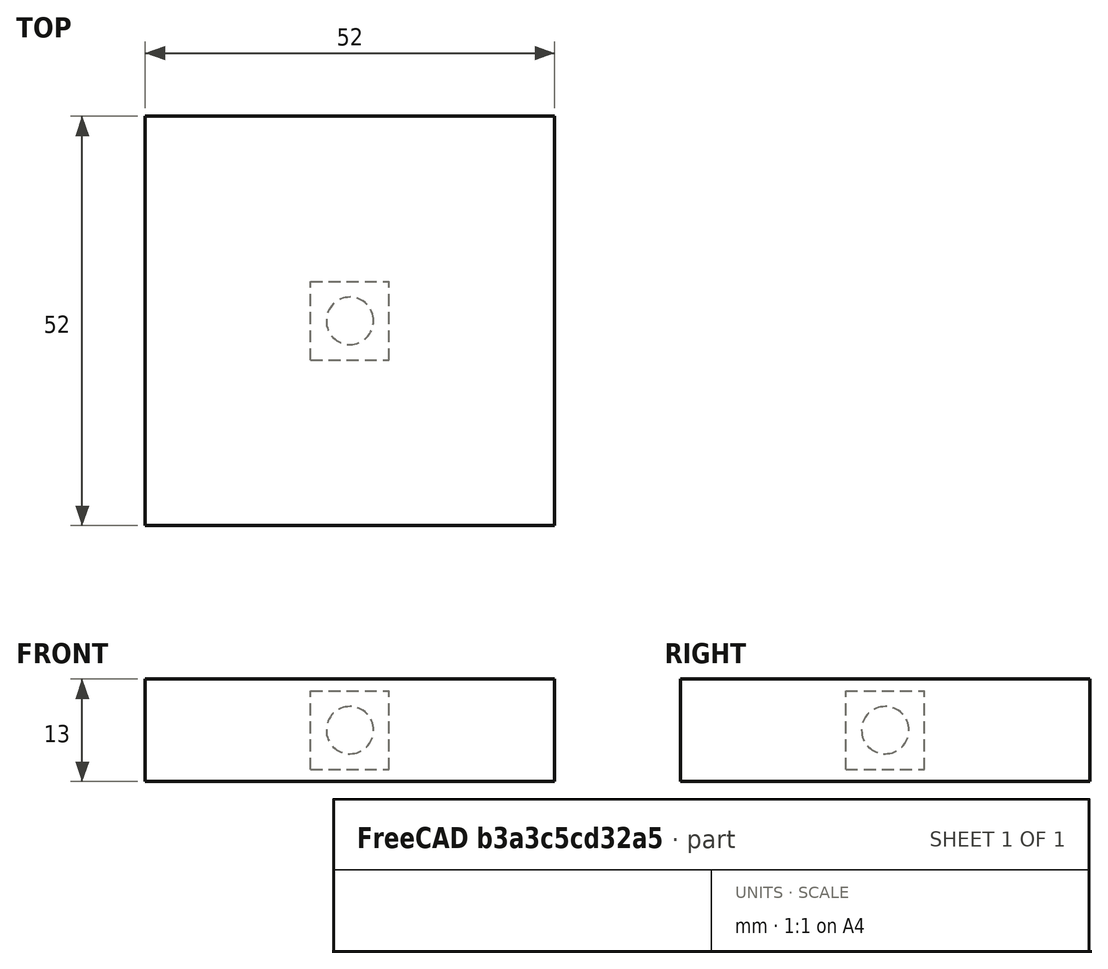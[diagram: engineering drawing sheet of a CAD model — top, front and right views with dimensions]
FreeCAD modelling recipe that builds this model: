
FCSTD DOCUMENT  (FreeCAD 0.21R33694 (Git))
Label: array-of-mother-daughter-vols-correct
License: All rights reserved
objects: App::DocumentObjectGroupPython×1251, Part::FeaturePython×5, App::Part×3
note: 3 computed .brp shape members not serialized (recipe doc carries the construction recipe); baked Part::Feature solids carry a one-line shape summary decoded from their .brp

FEATURE [App::DocumentObjectGroupPython] HALFPI  # scripted group (container) (typed FeaturePython)
  name = HALFPI
  value = pi/2.
FEATURE [App::DocumentObjectGroupPython] PI  # scripted group (container) (typed FeaturePython)
  name = PI
  value = 1.*pi
FEATURE [App::DocumentObjectGroupPython] TWOPI  # scripted group (container) (typed FeaturePython)
  name = TWOPI
  value = 2.*pi
FEATURE [App::DocumentObjectGroupPython] Constants  # scripted group (container) (typed FeaturePython)
  Group = -> [HALFPI,PI,TWOPI]
FEATURE [App::DocumentObjectGroupPython] Variables  # scripted group (container) (typed FeaturePython)
FEATURE [App::DocumentObjectGroupPython] Quantities  # scripted group (container) (typed FeaturePython)
FEATURE [App::DocumentObjectGroupPython] Isotopes  # scripted group (container) (typed FeaturePython)
FEATURE [App::DocumentObjectGroupPython] Elements  # scripted group (container) (typed FeaturePython)
FEATURE [App::DocumentObjectGroupPython] Matrix  # scripted group (container) (typed FeaturePython)
FEATURE [App::DocumentObjectGroupPython] Surfaces  # scripted group (container) (typed FeaturePython)
FEATURE [App::DocumentObjectGroupPython] Opticals  # scripted group (container) (typed FeaturePython)
  Group = -> [Matrix,Surfaces]
FEATURE [App::DocumentObjectGroupPython] G4Isotopes  # scripted group (container) (typed FeaturePython)
FEATURE [App::DocumentObjectGroupPython] H_element  # scripted group (container) (typed FeaturePython)
  Z = 1
  atom_value = 1.008
  formula = H
  name = H_element
FEATURE [App::DocumentObjectGroupPython] He_element  # scripted group (container) (typed FeaturePython)
  Z = 2
  atom_value = 4.0026
  formula = He
  name = He_element
FEATURE [App::DocumentObjectGroupPython] Li_element  # scripted group (container) (typed FeaturePython)
  Z = 3
  atom_value = 6.94
  formula = Li
  name = Li_element
FEATURE [App::DocumentObjectGroupPython] Be_element  # scripted group (container) (typed FeaturePython)
  Z = 4
  atom_value = 9.01218
  formula = Be
  name = Be_element
FEATURE [App::DocumentObjectGroupPython] B_element  # scripted group (container) (typed FeaturePython)
  Z = 5
  atom_value = 10.81
  formula = B
  name = B_element
FEATURE [App::DocumentObjectGroupPython] C_element  # scripted group (container) (typed FeaturePython)
  Z = 6
  atom_value = 12.011
  formula = C
  name = C_element
FEATURE [App::DocumentObjectGroupPython] N_element  # scripted group (container) (typed FeaturePython)
  Z = 7
  atom_value = 14.007
  formula = N
  name = N_element
FEATURE [App::DocumentObjectGroupPython] O_element  # scripted group (container) (typed FeaturePython)
  Z = 8
  atom_value = 15.999
  formula = O
  name = O_element
FEATURE [App::DocumentObjectGroupPython] F_element  # scripted group (container) (typed FeaturePython)
  Z = 9
  atom_value = 18.9984
  formula = F
  name = F_element
FEATURE [App::DocumentObjectGroupPython] Ne_element  # scripted group (container) (typed FeaturePython)
  Z = 10
  atom_value = 20.1797
  formula = Ne
  name = Ne_element
FEATURE [App::DocumentObjectGroupPython] Na_element  # scripted group (container) (typed FeaturePython)
  Z = 11
  atom_value = 22.9898
  formula = Na
  name = Na_element
FEATURE [App::DocumentObjectGroupPython] Mg_element  # scripted group (container) (typed FeaturePython)
  Z = 12
  atom_value = 24.305
  formula = Mg
  name = Mg_element
FEATURE [App::DocumentObjectGroupPython] Al_element  # scripted group (container) (typed FeaturePython)
  Z = 13
  atom_value = 26.9815
  formula = Al
  name = Al_element
FEATURE [App::DocumentObjectGroupPython] Si_element  # scripted group (container) (typed FeaturePython)
  Z = 14
  atom_value = 28.085
  formula = Si
  name = Si_element
FEATURE [App::DocumentObjectGroupPython] P_element  # scripted group (container) (typed FeaturePython)
  Z = 15
  atom_value = 30.9738
  formula = P
  name = P_element
FEATURE [App::DocumentObjectGroupPython] S_element  # scripted group (container) (typed FeaturePython)
  Z = 16
  atom_value = 32.06
  formula = S
  name = S_element
FEATURE [App::DocumentObjectGroupPython] Cl_element  # scripted group (container) (typed FeaturePython)
  Z = 17
  atom_value = 35.45
  formula = Cl
  name = Cl_element
FEATURE [App::DocumentObjectGroupPython] Ar_element  # scripted group (container) (typed FeaturePython)
  Z = 18
  atom_value = 39.95
  formula = Ar
  name = Ar_element
FEATURE [App::DocumentObjectGroupPython] K_element  # scripted group (container) (typed FeaturePython)
  Z = 19
  atom_value = 39.0983
  formula = K
  name = K_element
FEATURE [App::DocumentObjectGroupPython] Ca_element  # scripted group (container) (typed FeaturePython)
  Z = 20
  atom_value = 40.078
  formula = Ca
  name = Ca_element
FEATURE [App::DocumentObjectGroupPython] Sc_element  # scripted group (container) (typed FeaturePython)
  Z = 21
  atom_value = 44.9559
  formula = Sc
  name = Sc_element
FEATURE [App::DocumentObjectGroupPython] Ti_element  # scripted group (container) (typed FeaturePython)
  Z = 22
  atom_value = 47.867
  formula = Ti
  name = Ti_element
FEATURE [App::DocumentObjectGroupPython] V_element  # scripted group (container) (typed FeaturePython)
  Z = 23
  atom_value = 50.9415
  formula = V
  name = V_element
FEATURE [App::DocumentObjectGroupPython] Cr_element  # scripted group (container) (typed FeaturePython)
  Z = 24
  atom_value = 51.9961
  formula = Cr
  name = Cr_element
FEATURE [App::DocumentObjectGroupPython] Mn_element  # scripted group (container) (typed FeaturePython)
  Z = 25
  atom_value = 54.938
  formula = Mn
  name = Mn_element
FEATURE [App::DocumentObjectGroupPython] Fe_element  # scripted group (container) (typed FeaturePython)
  Z = 26
  atom_value = 55.845
  formula = Fe
  name = Fe_element
FEATURE [App::DocumentObjectGroupPython] Co_element  # scripted group (container) (typed FeaturePython)
  Z = 27
  atom_value = 58.9332
  formula = Co
  name = Co_element
FEATURE [App::DocumentObjectGroupPython] Ni_element  # scripted group (container) (typed FeaturePython)
  Z = 28
  atom_value = 58.6934
  formula = Ni
  name = Ni_element
FEATURE [App::DocumentObjectGroupPython] Cu_element  # scripted group (container) (typed FeaturePython)
  Z = 29
  atom_value = 63.546
  formula = Cu
  name = Cu_element
FEATURE [App::DocumentObjectGroupPython] Zn_element  # scripted group (container) (typed FeaturePython)
  Z = 30
  atom_value = 65.38
  formula = Zn
  name = Zn_element
FEATURE [App::DocumentObjectGroupPython] Ga_element  # scripted group (container) (typed FeaturePython)
  Z = 31
  atom_value = 69.723
  formula = Ga
  name = Ga_element
FEATURE [App::DocumentObjectGroupPython] Ge_element  # scripted group (container) (typed FeaturePython)
  Z = 32
  atom_value = 72.63
  formula = Ge
  name = Ge_element
FEATURE [App::DocumentObjectGroupPython] As_element  # scripted group (container) (typed FeaturePython)
  Z = 33
  atom_value = 74.9216
  formula = As
  name = As_element
FEATURE [App::DocumentObjectGroupPython] Se_element  # scripted group (container) (typed FeaturePython)
  Z = 34
  atom_value = 78.971
  formula = Se
  name = Se_element
FEATURE [App::DocumentObjectGroupPython] Br_element  # scripted group (container) (typed FeaturePython)
  Z = 35
  atom_value = 79.904
  formula = Br
  name = Br_element
FEATURE [App::DocumentObjectGroupPython] Kr_element  # scripted group (container) (typed FeaturePython)
  Z = 36
  atom_value = 83.798
  formula = Kr
  name = Kr_element
FEATURE [App::DocumentObjectGroupPython] Rb_element  # scripted group (container) (typed FeaturePython)
  Z = 37
  atom_value = 85.4678
  formula = Rb
  name = Rb_element
FEATURE [App::DocumentObjectGroupPython] Sr_element  # scripted group (container) (typed FeaturePython)
  Z = 38
  atom_value = 87.62
  formula = Sr
  name = Sr_element
FEATURE [App::DocumentObjectGroupPython] Y_element  # scripted group (container) (typed FeaturePython)
  Z = 39
  atom_value = 88.9058
  formula = Y
  name = Y_element
FEATURE [App::DocumentObjectGroupPython] Zr_element  # scripted group (container) (typed FeaturePython)
  Z = 40
  atom_value = 91.224
  formula = Zr
  name = Zr_element
FEATURE [App::DocumentObjectGroupPython] Nb_element  # scripted group (container) (typed FeaturePython)
  Z = 41
  atom_value = 92.9064
  formula = Nb
  name = Nb_element
FEATURE [App::DocumentObjectGroupPython] Mo_element  # scripted group (container) (typed FeaturePython)
  Z = 42
  atom_value = 95.95
  formula = Mo
  name = Mo_element
FEATURE [App::DocumentObjectGroupPython] Tc_element  # scripted group (container) (typed FeaturePython)
  Z = 43
  atom_value = 97
  formula = Tc
  name = Tc_element
FEATURE [App::DocumentObjectGroupPython] Ru_element  # scripted group (container) (typed FeaturePython)
  Z = 44
  atom_value = 101.07
  formula = Ru
  name = Ru_element
FEATURE [App::DocumentObjectGroupPython] Rh_element  # scripted group (container) (typed FeaturePython)
  Z = 45
  atom_value = 102.905
  formula = Rh
  name = Rh_element
FEATURE [App::DocumentObjectGroupPython] Pd_element  # scripted group (container) (typed FeaturePython)
  Z = 46
  atom_value = 106.42
  formula = Pd
  name = Pd_element
FEATURE [App::DocumentObjectGroupPython] Ag_element  # scripted group (container) (typed FeaturePython)
  Z = 47
  atom_value = 107.868
  formula = Ag
  name = Ag_element
FEATURE [App::DocumentObjectGroupPython] Cd_element  # scripted group (container) (typed FeaturePython)
  Z = 48
  atom_value = 112.414
  formula = Cd
  name = Cd_element
FEATURE [App::DocumentObjectGroupPython] In_element  # scripted group (container) (typed FeaturePython)
  Z = 49
  atom_value = 114.818
  formula = In
  name = In_element
FEATURE [App::DocumentObjectGroupPython] Sn_element  # scripted group (container) (typed FeaturePython)
  Z = 50
  atom_value = 118.71
  formula = Sn
  name = Sn_element
FEATURE [App::DocumentObjectGroupPython] Sb_element  # scripted group (container) (typed FeaturePython)
  Z = 51
  atom_value = 121.76
  formula = Sb
  name = Sb_element
FEATURE [App::DocumentObjectGroupPython] Te_element  # scripted group (container) (typed FeaturePython)
  Z = 52
  atom_value = 127.6
  formula = Te
  name = Te_element
FEATURE [App::DocumentObjectGroupPython] I_element  # scripted group (container) (typed FeaturePython)
  Z = 53
  atom_value = 126.904
  formula = I
  name = I_element
FEATURE [App::DocumentObjectGroupPython] Xe_element  # scripted group (container) (typed FeaturePython)
  Z = 54
  atom_value = 131.293
  formula = Xe
  name = Xe_element
FEATURE [App::DocumentObjectGroupPython] Cs_element  # scripted group (container) (typed FeaturePython)
  Z = 55
  atom_value = 132.905
  formula = Cs
  name = Cs_element
FEATURE [App::DocumentObjectGroupPython] Ba_element  # scripted group (container) (typed FeaturePython)
  Z = 56
  atom_value = 137.327
  formula = Ba
  name = Ba_element
FEATURE [App::DocumentObjectGroupPython] La_element  # scripted group (container) (typed FeaturePython)
  Z = 57
  atom_value = 138.905
  formula = La
  name = La_element
FEATURE [App::DocumentObjectGroupPython] Ce_element  # scripted group (container) (typed FeaturePython)
  Z = 58
  atom_value = 140.116
  formula = Ce
  name = Ce_element
FEATURE [App::DocumentObjectGroupPython] Pr_element  # scripted group (container) (typed FeaturePython)
  Z = 59
  atom_value = 140.908
  formula = Pr
  name = Pr_element
FEATURE [App::DocumentObjectGroupPython] Nd_element  # scripted group (container) (typed FeaturePython)
  Z = 60
  atom_value = 144.242
  formula = Nd
  name = Nd_element
FEATURE [App::DocumentObjectGroupPython] Pm_element  # scripted group (container) (typed FeaturePython)
  Z = 61
  atom_value = 145
  formula = Pm
  name = Pm_element
FEATURE [App::DocumentObjectGroupPython] Sm_element  # scripted group (container) (typed FeaturePython)
  Z = 62
  atom_value = 150.36
  formula = Sm
  name = Sm_element
FEATURE [App::DocumentObjectGroupPython] Eu_element  # scripted group (container) (typed FeaturePython)
  Z = 63
  atom_value = 151.964
  formula = Eu
  name = Eu_element
FEATURE [App::DocumentObjectGroupPython] Gd_element  # scripted group (container) (typed FeaturePython)
  Z = 64
  atom_value = 157.25
  formula = Gd
  name = Gd_element
FEATURE [App::DocumentObjectGroupPython] Tb_element  # scripted group (container) (typed FeaturePython)
  Z = 65
  atom_value = 158.925
  formula = Tb
  name = Tb_element
FEATURE [App::DocumentObjectGroupPython] Dy_element  # scripted group (container) (typed FeaturePython)
  Z = 66
  atom_value = 162.5
  formula = Dy
  name = Dy_element
FEATURE [App::DocumentObjectGroupPython] Ho_element  # scripted group (container) (typed FeaturePython)
  Z = 67
  atom_value = 164.93
  formula = Ho
  name = Ho_element
FEATURE [App::DocumentObjectGroupPython] Er_element  # scripted group (container) (typed FeaturePython)
  Z = 68
  atom_value = 167.259
  formula = Er
  name = Er_element
FEATURE [App::DocumentObjectGroupPython] Tm_element  # scripted group (container) (typed FeaturePython)
  Z = 69
  atom_value = 168.934
  formula = Tm
  name = Tm_element
FEATURE [App::DocumentObjectGroupPython] Yb_element  # scripted group (container) (typed FeaturePython)
  Z = 70
  atom_value = 173.045
  formula = Yb
  name = Yb_element
FEATURE [App::DocumentObjectGroupPython] Lu_element  # scripted group (container) (typed FeaturePython)
  Z = 71
  atom_value = 174.967
  formula = Lu
  name = Lu_element
FEATURE [App::DocumentObjectGroupPython] Hf_element  # scripted group (container) (typed FeaturePython)
  Z = 72
  atom_value = 178.49
  formula = Hf
  name = Hf_element
FEATURE [App::DocumentObjectGroupPython] Ta_element  # scripted group (container) (typed FeaturePython)
  Z = 73
  atom_value = 180.948
  formula = Ta
  name = Ta_element
FEATURE [App::DocumentObjectGroupPython] W_element  # scripted group (container) (typed FeaturePython)
  Z = 74
  atom_value = 183.84
  formula = W
  name = W_element
FEATURE [App::DocumentObjectGroupPython] Re_element  # scripted group (container) (typed FeaturePython)
  Z = 75
  atom_value = 186.207
  formula = Re
  name = Re_element
FEATURE [App::DocumentObjectGroupPython] Os_element  # scripted group (container) (typed FeaturePython)
  Z = 76
  atom_value = 190.23
  formula = Os
  name = Os_element
FEATURE [App::DocumentObjectGroupPython] Ir_element  # scripted group (container) (typed FeaturePython)
  Z = 77
  atom_value = 192.217
  formula = Ir
  name = Ir_element
FEATURE [App::DocumentObjectGroupPython] Pt_element  # scripted group (container) (typed FeaturePython)
  Z = 78
  atom_value = 195.084
  formula = Pt
  name = Pt_element
FEATURE [App::DocumentObjectGroupPython] Au_element  # scripted group (container) (typed FeaturePython)
  Z = 79
  atom_value = 196.967
  formula = Au
  name = Au_element
FEATURE [App::DocumentObjectGroupPython] Hg_element  # scripted group (container) (typed FeaturePython)
  Z = 80
  atom_value = 200.592
  formula = Hg
  name = Hg_element
FEATURE [App::DocumentObjectGroupPython] Tl_element  # scripted group (container) (typed FeaturePython)
  Z = 81
  atom_value = 204.38
  formula = Tl
  name = Tl_element
FEATURE [App::DocumentObjectGroupPython] Pb_element  # scripted group (container) (typed FeaturePython)
  Z = 82
  atom_value = 207.2
  formula = Pb
  name = Pb_element
FEATURE [App::DocumentObjectGroupPython] Bi_element  # scripted group (container) (typed FeaturePython)
  Z = 83
  atom_value = 208.98
  formula = Bi
  name = Bi_element
FEATURE [App::DocumentObjectGroupPython] Po_element  # scripted group (container) (typed FeaturePython)
  Z = 84
  atom_value = 209
  formula = Po
  name = Po_element
FEATURE [App::DocumentObjectGroupPython] At_element  # scripted group (container) (typed FeaturePython)
  Z = 85
  atom_value = 210
  formula = At
  name = At_element
FEATURE [App::DocumentObjectGroupPython] Rn_element  # scripted group (container) (typed FeaturePython)
  Z = 86
  atom_value = 222
  formula = Rn
  name = Rn_element
FEATURE [App::DocumentObjectGroupPython] Fr_element  # scripted group (container) (typed FeaturePython)
  Z = 87
  atom_value = 223
  formula = Fr
  name = Fr_element
FEATURE [App::DocumentObjectGroupPython] Ra_element  # scripted group (container) (typed FeaturePython)
  Z = 88
  atom_value = 226
  formula = Ra
  name = Ra_element
FEATURE [App::DocumentObjectGroupPython] Ac_element  # scripted group (container) (typed FeaturePython)
  Z = 89
  atom_value = 227
  formula = Ac
  name = Ac_element
FEATURE [App::DocumentObjectGroupPython] Th_element  # scripted group (container) (typed FeaturePython)
  Z = 90
  atom_value = 232.038
  formula = Th
  name = Th_element
FEATURE [App::DocumentObjectGroupPython] Pa_element  # scripted group (container) (typed FeaturePython)
  Z = 91
  atom_value = 231.036
  formula = Pa
  name = Pa_element
FEATURE [App::DocumentObjectGroupPython] U_element  # scripted group (container) (typed FeaturePython)
  Z = 92
  atom_value = 238.029
  formula = U
  name = U_element
FEATURE [App::DocumentObjectGroupPython] Np_element  # scripted group (container) (typed FeaturePython)
  Z = 93
  atom_value = 237
  formula = Np
  name = Np_element
FEATURE [App::DocumentObjectGroupPython] Pu_element  # scripted group (container) (typed FeaturePython)
  Z = 94
  atom_value = 244
  formula = Pu
  name = Pu_element
FEATURE [App::DocumentObjectGroupPython] Am_element  # scripted group (container) (typed FeaturePython)
  Z = 95
  atom_value = 243
  formula = Am
  name = Am_element
FEATURE [App::DocumentObjectGroupPython] Cm_element  # scripted group (container) (typed FeaturePython)
  Z = 96
  atom_value = 247
  formula = Cm
  name = Cm_element
FEATURE [App::DocumentObjectGroupPython] Bk_element  # scripted group (container) (typed FeaturePython)
  Z = 97
  atom_value = 247
  formula = Bk
  name = Bk_element
FEATURE [App::DocumentObjectGroupPython] Cf_element  # scripted group (container) (typed FeaturePython)
  Z = 98
  atom_value = 251
  formula = Cf
  name = Cf_element
FEATURE [App::DocumentObjectGroupPython] G4Elements  # scripted group (container) (typed FeaturePython)
  Group = -> [H_element,He_element,Li_element,Be_element,B_element,C_element,N_element,O_element,F_element,Ne_element,Na_element,Mg_element,Al_element,Si_element,P_element,S_element,Cl_element,Ar_element,K_element,Ca_element,Sc_element,Ti_element,V_element,Cr_element,Mn_element,Fe_element,Co_element,Ni_element,Cu_element,Zn_element,Ga_element,Ge_element,As_element,Se_element,Br_element,Kr_element,Rb_element,+61 more]
FEATURE [App::DocumentObjectGroupPython] H_element001  label="H_element : 0.101"  # scripted group (container) (typed FeaturePython)
  n = 0.101327
FEATURE [App::DocumentObjectGroupPython] C_element001  label="C_element : 0.775"  # scripted group (container) (typed FeaturePython)
  n = 0.7755
FEATURE [App::DocumentObjectGroupPython] N_element001  label="N_element : 0.035"  # scripted group (container) (typed FeaturePython)
  n = 0.035057
FEATURE [App::DocumentObjectGroupPython] O_element001  label="O_element : 0.052"  # scripted group (container) (typed FeaturePython)
  n = 0.0523159
FEATURE [App::DocumentObjectGroupPython] F_element001  label="F_element : 0.017"  # scripted group (container) (typed FeaturePython)
  n = 0.017422
FEATURE [App::DocumentObjectGroupPython] Ca_element001  label="Ca_element : 0.018"  # scripted group (container) (typed FeaturePython)
  n = 0.018378
FEATURE [App::DocumentObjectGroupPython] G4_A_150_TISSUE  label="G4_A-150_TISSUE"  # scripted group (container) (typed FeaturePython)
  Dunit = g/cm3
  Dvalue = 1.127
  Group = -> [H_element001,C_element001,N_element001,O_element001,F_element001,Ca_element001]
  conduct = 2
  density = 1
  expand = 3
  formula = G4_A-150_TISSUE
  name = G4_A-150_TISSUE
  specific = 4
FEATURE [App::DocumentObjectGroupPython] C_element002  label="C_element : 3"  # scripted group (container) (typed FeaturePython)
  n = 3
  ref = C_element
FEATURE [App::DocumentObjectGroupPython] H_element002  label="H_element : 6"  # scripted group (container) (typed FeaturePython)
  n = 6
  ref = H_element
FEATURE [App::DocumentObjectGroupPython] O_element002  label="O_element : 1"  # scripted group (container) (typed FeaturePython)
  n = 1
  ref = O_element
FEATURE [App::DocumentObjectGroupPython] G4_ACETONE  # scripted group (container) (typed FeaturePython)
  Dunit = g/cm3
  Dvalue = 0.7899
  Group = -> [C_element002,H_element002,O_element002]
  conduct = 2
  density = 1
  expand = 3
  formula = G4_ACETONE
  name = G4_ACETONE
  specific = 4
FEATURE [App::DocumentObjectGroupPython] C_element003  label="C_element : 2"  # scripted group (container) (typed FeaturePython)
  n = 2
  ref = C_element
FEATURE [App::DocumentObjectGroupPython] H_element003  label="H_element : 2"  # scripted group (container) (typed FeaturePython)
  n = 2
  ref = H_element
FEATURE [App::DocumentObjectGroupPython] G4_ACETYLENE  # scripted group (container) (typed FeaturePython)
  Dunit = g/cm3
  Dvalue = 0.0010967
  Group = -> [C_element003,H_element003]
  conduct = 2
  density = 1
  expand = 3
  formula = G4_ACETYLENE
  name = G4_ACETYLENE
  specific = 4
FEATURE [App::DocumentObjectGroupPython] C_element004  label="C_element : 5"  # scripted group (container) (typed FeaturePython)
  n = 5
  ref = C_element
FEATURE [App::DocumentObjectGroupPython] H_element004  label="H_element : 5"  # scripted group (container) (typed FeaturePython)
  n = 5
  ref = H_element
FEATURE [App::DocumentObjectGroupPython] N_element002  label="N_element : 5"  # scripted group (container) (typed FeaturePython)
  n = 5
  ref = N_element
FEATURE [App::DocumentObjectGroupPython] G4_ADENINE  # scripted group (container) (typed FeaturePython)
  Dunit = g/cm3
  Dvalue = 1.6
  Group = -> [C_element004,H_element004,N_element002]
  conduct = 2
  density = 1
  expand = 3
  formula = G4_ADENINE
  name = G4_ADENINE
  specific = 4
FEATURE [App::DocumentObjectGroupPython] H_element005  label="H_element : 0.114"  # scripted group (container) (typed FeaturePython)
  n = 0.114
FEATURE [App::DocumentObjectGroupPython] C_element005  label="C_element : 0.598"  # scripted group (container) (typed FeaturePython)
  n = 0.598
FEATURE [App::DocumentObjectGroupPython] N_element003  label="N_element : 0.007"  # scripted group (container) (typed FeaturePython)
  n = 0.007
FEATURE [App::DocumentObjectGroupPython] O_element003  label="O_element : 0.278"  # scripted group (container) (typed FeaturePython)
  n = 0.278
FEATURE [App::DocumentObjectGroupPython] Na_element001  label="Na_element : 0.001"  # scripted group (container) (typed FeaturePython)
  n = 0.001
FEATURE [App::DocumentObjectGroupPython] S_element001  label="S_element : 0.001"  # scripted group (container) (typed FeaturePython)
  n = 0.001
FEATURE [App::DocumentObjectGroupPython] Cl_element001  label="Cl_element : 0.001"  # scripted group (container) (typed FeaturePython)
  n = 0.001
FEATURE [App::DocumentObjectGroupPython] G4_ADIPOSE_TISSUE_ICRP  # scripted group (container) (typed FeaturePython)
  Dunit = g/cm3
  Dvalue = 0.95
  Group = -> [H_element005,C_element005,N_element003,O_element003,Na_element001,S_element001,Cl_element001]
  conduct = 2
  density = 1
  expand = 3
  formula = G4_ADIPOSE_TISSUE_ICRP
  name = G4_ADIPOSE_TISSUE_ICRP
  specific = 4
FEATURE [App::DocumentObjectGroupPython] C_element006  label="C_element : 0.000"  # scripted group (container) (typed FeaturePython)
  n = 0.000124
FEATURE [App::DocumentObjectGroupPython] N_element004  label="N_element : 0.755"  # scripted group (container) (typed FeaturePython)
  n = 0.755268
FEATURE [App::DocumentObjectGroupPython] O_element004  label="O_element : 0.232"  # scripted group (container) (typed FeaturePython)
  n = 0.231781
FEATURE [App::DocumentObjectGroupPython] Ar_element001  label="Ar_element : 0.013"  # scripted group (container) (typed FeaturePython)
  n = 0.012827
FEATURE [App::DocumentObjectGroupPython] G4_AIR  # scripted group (container) (typed FeaturePython)
  Dunit = g/cm3
  Dvalue = 0.00120479
  Group = -> [C_element006,N_element004,O_element004,Ar_element001]
  conduct = 2
  density = 1
  expand = 3
  formula = G4_AIR
  name = G4_AIR
  specific = 4
FEATURE [App::DocumentObjectGroupPython] C_element007  label="C_element : 006"  # scripted group (container) (typed FeaturePython)
  n = 3
  ref = C_element
FEATURE [App::DocumentObjectGroupPython] H_element006  label="H_element : 7"  # scripted group (container) (typed FeaturePython)
  n = 7
  ref = H_element
FEATURE [App::DocumentObjectGroupPython] N_element005  label="N_element : 1"  # scripted group (container) (typed FeaturePython)
  n = 1
  ref = N_element
FEATURE [App::DocumentObjectGroupPython] O_element005  label="O_element : 2"  # scripted group (container) (typed FeaturePython)
  n = 2
  ref = O_element
FEATURE [App::DocumentObjectGroupPython] G4_ALANINE  # scripted group (container) (typed FeaturePython)
  Dunit = g/cm3
  Dvalue = 1.42
  Group = -> [C_element007,H_element006,N_element005,O_element005]
  conduct = 2
  density = 1
  expand = 3
  formula = G4_ALANINE
  name = G4_ALANINE
  specific = 4
FEATURE [App::DocumentObjectGroupPython] Al_element001  label="Al_element : 2"  # scripted group (container) (typed FeaturePython)
  n = 2
  ref = Al_element
FEATURE [App::DocumentObjectGroupPython] O_element006  label="O_element : 3"  # scripted group (container) (typed FeaturePython)
  n = 3
  ref = O_element
FEATURE [App::DocumentObjectGroupPython] G4_ALUMINUM_OXIDE  # scripted group (container) (typed FeaturePython)
  Dunit = g/cm3
  Dvalue = 3.97
  Group = -> [Al_element001,O_element006]
  conduct = 2
  density = 1
  expand = 3
  formula = G4_ALUMINUM_OXIDE
  name = G4_ALUMINUM_OXIDE
  specific = 4
FEATURE [App::DocumentObjectGroupPython] H_element007  label="H_element : 0.106"  # scripted group (container) (typed FeaturePython)
  n = 0.10593
FEATURE [App::DocumentObjectGroupPython] C_element008  label="C_element : 0.789"  # scripted group (container) (typed FeaturePython)
  n = 0.788974
FEATURE [App::DocumentObjectGroupPython] O_element007  label="O_element : 0.105"  # scripted group (container) (typed FeaturePython)
  n = 0.105096
FEATURE [App::DocumentObjectGroupPython] G4_AMBER  # scripted group (container) (typed FeaturePython)
  Dunit = g/cm3
  Dvalue = 1.1
  Group = -> [H_element007,C_element008,O_element007]
  conduct = 2
  density = 1
  expand = 3
  formula = G4_AMBER
  name = G4_AMBER
  specific = 4
FEATURE [App::DocumentObjectGroupPython] N_element006  label="N_element : 006"  # scripted group (container) (typed FeaturePython)
  n = 1
  ref = N_element
FEATURE [App::DocumentObjectGroupPython] H_element008  label="H_element : 3"  # scripted group (container) (typed FeaturePython)
  n = 3
  ref = H_element
FEATURE [App::DocumentObjectGroupPython] G4_AMMONIA  # scripted group (container) (typed FeaturePython)
  Dunit = g/cm3
  Dvalue = 0.000826019
  Group = -> [N_element006,H_element008]
  conduct = 2
  density = 1
  expand = 3
  formula = G4_AMMONIA
  name = G4_AMMONIA
  specific = 4
FEATURE [App::DocumentObjectGroupPython] C_element009  label="C_element : 6"  # scripted group (container) (typed FeaturePython)
  n = 6
  ref = C_element
FEATURE [App::DocumentObjectGroupPython] H_element009  label="H_element : 008"  # scripted group (container) (typed FeaturePython)
  n = 7
  ref = H_element
FEATURE [App::DocumentObjectGroupPython] N_element007  label="N_element : 007"  # scripted group (container) (typed FeaturePython)
  n = 1
  ref = N_element
FEATURE [App::DocumentObjectGroupPython] G4_ANILINE  # scripted group (container) (typed FeaturePython)
  Dunit = g/cm3
  Dvalue = 1.0235
  Group = -> [C_element009,H_element009,N_element007]
  conduct = 2
  density = 1
  expand = 3
  formula = G4_ANILINE
  name = G4_ANILINE
  specific = 4
FEATURE [App::DocumentObjectGroupPython] C_element010  label="C_element : 14"  # scripted group (container) (typed FeaturePython)
  n = 14
  ref = C_element
FEATURE [App::DocumentObjectGroupPython] H_element010  label="H_element : 10"  # scripted group (container) (typed FeaturePython)
  n = 10
  ref = H_element
FEATURE [App::DocumentObjectGroupPython] G4_ANTHRACENE  # scripted group (container) (typed FeaturePython)
  Dunit = g/cm3
  Dvalue = 1.283
  Group = -> [C_element010,H_element010]
  conduct = 2
  density = 1
  expand = 3
  formula = G4_ANTHRACENE
  name = G4_ANTHRACENE
  specific = 4
FEATURE [App::DocumentObjectGroupPython] H_element011  label="H_element : 0.065"  # scripted group (container) (typed FeaturePython)
  n = 0.0654709
FEATURE [App::DocumentObjectGroupPython] C_element011  label="C_element : 0.537"  # scripted group (container) (typed FeaturePython)
  n = 0.536944
FEATURE [App::DocumentObjectGroupPython] N_element008  label="N_element : 0.021"  # scripted group (container) (typed FeaturePython)
  n = 0.0215
FEATURE [App::DocumentObjectGroupPython] O_element008  label="O_element : 0.032"  # scripted group (container) (typed FeaturePython)
  n = 0.032085
FEATURE [App::DocumentObjectGroupPython] F_element002  label="F_element : 0.167"  # scripted group (container) (typed FeaturePython)
  n = 0.167411
FEATURE [App::DocumentObjectGroupPython] Ca_element002  label="Ca_element : 0.177"  # scripted group (container) (typed FeaturePython)
  n = 0.176589
FEATURE [App::DocumentObjectGroupPython] G4_B_100_BONE  label="G4_B-100_BONE"  # scripted group (container) (typed FeaturePython)
  Dunit = g/cm3
  Dvalue = 1.45
  Group = -> [H_element011,C_element011,N_element008,O_element008,F_element002,Ca_element002]
  conduct = 2
  density = 1
  expand = 3
  formula = G4_B-100_BONE
  name = G4_B-100_BONE
  specific = 4
FEATURE [App::DocumentObjectGroupPython] H_element012  label="H_element : 0.057"  # scripted group (container) (typed FeaturePython)
  n = 0.057441
FEATURE [App::DocumentObjectGroupPython] C_element012  label="C_element : 0.790"  # scripted group (container) (typed FeaturePython)
  n = 0.774591
FEATURE [App::DocumentObjectGroupPython] O_element009  label="O_element : 0.168"  # scripted group (container) (typed FeaturePython)
  n = 0.167968
FEATURE [App::DocumentObjectGroupPython] G4_BAKELITE  # scripted group (container) (typed FeaturePython)
  Dunit = g/cm3
  Dvalue = 1.25
  Group = -> [H_element012,C_element012,O_element009]
  conduct = 2
  density = 1
  expand = 3
  formula = G4_BAKELITE
  name = G4_BAKELITE
  specific = 4
FEATURE [App::DocumentObjectGroupPython] Ba_element001  label="Ba_element : 1"  # scripted group (container) (typed FeaturePython)
  n = 1
  ref = Ba_element
FEATURE [App::DocumentObjectGroupPython] F_element003  label="F_element : 2"  # scripted group (container) (typed FeaturePython)
  n = 2
  ref = F_element
FEATURE [App::DocumentObjectGroupPython] G4_BARIUM_FLUORIDE  # scripted group (container) (typed FeaturePython)
  Dunit = g/cm3
  Dvalue = 4.89
  Group = -> [Ba_element001,F_element003]
  conduct = 2
  density = 1
  expand = 3
  formula = G4_BARIUM_FLUORIDE
  name = G4_BARIUM_FLUORIDE
  specific = 4
FEATURE [App::DocumentObjectGroupPython] Ba_element002  label="Ba_element : 002"  # scripted group (container) (typed FeaturePython)
  n = 1
  ref = Ba_element
FEATURE [App::DocumentObjectGroupPython] S_element002  label="S_element : 1"  # scripted group (container) (typed FeaturePython)
  n = 1
  ref = S_element
FEATURE [App::DocumentObjectGroupPython] O_element010  label="O_element : 4"  # scripted group (container) (typed FeaturePython)
  n = 4
  ref = O_element
FEATURE [App::DocumentObjectGroupPython] G4_BARIUM_SULFATE  # scripted group (container) (typed FeaturePython)
  Dunit = g/cm3
  Dvalue = 4.5
  Group = -> [Ba_element002,S_element002,O_element010]
  conduct = 2
  density = 1
  expand = 3
  formula = G4_BARIUM_SULFATE
  name = G4_BARIUM_SULFATE
  specific = 4
FEATURE [App::DocumentObjectGroupPython] C_element013  label="C_element : 007"  # scripted group (container) (typed FeaturePython)
  n = 6
  ref = C_element
FEATURE [App::DocumentObjectGroupPython] H_element013  label="H_element : 009"  # scripted group (container) (typed FeaturePython)
  n = 6
  ref = H_element
FEATURE [App::DocumentObjectGroupPython] G4_BENZENE  # scripted group (container) (typed FeaturePython)
  Dunit = g/cm3
  Dvalue = 0.87865
  Group = -> [C_element013,H_element013]
  conduct = 2
  density = 1
  expand = 3
  formula = G4_BENZENE
  name = G4_BENZENE
  specific = 4
FEATURE [App::DocumentObjectGroupPython] Be_element001  label="Be_element : 1"  # scripted group (container) (typed FeaturePython)
  n = 1
  ref = Be_element
FEATURE [App::DocumentObjectGroupPython] O_element011  label="O_element : 005"  # scripted group (container) (typed FeaturePython)
  n = 1
  ref = O_element
FEATURE [App::DocumentObjectGroupPython] G4_BERYLLIUM_OXIDE  # scripted group (container) (typed FeaturePython)
  Dunit = g/cm3
  Dvalue = 3.01
  Group = -> [Be_element001,O_element011]
  conduct = 2
  density = 1
  expand = 3
  formula = G4_BERYLLIUM_OXIDE
  name = G4_BERYLLIUM_OXIDE
  specific = 4
FEATURE [App::DocumentObjectGroupPython] Bi_element001  label="Bi_element : 4"  # scripted group (container) (typed FeaturePython)
  n = 4
  ref = Bi_element
FEATURE [App::DocumentObjectGroupPython] Ge_element001  label="Ge_element : 3"  # scripted group (container) (typed FeaturePython)
  n = 3
  ref = Ge_element
FEATURE [App::DocumentObjectGroupPython] O_element012  label="O_element : 12"  # scripted group (container) (typed FeaturePython)
  n = 12
  ref = O_element
FEATURE [App::DocumentObjectGroupPython] G4_BGO  # scripted group (container) (typed FeaturePython)
  Dunit = g/cm3
  Dvalue = 7.13
  Group = -> [Bi_element001,Ge_element001,O_element012]
  conduct = 2
  density = 1
  expand = 3
  formula = G4_BGO
  name = G4_BGO
  specific = 4
FEATURE [App::DocumentObjectGroupPython] H_element014  label="H_element : 0.102"  # scripted group (container) (typed FeaturePython)
  n = 0.102
FEATURE [App::DocumentObjectGroupPython] C_element014  label="C_element : 0.110"  # scripted group (container) (typed FeaturePython)
  n = 0.11
FEATURE [App::DocumentObjectGroupPython] N_element009  label="N_element : 0.033"  # scripted group (container) (typed FeaturePython)
  n = 0.033
FEATURE [App::DocumentObjectGroupPython] O_element013  label="O_element : 0.745"  # scripted group (container) (typed FeaturePython)
  n = 0.745
FEATURE [App::DocumentObjectGroupPython] Na_element002  label="Na_element : 0.002"  # scripted group (container) (typed FeaturePython)
  n = 0.001
FEATURE [App::DocumentObjectGroupPython] P_element001  label="P_element : 0.001"  # scripted group (container) (typed FeaturePython)
  n = 0.001
FEATURE [App::DocumentObjectGroupPython] S_element003  label="S_element : 0.002"  # scripted group (container) (typed FeaturePython)
  n = 0.002
FEATURE [App::DocumentObjectGroupPython] Cl_element002  label="Cl_element : 0.003"  # scripted group (container) (typed FeaturePython)
  n = 0.003
FEATURE [App::DocumentObjectGroupPython] K_element001  label="K_element : 0.002"  # scripted group (container) (typed FeaturePython)
  n = 0.002
FEATURE [App::DocumentObjectGroupPython] Fe_element001  label="Fe_element : 0.001"  # scripted group (container) (typed FeaturePython)
  n = 0.001
FEATURE [App::DocumentObjectGroupPython] G4_BLOOD_ICRP  # scripted group (container) (typed FeaturePython)
  Dunit = g/cm3
  Dvalue = 1.06
  Group = -> [H_element014,C_element014,N_element009,O_element013,Na_element002,P_element001,S_element003,Cl_element002,K_element001,Fe_element001]
  conduct = 2
  density = 1
  expand = 3
  formula = G4_BLOOD_ICRP
  name = G4_BLOOD_ICRP
  specific = 4
FEATURE [App::DocumentObjectGroupPython] H_element015  label="H_element : 0.064"  # scripted group (container) (typed FeaturePython)
  n = 0.064
FEATURE [App::DocumentObjectGroupPython] C_element015  label="C_element : 0.278"  # scripted group (container) (typed FeaturePython)
  n = 0.278
FEATURE [App::DocumentObjectGroupPython] N_element010  label="N_element : 0.027"  # scripted group (container) (typed FeaturePython)
  n = 0.027
FEATURE [App::DocumentObjectGroupPython] O_element014  label="O_element : 0.410"  # scripted group (container) (typed FeaturePython)
  n = 0.41
FEATURE [App::DocumentObjectGroupPython] Mg_element001  label="Mg_element : 0.002"  # scripted group (container) (typed FeaturePython)
  n = 0.002
FEATURE [App::DocumentObjectGroupPython] P_element002  label="P_element : 0.070"  # scripted group (container) (typed FeaturePython)
  n = 0.07
FEATURE [App::DocumentObjectGroupPython] S_element004  label="S_element : 0.003"  # scripted group (container) (typed FeaturePython)
  n = 0.002
FEATURE [App::DocumentObjectGroupPython] Ca_element003  label="Ca_element : 0.147"  # scripted group (container) (typed FeaturePython)
  n = 0.147
FEATURE [App::DocumentObjectGroupPython] G4_BONE_COMPACT_ICRU  # scripted group (container) (typed FeaturePython)
  Dunit = g/cm3
  Dvalue = 1.85
  Group = -> [H_element015,C_element015,N_element010,O_element014,Mg_element001,P_element002,S_element004,Ca_element003]
  conduct = 2
  density = 1
  expand = 3
  formula = G4_BONE_COMPACT_ICRU
  name = G4_BONE_COMPACT_ICRU
  specific = 4
FEATURE [App::DocumentObjectGroupPython] H_element016  label="H_element : 0.034"  # scripted group (container) (typed FeaturePython)
  n = 0.034
FEATURE [App::DocumentObjectGroupPython] C_element016  label="C_element : 0.155"  # scripted group (container) (typed FeaturePython)
  n = 0.155
FEATURE [App::DocumentObjectGroupPython] N_element011  label="N_element : 0.042"  # scripted group (container) (typed FeaturePython)
  n = 0.042
FEATURE [App::DocumentObjectGroupPython] O_element015  label="O_element : 0.435"  # scripted group (container) (typed FeaturePython)
  n = 0.435
FEATURE [App::DocumentObjectGroupPython] Na_element003  label="Na_element : 0.003"  # scripted group (container) (typed FeaturePython)
  n = 0.001
FEATURE [App::DocumentObjectGroupPython] Mg_element002  label="Mg_element : 0.003"  # scripted group (container) (typed FeaturePython)
  n = 0.002
FEATURE [App::DocumentObjectGroupPython] P_element003  label="P_element : 0.103"  # scripted group (container) (typed FeaturePython)
  n = 0.103
FEATURE [App::DocumentObjectGroupPython] S_element005  label="S_element : 0.004"  # scripted group (container) (typed FeaturePython)
  n = 0.003
FEATURE [App::DocumentObjectGroupPython] Ca_element004  label="Ca_element : 0.225"  # scripted group (container) (typed FeaturePython)
  n = 0.225
FEATURE [App::DocumentObjectGroupPython] G4_BONE_CORTICAL_ICRP  # scripted group (container) (typed FeaturePython)
  Dunit = g/cm3
  Dvalue = 1.92
  Group = -> [H_element016,C_element016,N_element011,O_element015,Na_element003,Mg_element002,P_element003,S_element005,Ca_element004]
  conduct = 2
  density = 1
  expand = 3
  formula = G4_BONE_CORTICAL_ICRP
  name = G4_BONE_CORTICAL_ICRP
  specific = 4
FEATURE [App::DocumentObjectGroupPython] B_element001  label="B_element : 4"  # scripted group (container) (typed FeaturePython)
  n = 4
  ref = B_element
FEATURE [App::DocumentObjectGroupPython] C_element017  label="C_element : 1"  # scripted group (container) (typed FeaturePython)
  n = 1
  ref = C_element
FEATURE [App::DocumentObjectGroupPython] G4_BORON_CARBIDE  # scripted group (container) (typed FeaturePython)
  Dunit = g/cm3
  Dvalue = 2.52
  Group = -> [B_element001,C_element017]
  conduct = 2
  density = 1
  expand = 3
  formula = G4_BORON_CARBIDE
  name = G4_BORON_CARBIDE
  specific = 4
FEATURE [App::DocumentObjectGroupPython] B_element002  label="B_element : 2"  # scripted group (container) (typed FeaturePython)
  n = 2
  ref = B_element
FEATURE [App::DocumentObjectGroupPython] O_element016  label="O_element : 006"  # scripted group (container) (typed FeaturePython)
  n = 3
  ref = O_element
FEATURE [App::DocumentObjectGroupPython] G4_BORON_OXIDE  # scripted group (container) (typed FeaturePython)
  Dunit = g/cm3
  Dvalue = 1.812
  Group = -> [B_element002,O_element016]
  conduct = 2
  density = 1
  expand = 3
  formula = G4_BORON_OXIDE
  name = G4_BORON_OXIDE
  specific = 4
FEATURE [App::DocumentObjectGroupPython] H_element017  label="H_element : 0.107"  # scripted group (container) (typed FeaturePython)
  n = 0.107
FEATURE [App::DocumentObjectGroupPython] C_element018  label="C_element : 0.145"  # scripted group (container) (typed FeaturePython)
  n = 0.145
FEATURE [App::DocumentObjectGroupPython] N_element012  label="N_element : 0.022"  # scripted group (container) (typed FeaturePython)
  n = 0.022
FEATURE [App::DocumentObjectGroupPython] O_element017  label="O_element : 0.712"  # scripted group (container) (typed FeaturePython)
  n = 0.712
FEATURE [App::DocumentObjectGroupPython] Na_element004  label="Na_element : 0.004"  # scripted group (container) (typed FeaturePython)
  n = 0.002
FEATURE [App::DocumentObjectGroupPython] P_element004  label="P_element : 0.004"  # scripted group (container) (typed FeaturePython)
  n = 0.004
FEATURE [App::DocumentObjectGroupPython] S_element006  label="S_element : 0.005"  # scripted group (container) (typed FeaturePython)
  n = 0.002
FEATURE [App::DocumentObjectGroupPython] Cl_element003  label="Cl_element : 0.004"  # scripted group (container) (typed FeaturePython)
  n = 0.003
FEATURE [App::DocumentObjectGroupPython] K_element002  label="K_element : 0.003"  # scripted group (container) (typed FeaturePython)
  n = 0.003
FEATURE [App::DocumentObjectGroupPython] G4_BRAIN_ICRP  # scripted group (container) (typed FeaturePython)
  Dunit = g/cm3
  Dvalue = 1.04
  Group = -> [H_element017,C_element018,N_element012,O_element017,Na_element004,P_element004,S_element006,Cl_element003,K_element002]
  conduct = 2
  density = 1
  expand = 3
  formula = G4_BRAIN_ICRP
  name = G4_BRAIN_ICRP
  specific = 4
FEATURE [App::DocumentObjectGroupPython] C_element019  label="C_element : 4"  # scripted group (container) (typed FeaturePython)
  n = 4
  ref = C_element
FEATURE [App::DocumentObjectGroupPython] H_element018  label="H_element : 010"  # scripted group (container) (typed FeaturePython)
  n = 10
  ref = H_element
FEATURE [App::DocumentObjectGroupPython] G4_BUTANE  # scripted group (container) (typed FeaturePython)
  Dunit = g/cm3
  Dvalue = 0.00249343
  Group = -> [C_element019,H_element018]
  conduct = 2
  density = 1
  expand = 3
  formula = G4_BUTANE
  name = G4_BUTANE
  specific = 4
FEATURE [App::DocumentObjectGroupPython] C_element020  label="C_element : 008"  # scripted group (container) (typed FeaturePython)
  n = 4
  ref = C_element
FEATURE [App::DocumentObjectGroupPython] H_element019  label="H_element : 011"  # scripted group (container) (typed FeaturePython)
  n = 10
  ref = H_element
FEATURE [App::DocumentObjectGroupPython] O_element018  label="O_element : 007"  # scripted group (container) (typed FeaturePython)
  n = 1
  ref = O_element
FEATURE [App::DocumentObjectGroupPython] G4_N_BUTYL_ALCOHOL  label="G4_N-BUTYL_ALCOHOL"  # scripted group (container) (typed FeaturePython)
  Dunit = g/cm3
  Dvalue = 0.8098
  Group = -> [C_element020,H_element019,O_element018]
  conduct = 2
  density = 1
  expand = 3
  formula = G4_N-BUTYL_ALCOHOL
  name = G4_N-BUTYL_ALCOHOL
  specific = 4
FEATURE [App::DocumentObjectGroupPython] H_element020  label="H_element : 0.025"  # scripted group (container) (typed FeaturePython)
  n = 0.02468
FEATURE [App::DocumentObjectGroupPython] C_element021  label="C_element : 0.502"  # scripted group (container) (typed FeaturePython)
  n = 0.501611
FEATURE [App::DocumentObjectGroupPython] O_element019  label="O_element : 0.005"  # scripted group (container) (typed FeaturePython)
  n = 0.004527
FEATURE [App::DocumentObjectGroupPython] F_element004  label="F_element : 0.465"  # scripted group (container) (typed FeaturePython)
  n = 0.465209
FEATURE [App::DocumentObjectGroupPython] Si_element001  label="Si_element : 0.004"  # scripted group (container) (typed FeaturePython)
  n = 0.003973
FEATURE [App::DocumentObjectGroupPython] G4_C_552  label="G4_C-552"  # scripted group (container) (typed FeaturePython)
  Dunit = g/cm3
  Dvalue = 1.76
  Group = -> [H_element020,C_element021,O_element019,F_element004,Si_element001]
  conduct = 2
  density = 1
  expand = 3
  formula = G4_C-552
  name = G4_C-552
  specific = 4
FEATURE [App::DocumentObjectGroupPython] Cd_element001  label="Cd_element : 1"  # scripted group (container) (typed FeaturePython)
  n = 1
  ref = Cd_element
FEATURE [App::DocumentObjectGroupPython] Te_element001  label="Te_element : 1"  # scripted group (container) (typed FeaturePython)
  n = 1
  ref = Te_element
FEATURE [App::DocumentObjectGroupPython] G4_CADMIUM_TELLURIDE  # scripted group (container) (typed FeaturePython)
  Dunit = g/cm3
  Dvalue = 6.2
  Group = -> [Cd_element001,Te_element001]
  conduct = 2
  density = 1
  expand = 3
  formula = G4_CADMIUM_TELLURIDE
  name = G4_CADMIUM_TELLURIDE
  specific = 4
FEATURE [App::DocumentObjectGroupPython] Cd_element002  label="Cd_element : 002"  # scripted group (container) (typed FeaturePython)
  n = 1
  ref = Cd_element
FEATURE [App::DocumentObjectGroupPython] W_element001  label="W_element : 1"  # scripted group (container) (typed FeaturePython)
  n = 1
  ref = W_element
FEATURE [App::DocumentObjectGroupPython] O_element020  label="O_element : 008"  # scripted group (container) (typed FeaturePython)
  n = 4
  ref = O_element
FEATURE [App::DocumentObjectGroupPython] G4_CADMIUM_TUNGSTATE  # scripted group (container) (typed FeaturePython)
  Dunit = g/cm3
  Dvalue = 7.9
  Group = -> [Cd_element002,W_element001,O_element020]
  conduct = 2
  density = 1
  expand = 3
  formula = G4_CADMIUM_TUNGSTATE
  name = G4_CADMIUM_TUNGSTATE
  specific = 4
FEATURE [App::DocumentObjectGroupPython] Ca_element005  label="Ca_element : 1"  # scripted group (container) (typed FeaturePython)
  n = 1
  ref = Ca_element
FEATURE [App::DocumentObjectGroupPython] C_element022  label="C_element : 009"  # scripted group (container) (typed FeaturePython)
  n = 1
  ref = C_element
FEATURE [App::DocumentObjectGroupPython] O_element021  label="O_element : 009"  # scripted group (container) (typed FeaturePython)
  n = 3
  ref = O_element
FEATURE [App::DocumentObjectGroupPython] G4_CALCIUM_CARBONATE  # scripted group (container) (typed FeaturePython)
  Dunit = g/cm3
  Dvalue = 2.8
  Group = -> [Ca_element005,C_element022,O_element021]
  conduct = 2
  density = 1
  expand = 3
  formula = G4_CALCIUM_CARBONATE
  name = G4_CALCIUM_CARBONATE
  specific = 4
FEATURE [App::DocumentObjectGroupPython] Ca_element006  label="Ca_element : 002"  # scripted group (container) (typed FeaturePython)
  n = 1
  ref = Ca_element
FEATURE [App::DocumentObjectGroupPython] F_element005  label="F_element : 003"  # scripted group (container) (typed FeaturePython)
  n = 2
  ref = F_element
FEATURE [App::DocumentObjectGroupPython] G4_CALCIUM_FLUORIDE  # scripted group (container) (typed FeaturePython)
  Dunit = g/cm3
  Dvalue = 3.18
  Group = -> [Ca_element006,F_element005]
  conduct = 2
  density = 1
  expand = 3
  formula = G4_CALCIUM_FLUORIDE
  name = G4_CALCIUM_FLUORIDE
  specific = 4
FEATURE [App::DocumentObjectGroupPython] Ca_element007  label="Ca_element : 003"  # scripted group (container) (typed FeaturePython)
  n = 1
  ref = Ca_element
FEATURE [App::DocumentObjectGroupPython] O_element022  label="O_element : 010"  # scripted group (container) (typed FeaturePython)
  n = 1
  ref = O_element
FEATURE [App::DocumentObjectGroupPython] G4_CALCIUM_OXIDE  # scripted group (container) (typed FeaturePython)
  Dunit = g/cm3
  Dvalue = 3.3
  Group = -> [Ca_element007,O_element022]
  conduct = 2
  density = 1
  expand = 3
  formula = G4_CALCIUM_OXIDE
  name = G4_CALCIUM_OXIDE
  specific = 4
FEATURE [App::DocumentObjectGroupPython] Ca_element008  label="Ca_element : 004"  # scripted group (container) (typed FeaturePython)
  n = 1
  ref = Ca_element
FEATURE [App::DocumentObjectGroupPython] S_element007  label="S_element : 002"  # scripted group (container) (typed FeaturePython)
  n = 1
  ref = S_element
FEATURE [App::DocumentObjectGroupPython] O_element023  label="O_element : 011"  # scripted group (container) (typed FeaturePython)
  n = 4
  ref = O_element
FEATURE [App::DocumentObjectGroupPython] G4_CALCIUM_SULFATE  # scripted group (container) (typed FeaturePython)
  Dunit = g/cm3
  Dvalue = 2.96
  Group = -> [Ca_element008,S_element007,O_element023]
  conduct = 2
  density = 1
  expand = 3
  formula = G4_CALCIUM_SULFATE
  name = G4_CALCIUM_SULFATE
  specific = 4
FEATURE [App::DocumentObjectGroupPython] Ca_element009  label="Ca_element : 005"  # scripted group (container) (typed FeaturePython)
  n = 1
  ref = Ca_element
FEATURE [App::DocumentObjectGroupPython] W_element002  label="W_element : 002"  # scripted group (container) (typed FeaturePython)
  n = 1
  ref = W_element
FEATURE [App::DocumentObjectGroupPython] O_element024  label="O_element : 012"  # scripted group (container) (typed FeaturePython)
  n = 4
  ref = O_element
FEATURE [App::DocumentObjectGroupPython] G4_CALCIUM_TUNGSTATE  # scripted group (container) (typed FeaturePython)
  Dunit = g/cm3
  Dvalue = 6.062
  Group = -> [Ca_element009,W_element002,O_element024]
  conduct = 2
  density = 1
  expand = 3
  formula = G4_CALCIUM_TUNGSTATE
  name = G4_CALCIUM_TUNGSTATE
  specific = 4
FEATURE [App::DocumentObjectGroupPython] C_element023  label="C_element : 010"  # scripted group (container) (typed FeaturePython)
  n = 1
  ref = C_element
FEATURE [App::DocumentObjectGroupPython] O_element025  label="O_element : 013"  # scripted group (container) (typed FeaturePython)
  n = 2
  ref = O_element
FEATURE [App::DocumentObjectGroupPython] G4_CARBON_DIOXIDE  # scripted group (container) (typed FeaturePython)
  Dunit = g/cm3
  Dvalue = 0.00184212
  Group = -> [C_element023,O_element025]
  conduct = 2
  density = 1
  expand = 3
  formula = G4_CARBON_DIOXIDE
  name = G4_CARBON_DIOXIDE
  specific = 4
FEATURE [App::DocumentObjectGroupPython] C_element024  label="C_element : 011"  # scripted group (container) (typed FeaturePython)
  n = 1
  ref = C_element
FEATURE [App::DocumentObjectGroupPython] Cl_element004  label="Cl_element : 4"  # scripted group (container) (typed FeaturePython)
  n = 4
  ref = Cl_element
FEATURE [App::DocumentObjectGroupPython] G4_CARBON_TETRACHLORIDE  # scripted group (container) (typed FeaturePython)
  Dunit = g/cm3
  Dvalue = 1.594
  Group = -> [C_element024,Cl_element004]
  conduct = 2
  density = 1
  expand = 3
  formula = G4_CARBON_TETRACHLORIDE
  name = G4_CARBON_TETRACHLORIDE
  specific = 4
FEATURE [App::DocumentObjectGroupPython] C_element025  label="C_element : 012"  # scripted group (container) (typed FeaturePython)
  n = 6
  ref = C_element
FEATURE [App::DocumentObjectGroupPython] H_element021  label="H_element : 012"  # scripted group (container) (typed FeaturePython)
  n = 10
  ref = H_element
FEATURE [App::DocumentObjectGroupPython] O_element026  label="O_element : 5"  # scripted group (container) (typed FeaturePython)
  n = 5
  ref = O_element
FEATURE [App::DocumentObjectGroupPython] G4_CELLULOSE_CELLOPHANE  # scripted group (container) (typed FeaturePython)
  Dunit = g/cm3
  Dvalue = 1.42
  Group = -> [C_element025,H_element021,O_element026]
  conduct = 2
  density = 1
  expand = 3
  formula = G4_CELLULOSE_CELLOPHANE
  name = G4_CELLULOSE_CELLOPHANE
  specific = 4
FEATURE [App::DocumentObjectGroupPython] H_element022  label="H_element : 0.067"  # scripted group (container) (typed FeaturePython)
  n = 0.067125
FEATURE [App::DocumentObjectGroupPython] C_element026  label="C_element : 0.545"  # scripted group (container) (typed FeaturePython)
  n = 0.545403
FEATURE [App::DocumentObjectGroupPython] O_element027  label="O_element : 0.387"  # scripted group (container) (typed FeaturePython)
  n = 0.387472
FEATURE [App::DocumentObjectGroupPython] G4_CELLULOSE_BUTYRATE  # scripted group (container) (typed FeaturePython)
  Dunit = g/cm3
  Dvalue = 1.2
  Group = -> [H_element022,C_element026,O_element027]
  conduct = 2
  density = 1
  expand = 3
  formula = G4_CELLULOSE_BUTYRATE
  name = G4_CELLULOSE_BUTYRATE
  specific = 4
FEATURE [App::DocumentObjectGroupPython] H_element023  label="H_element : 0.029"  # scripted group (container) (typed FeaturePython)
  n = 0.029216
FEATURE [App::DocumentObjectGroupPython] C_element027  label="C_element : 0.271"  # scripted group (container) (typed FeaturePython)
  n = 0.271296
FEATURE [App::DocumentObjectGroupPython] N_element013  label="N_element : 0.121"  # scripted group (container) (typed FeaturePython)
  n = 0.121276
FEATURE [App::DocumentObjectGroupPython] O_element028  label="O_element : 0.578"  # scripted group (container) (typed FeaturePython)
  n = 0.578212
FEATURE [App::DocumentObjectGroupPython] G4_CELLULOSE_NITRATE  # scripted group (container) (typed FeaturePython)
  Dunit = g/cm3
  Dvalue = 1.49
  Group = -> [H_element023,C_element027,N_element013,O_element028]
  conduct = 2
  density = 1
  expand = 3
  formula = G4_CELLULOSE_NITRATE
  name = G4_CELLULOSE_NITRATE
  specific = 4
FEATURE [App::DocumentObjectGroupPython] H_element024  label="H_element : 0.108"  # scripted group (container) (typed FeaturePython)
  n = 0.107596
FEATURE [App::DocumentObjectGroupPython] N_element014  label="N_element : 0.001"  # scripted group (container) (typed FeaturePython)
  n = 0.0008
FEATURE [App::DocumentObjectGroupPython] O_element029  label="O_element : 0.875"  # scripted group (container) (typed FeaturePython)
  n = 0.874976
FEATURE [App::DocumentObjectGroupPython] S_element008  label="S_element : 0.015"  # scripted group (container) (typed FeaturePython)
  n = 0.014627
FEATURE [App::DocumentObjectGroupPython] Ce_element001  label="Ce_element : 0.002"  # scripted group (container) (typed FeaturePython)
  n = 0.002001
FEATURE [App::DocumentObjectGroupPython] G4_CERIC_SULFATE  # scripted group (container) (typed FeaturePython)
  Dunit = g/cm3
  Dvalue = 1.03
  Group = -> [H_element024,N_element014,O_element029,S_element008,Ce_element001]
  conduct = 2
  density = 1
  expand = 3
  formula = G4_CERIC_SULFATE
  name = G4_CERIC_SULFATE
  specific = 4
FEATURE [App::DocumentObjectGroupPython] Cs_element001  label="Cs_element : 1"  # scripted group (container) (typed FeaturePython)
  n = 1
  ref = Cs_element
FEATURE [App::DocumentObjectGroupPython] F_element006  label="F_element : 1"  # scripted group (container) (typed FeaturePython)
  n = 1
  ref = F_element
FEATURE [App::DocumentObjectGroupPython] G4_CESIUM_FLUORIDE  # scripted group (container) (typed FeaturePython)
  Dunit = g/cm3
  Dvalue = 4.115
  Group = -> [Cs_element001,F_element006]
  conduct = 2
  density = 1
  expand = 3
  formula = G4_CESIUM_FLUORIDE
  name = G4_CESIUM_FLUORIDE
  specific = 4
FEATURE [App::DocumentObjectGroupPython] Cs_element002  label="Cs_element : 002"  # scripted group (container) (typed FeaturePython)
  n = 1
  ref = Cs_element
FEATURE [App::DocumentObjectGroupPython] I_element001  label="I_element : 1"  # scripted group (container) (typed FeaturePython)
  n = 1
  ref = I_element
FEATURE [App::DocumentObjectGroupPython] G4_CESIUM_IODIDE  # scripted group (container) (typed FeaturePython)
  Dunit = g/cm3
  Dvalue = 4.51
  Group = -> [Cs_element002,I_element001]
  conduct = 2
  density = 1
  expand = 3
  formula = G4_CESIUM_IODIDE
  name = G4_CESIUM_IODIDE
  specific = 4
FEATURE [App::DocumentObjectGroupPython] C_element028  label="C_element : 013"  # scripted group (container) (typed FeaturePython)
  n = 6
  ref = C_element
FEATURE [App::DocumentObjectGroupPython] H_element025  label="H_element : 013"  # scripted group (container) (typed FeaturePython)
  n = 5
  ref = H_element
FEATURE [App::DocumentObjectGroupPython] Cl_element005  label="Cl_element : 1"  # scripted group (container) (typed FeaturePython)
  n = 1
  ref = Cl_element
FEATURE [App::DocumentObjectGroupPython] G4_CHLOROBENZENE  # scripted group (container) (typed FeaturePython)
  Dunit = g/cm3
  Dvalue = 1.1058
  Group = -> [C_element028,H_element025,Cl_element005]
  conduct = 2
  density = 1
  expand = 3
  formula = G4_CHLOROBENZENE
  name = G4_CHLOROBENZENE
  specific = 4
FEATURE [App::DocumentObjectGroupPython] C_element029  label="C_element : 014"  # scripted group (container) (typed FeaturePython)
  n = 1
  ref = C_element
FEATURE [App::DocumentObjectGroupPython] H_element026  label="H_element : 1"  # scripted group (container) (typed FeaturePython)
  n = 1
  ref = H_element
FEATURE [App::DocumentObjectGroupPython] Cl_element006  label="Cl_element : 3"  # scripted group (container) (typed FeaturePython)
  n = 3
  ref = Cl_element
FEATURE [App::DocumentObjectGroupPython] G4_CHLOROFORM  # scripted group (container) (typed FeaturePython)
  Dunit = g/cm3
  Dvalue = 1.4832
  Group = -> [C_element029,H_element026,Cl_element006]
  conduct = 2
  density = 1
  expand = 3
  formula = G4_CHLOROFORM
  name = G4_CHLOROFORM
  specific = 4
FEATURE [App::DocumentObjectGroupPython] H_element027  label="H_element : 0.010"  # scripted group (container) (typed FeaturePython)
  n = 0.01
FEATURE [App::DocumentObjectGroupPython] C_element030  label="C_element : 0.001"  # scripted group (container) (typed FeaturePython)
  n = 0.001
FEATURE [App::DocumentObjectGroupPython] O_element030  label="O_element : 0.529"  # scripted group (container) (typed FeaturePython)
  n = 0.529107
FEATURE [App::DocumentObjectGroupPython] Na_element005  label="Na_element : 0.016"  # scripted group (container) (typed FeaturePython)
  n = 0.016
FEATURE [App::DocumentObjectGroupPython] Mg_element003  label="Mg_element : 0.004"  # scripted group (container) (typed FeaturePython)
  n = 0.002
FEATURE [App::DocumentObjectGroupPython] Al_element002  label="Al_element : 0.034"  # scripted group (container) (typed FeaturePython)
  n = 0.033872
FEATURE [App::DocumentObjectGroupPython] Si_element002  label="Si_element : 0.337"  # scripted group (container) (typed FeaturePython)
  n = 0.337021
FEATURE [App::DocumentObjectGroupPython] K_element003  label="K_element : 0.013"  # scripted group (container) (typed FeaturePython)
  n = 0.013
FEATURE [App::DocumentObjectGroupPython] Ca_element010  label="Ca_element : 0.044"  # scripted group (container) (typed FeaturePython)
  n = 0.044
FEATURE [App::DocumentObjectGroupPython] Fe_element002  label="Fe_element : 0.014"  # scripted group (container) (typed FeaturePython)
  n = 0.014
FEATURE [App::DocumentObjectGroupPython] G4_CONCRETE  # scripted group (container) (typed FeaturePython)
  Dunit = g/cm3
  Dvalue = 2.3
  Group = -> [H_element027,C_element030,O_element030,Na_element005,Mg_element003,Al_element002,Si_element002,K_element003,Ca_element010,Fe_element002]
  conduct = 2
  density = 1
  expand = 3
  formula = G4_CONCRETE
  name = G4_CONCRETE
  specific = 4
FEATURE [App::DocumentObjectGroupPython] C_element031  label="C_element : 015"  # scripted group (container) (typed FeaturePython)
  n = 6
  ref = C_element
FEATURE [App::DocumentObjectGroupPython] H_element028  label="H_element : 12"  # scripted group (container) (typed FeaturePython)
  n = 12
  ref = H_element
FEATURE [App::DocumentObjectGroupPython] G4_CYCLOHEXANE  # scripted group (container) (typed FeaturePython)
  Dunit = g/cm3
  Dvalue = 0.779
  Group = -> [C_element031,H_element028]
  conduct = 2
  density = 1
  expand = 3
  formula = G4_CYCLOHEXANE
  name = G4_CYCLOHEXANE
  specific = 4
FEATURE [App::DocumentObjectGroupPython] C_element032  label="C_element : 016"  # scripted group (container) (typed FeaturePython)
  n = 6
  ref = C_element
FEATURE [App::DocumentObjectGroupPython] H_element029  label="H_element : 4"  # scripted group (container) (typed FeaturePython)
  n = 4
  ref = H_element
FEATURE [App::DocumentObjectGroupPython] Cl_element007  label="Cl_element : 2"  # scripted group (container) (typed FeaturePython)
  n = 2
  ref = Cl_element
FEATURE [App::DocumentObjectGroupPython] G4_1_2_DICHLOROBENZENE  label="G4_1.2-DICHLOROBENZENE"  # scripted group (container) (typed FeaturePython)
  Dunit = g/cm3
  Dvalue = 1.3048
  Group = -> [C_element032,H_element029,Cl_element007]
  conduct = 2
  density = 1
  expand = 3
  formula = G4_1.2-DICHLOROBENZENE
  name = G4_1.2-DICHLOROBENZENE
  specific = 4
FEATURE [App::DocumentObjectGroupPython] C_element033  label="C_element : 017"  # scripted group (container) (typed FeaturePython)
  n = 4
  ref = C_element
FEATURE [App::DocumentObjectGroupPython] H_element030  label="H_element : 8"  # scripted group (container) (typed FeaturePython)
  n = 8
  ref = H_element
FEATURE [App::DocumentObjectGroupPython] O_element031  label="O_element : 014"  # scripted group (container) (typed FeaturePython)
  n = 1
  ref = O_element
FEATURE [App::DocumentObjectGroupPython] Cl_element008  label="Cl_element : 005"  # scripted group (container) (typed FeaturePython)
  n = 2
  ref = Cl_element
FEATURE [App::DocumentObjectGroupPython] G4_DICHLORODIETHYL_ETHER  # scripted group (container) (typed FeaturePython)
  Dunit = g/cm3
  Dvalue = 1.2199
  Group = -> [C_element033,H_element030,O_element031,Cl_element008]
  conduct = 2
  density = 1
  expand = 3
  formula = G4_DICHLORODIETHYL_ETHER
  name = G4_DICHLORODIETHYL_ETHER
  specific = 4
FEATURE [App::DocumentObjectGroupPython] C_element034  label="C_element : 018"  # scripted group (container) (typed FeaturePython)
  n = 2
  ref = C_element
FEATURE [App::DocumentObjectGroupPython] H_element031  label="H_element : 014"  # scripted group (container) (typed FeaturePython)
  n = 4
  ref = H_element
FEATURE [App::DocumentObjectGroupPython] Cl_element009  label="Cl_element : 006"  # scripted group (container) (typed FeaturePython)
  n = 2
  ref = Cl_element
FEATURE [App::DocumentObjectGroupPython] G4_1_2_DICHLOROETHANE  label="G4_1.2-DICHLOROETHANE"  # scripted group (container) (typed FeaturePython)
  Dunit = g/cm3
  Dvalue = 1.2351
  Group = -> [C_element034,H_element031,Cl_element009]
  conduct = 2
  density = 1
  expand = 3
  formula = G4_1.2-DICHLOROETHANE
  name = G4_1.2-DICHLOROETHANE
  specific = 4
FEATURE [App::DocumentObjectGroupPython] C_element035  label="C_element : 019"  # scripted group (container) (typed FeaturePython)
  n = 4
  ref = C_element
FEATURE [App::DocumentObjectGroupPython] H_element032  label="H_element : 015"  # scripted group (container) (typed FeaturePython)
  n = 10
  ref = H_element
FEATURE [App::DocumentObjectGroupPython] O_element032  label="O_element : 015"  # scripted group (container) (typed FeaturePython)
  n = 1
  ref = O_element
FEATURE [App::DocumentObjectGroupPython] G4_DIETHYL_ETHER  # scripted group (container) (typed FeaturePython)
  Dunit = g/cm3
  Dvalue = 0.71378
  Group = -> [C_element035,H_element032,O_element032]
  conduct = 2
  density = 1
  expand = 3
  formula = G4_DIETHYL_ETHER
  name = G4_DIETHYL_ETHER
  specific = 4
FEATURE [App::DocumentObjectGroupPython] C_element036  label="C_element : 020"  # scripted group (container) (typed FeaturePython)
  n = 3
  ref = C_element
FEATURE [App::DocumentObjectGroupPython] H_element033  label="H_element : 016"  # scripted group (container) (typed FeaturePython)
  n = 7
  ref = H_element
FEATURE [App::DocumentObjectGroupPython] N_element015  label="N_element : 008"  # scripted group (container) (typed FeaturePython)
  n = 1
  ref = N_element
FEATURE [App::DocumentObjectGroupPython] O_element033  label="O_element : 016"  # scripted group (container) (typed FeaturePython)
  n = 1
  ref = O_element
FEATURE [App::DocumentObjectGroupPython] G4_N_N_DIMETHYL_FORMAMIDE  label="G4_N.N-DIMETHYL_FORMAMIDE"  # scripted group (container) (typed FeaturePython)
  Dunit = g/cm3
  Dvalue = 0.9487
  Group = -> [C_element036,H_element033,N_element015,O_element033]
  conduct = 2
  density = 1
  expand = 3
  formula = G4_N.N-DIMETHYL_FORMAMIDE
  name = G4_N.N-DIMETHYL_FORMAMIDE
  specific = 4
FEATURE [App::DocumentObjectGroupPython] C_element037  label="C_element : 021"  # scripted group (container) (typed FeaturePython)
  n = 2
  ref = C_element
FEATURE [App::DocumentObjectGroupPython] H_element034  label="H_element : 017"  # scripted group (container) (typed FeaturePython)
  n = 6
  ref = H_element
FEATURE [App::DocumentObjectGroupPython] O_element034  label="O_element : 017"  # scripted group (container) (typed FeaturePython)
  n = 1
  ref = O_element
FEATURE [App::DocumentObjectGroupPython] S_element009  label="S_element : 003"  # scripted group (container) (typed FeaturePython)
  n = 1
  ref = S_element
FEATURE [App::DocumentObjectGroupPython] G4_DIMETHYL_SULFOXIDE  # scripted group (container) (typed FeaturePython)
  Dunit = g/cm3
  Dvalue = 1.1014
  Group = -> [C_element037,H_element034,O_element034,S_element009]
  conduct = 2
  density = 1
  expand = 3
  formula = G4_DIMETHYL_SULFOXIDE
  name = G4_DIMETHYL_SULFOXIDE
  specific = 4
FEATURE [App::DocumentObjectGroupPython] C_element038  label="C_element : 022"  # scripted group (container) (typed FeaturePython)
  n = 2
  ref = C_element
FEATURE [App::DocumentObjectGroupPython] H_element035  label="H_element : 018"  # scripted group (container) (typed FeaturePython)
  n = 6
  ref = H_element
FEATURE [App::DocumentObjectGroupPython] G4_ETHANE  # scripted group (container) (typed FeaturePython)
  Dunit = g/cm3
  Dvalue = 0.00125324
  Group = -> [C_element038,H_element035]
  conduct = 2
  density = 1
  expand = 3
  formula = G4_ETHANE
  name = G4_ETHANE
  specific = 4
FEATURE [App::DocumentObjectGroupPython] C_element039  label="C_element : 023"  # scripted group (container) (typed FeaturePython)
  n = 2
  ref = C_element
FEATURE [App::DocumentObjectGroupPython] H_element036  label="H_element : 019"  # scripted group (container) (typed FeaturePython)
  n = 6
  ref = H_element
FEATURE [App::DocumentObjectGroupPython] O_element035  label="O_element : 018"  # scripted group (container) (typed FeaturePython)
  n = 1
  ref = O_element
FEATURE [App::DocumentObjectGroupPython] G4_ETHYL_ALCOHOL  # scripted group (container) (typed FeaturePython)
  Dunit = g/cm3
  Dvalue = 0.7893
  Group = -> [C_element039,H_element036,O_element035]
  conduct = 2
  density = 1
  expand = 3
  formula = G4_ETHYL_ALCOHOL
  name = G4_ETHYL_ALCOHOL
  specific = 4
FEATURE [App::DocumentObjectGroupPython] H_element037  label="H_element : 0.090"  # scripted group (container) (typed FeaturePython)
  n = 0.090027
FEATURE [App::DocumentObjectGroupPython] C_element040  label="C_element : 0.585"  # scripted group (container) (typed FeaturePython)
  n = 0.585182
FEATURE [App::DocumentObjectGroupPython] O_element036  label="O_element : 0.325"  # scripted group (container) (typed FeaturePython)
  n = 0.324791
FEATURE [App::DocumentObjectGroupPython] G4_ETHYL_CELLULOSE  # scripted group (container) (typed FeaturePython)
  Dunit = g/cm3
  Dvalue = 1.13
  Group = -> [H_element037,C_element040,O_element036]
  conduct = 2
  density = 1
  expand = 3
  formula = G4_ETHYL_CELLULOSE
  name = G4_ETHYL_CELLULOSE
  specific = 4
FEATURE [App::DocumentObjectGroupPython] C_element041  label="C_element : 024"  # scripted group (container) (typed FeaturePython)
  n = 2
  ref = C_element
FEATURE [App::DocumentObjectGroupPython] H_element038  label="H_element : 020"  # scripted group (container) (typed FeaturePython)
  n = 4
  ref = H_element
FEATURE [App::DocumentObjectGroupPython] G4_ETHYLENE  # scripted group (container) (typed FeaturePython)
  Dunit = g/cm3
  Dvalue = 0.00117497
  Group = -> [C_element041,H_element038]
  conduct = 2
  density = 1
  expand = 3
  formula = G4_ETHYLENE
  name = G4_ETHYLENE
  specific = 4
FEATURE [App::DocumentObjectGroupPython] H_element039  label="H_element : 0.096"  # scripted group (container) (typed FeaturePython)
  n = 0.096
FEATURE [App::DocumentObjectGroupPython] C_element042  label="C_element : 0.195"  # scripted group (container) (typed FeaturePython)
  n = 0.195
FEATURE [App::DocumentObjectGroupPython] N_element016  label="N_element : 0.057"  # scripted group (container) (typed FeaturePython)
  n = 0.057
FEATURE [App::DocumentObjectGroupPython] O_element037  label="O_element : 0.646"  # scripted group (container) (typed FeaturePython)
  n = 0.646
FEATURE [App::DocumentObjectGroupPython] Na_element006  label="Na_element : 0.017"  # scripted group (container) (typed FeaturePython)
  n = 0.001
FEATURE [App::DocumentObjectGroupPython] P_element005  label="P_element : 0.104"  # scripted group (container) (typed FeaturePython)
  n = 0.001
FEATURE [App::DocumentObjectGroupPython] S_element010  label="S_element : 0.016"  # scripted group (container) (typed FeaturePython)
  n = 0.003
FEATURE [App::DocumentObjectGroupPython] Cl_element010  label="Cl_element : 0.005"  # scripted group (container) (typed FeaturePython)
  n = 0.001
FEATURE [App::DocumentObjectGroupPython] G4_EYE_LENS_ICRP  # scripted group (container) (typed FeaturePython)
  Dunit = g/cm3
  Dvalue = 1.07
  Group = -> [H_element039,C_element042,N_element016,O_element037,Na_element006,P_element005,S_element010,Cl_element010]
  conduct = 2
  density = 1
  expand = 3
  formula = G4_EYE_LENS_ICRP
  name = G4_EYE_LENS_ICRP
  specific = 4
FEATURE [App::DocumentObjectGroupPython] Fe_element003  label="Fe_element : 2"  # scripted group (container) (typed FeaturePython)
  n = 2
  ref = Fe_element
FEATURE [App::DocumentObjectGroupPython] O_element038  label="O_element : 019"  # scripted group (container) (typed FeaturePython)
  n = 3
  ref = O_element
FEATURE [App::DocumentObjectGroupPython] G4_FERRIC_OXIDE  # scripted group (container) (typed FeaturePython)
  Dunit = g/cm3
  Dvalue = 5.2
  Group = -> [Fe_element003,O_element038]
  conduct = 2
  density = 1
  expand = 3
  formula = G4_FERRIC_OXIDE
  name = G4_FERRIC_OXIDE
  specific = 4
FEATURE [App::DocumentObjectGroupPython] Fe_element004  label="Fe_element : 1"  # scripted group (container) (typed FeaturePython)
  n = 1
  ref = Fe_element
FEATURE [App::DocumentObjectGroupPython] B_element003  label="B_element : 1"  # scripted group (container) (typed FeaturePython)
  n = 1
  ref = B_element
FEATURE [App::DocumentObjectGroupPython] G4_FERROBORIDE  # scripted group (container) (typed FeaturePython)
  Dunit = g/cm3
  Dvalue = 7.15
  Group = -> [Fe_element004,B_element003]
  conduct = 2
  density = 1
  expand = 3
  formula = G4_FERROBORIDE
  name = G4_FERROBORIDE
  specific = 4
FEATURE [App::DocumentObjectGroupPython] Fe_element005  label="Fe_element : 003"  # scripted group (container) (typed FeaturePython)
  n = 1
  ref = Fe_element
FEATURE [App::DocumentObjectGroupPython] O_element039  label="O_element : 020"  # scripted group (container) (typed FeaturePython)
  n = 1
  ref = O_element
FEATURE [App::DocumentObjectGroupPython] G4_FERROUS_OXIDE  # scripted group (container) (typed FeaturePython)
  Dunit = g/cm3
  Dvalue = 5.7
  Group = -> [Fe_element005,O_element039]
  conduct = 2
  density = 1
  expand = 3
  formula = G4_FERROUS_OXIDE
  name = G4_FERROUS_OXIDE
  specific = 4
FEATURE [App::DocumentObjectGroupPython] H_element040  label="H_element : 0.115"  # scripted group (container) (typed FeaturePython)
  n = 0.108259
FEATURE [App::DocumentObjectGroupPython] N_element017  label="N_element : 0.000"  # scripted group (container) (typed FeaturePython)
  n = 2.7e-05
FEATURE [App::DocumentObjectGroupPython] O_element040  label="O_element : 0.879"  # scripted group (container) (typed FeaturePython)
  n = 0.878636
FEATURE [App::DocumentObjectGroupPython] Na_element007  label="Na_element : 0.000"  # scripted group (container) (typed FeaturePython)
  n = 2.2e-05
FEATURE [App::DocumentObjectGroupPython] S_element011  label="S_element : 0.013"  # scripted group (container) (typed FeaturePython)
  n = 0.012968
FEATURE [App::DocumentObjectGroupPython] Cl_element011  label="Cl_element : 0.000"  # scripted group (container) (typed FeaturePython)
  n = 3.4e-05
FEATURE [App::DocumentObjectGroupPython] Fe_element006  label="Fe_element : 0.000"  # scripted group (container) (typed FeaturePython)
  n = 5.4e-05
FEATURE [App::DocumentObjectGroupPython] G4_FERROUS_SULFATE  # scripted group (container) (typed FeaturePython)
  Dunit = g/cm3
  Dvalue = 1.024
  Group = -> [H_element040,N_element017,O_element040,Na_element007,S_element011,Cl_element011,Fe_element006]
  conduct = 2
  density = 1
  expand = 3
  formula = G4_FERROUS_SULFATE
  name = G4_FERROUS_SULFATE
  specific = 4
FEATURE [App::DocumentObjectGroupPython] C_element043  label="C_element : 0.099"  # scripted group (container) (typed FeaturePython)
  n = 0.099335
FEATURE [App::DocumentObjectGroupPython] F_element007  label="F_element : 0.314"  # scripted group (container) (typed FeaturePython)
  n = 0.314247
FEATURE [App::DocumentObjectGroupPython] Cl_element012  label="Cl_element : 0.586"  # scripted group (container) (typed FeaturePython)
  n = 0.586418
FEATURE [App::DocumentObjectGroupPython] G4_FREON_12  label="G4_FREON-12"  # scripted group (container) (typed FeaturePython)
  Dunit = g/cm3
  Dvalue = 1.12
  Group = -> [C_element043,F_element007,Cl_element012]
  conduct = 2
  density = 1
  expand = 3
  formula = G4_FREON-12
  name = G4_FREON-12
  specific = 4
FEATURE [App::DocumentObjectGroupPython] C_element044  label="C_element : 0.057"  # scripted group (container) (typed FeaturePython)
  n = 0.057245
FEATURE [App::DocumentObjectGroupPython] F_element008  label="F_element : 0.181"  # scripted group (container) (typed FeaturePython)
  n = 0.181096
FEATURE [App::DocumentObjectGroupPython] Br_element001  label="Br_element : 0.762"  # scripted group (container) (typed FeaturePython)
  n = 0.761659
FEATURE [App::DocumentObjectGroupPython] G4_FREON_12B2  label="G4_FREON-12B2"  # scripted group (container) (typed FeaturePython)
  Dunit = g/cm3
  Dvalue = 1.8
  Group = -> [C_element044,F_element008,Br_element001]
  conduct = 2
  density = 1
  expand = 3
  formula = G4_FREON-12B2
  name = G4_FREON-12B2
  specific = 4
FEATURE [App::DocumentObjectGroupPython] C_element045  label="C_element : 0.115"  # scripted group (container) (typed FeaturePython)
  n = 0.114983
FEATURE [App::DocumentObjectGroupPython] F_element009  label="F_element : 0.546"  # scripted group (container) (typed FeaturePython)
  n = 0.545621
FEATURE [App::DocumentObjectGroupPython] Cl_element013  label="Cl_element : 0.339"  # scripted group (container) (typed FeaturePython)
  n = 0.339396
FEATURE [App::DocumentObjectGroupPython] G4_FREON_13  label="G4_FREON-13"  # scripted group (container) (typed FeaturePython)
  Dunit = g/cm3
  Dvalue = 0.95
  Group = -> [C_element045,F_element009,Cl_element013]
  conduct = 2
  density = 1
  expand = 3
  formula = G4_FREON-13
  name = G4_FREON-13
  specific = 4
FEATURE [App::DocumentObjectGroupPython] C_element046  label="C_element : 025"  # scripted group (container) (typed FeaturePython)
  n = 1
  ref = C_element
FEATURE [App::DocumentObjectGroupPython] F_element010  label="F_element : 3"  # scripted group (container) (typed FeaturePython)
  n = 3
  ref = F_element
FEATURE [App::DocumentObjectGroupPython] Br_element002  label="Br_element : 1"  # scripted group (container) (typed FeaturePython)
  n = 1
  ref = Br_element
FEATURE [App::DocumentObjectGroupPython] G4_FREON_13B1  label="G4_FREON-13B1"  # scripted group (container) (typed FeaturePython)
  Dunit = g/cm3
  Dvalue = 1.5
  Group = -> [C_element046,F_element010,Br_element002]
  conduct = 2
  density = 1
  expand = 3
  formula = G4_FREON-13B1
  name = G4_FREON-13B1
  specific = 4
FEATURE [App::DocumentObjectGroupPython] C_element047  label="C_element : 0.061"  # scripted group (container) (typed FeaturePython)
  n = 0.061309
FEATURE [App::DocumentObjectGroupPython] F_element011  label="F_element : 0.291"  # scripted group (container) (typed FeaturePython)
  n = 0.290924
FEATURE [App::DocumentObjectGroupPython] I_element002  label="I_element : 0.648"  # scripted group (container) (typed FeaturePython)
  n = 0.647767
FEATURE [App::DocumentObjectGroupPython] G4_FREON_13I1  label="G4_FREON-13I1"  # scripted group (container) (typed FeaturePython)
  Dunit = g/cm3
  Dvalue = 1.8
  Group = -> [C_element047,F_element011,I_element002]
  conduct = 2
  density = 1
  expand = 3
  formula = G4_FREON-13I1
  name = G4_FREON-13I1
  specific = 4
FEATURE [App::DocumentObjectGroupPython] Gd_element001  label="Gd_element : 2"  # scripted group (container) (typed FeaturePython)
  n = 2
  ref = Gd_element
FEATURE [App::DocumentObjectGroupPython] O_element041  label="O_element : 021"  # scripted group (container) (typed FeaturePython)
  n = 2
  ref = O_element
FEATURE [App::DocumentObjectGroupPython] S_element012  label="S_element : 004"  # scripted group (container) (typed FeaturePython)
  n = 1
  ref = S_element
FEATURE [App::DocumentObjectGroupPython] G4_GADOLINIUM_OXYSULFIDE  # scripted group (container) (typed FeaturePython)
  Dunit = g/cm3
  Dvalue = 7.44
  Group = -> [Gd_element001,O_element041,S_element012]
  conduct = 2
  density = 1
  expand = 3
  formula = G4_GADOLINIUM_OXYSULFIDE
  name = G4_GADOLINIUM_OXYSULFIDE
  specific = 4
FEATURE [App::DocumentObjectGroupPython] Ga_element001  label="Ga_element : 1"  # scripted group (container) (typed FeaturePython)
  n = 1
  ref = Ga_element
FEATURE [App::DocumentObjectGroupPython] As_element001  label="As_element : 1"  # scripted group (container) (typed FeaturePython)
  n = 1
  ref = As_element
FEATURE [App::DocumentObjectGroupPython] G4_GALLIUM_ARSENIDE  # scripted group (container) (typed FeaturePython)
  Dunit = g/cm3
  Dvalue = 5.31
  Group = -> [Ga_element001,As_element001]
  conduct = 2
  density = 1
  expand = 3
  formula = G4_GALLIUM_ARSENIDE
  name = G4_GALLIUM_ARSENIDE
  specific = 4
FEATURE [App::DocumentObjectGroupPython] H_element041  label="H_element : 0.081"  # scripted group (container) (typed FeaturePython)
  n = 0.08118
FEATURE [App::DocumentObjectGroupPython] C_element048  label="C_element : 0.416"  # scripted group (container) (typed FeaturePython)
  n = 0.41606
FEATURE [App::DocumentObjectGroupPython] N_element018  label="N_element : 0.111"  # scripted group (container) (typed FeaturePython)
  n = 0.11124
FEATURE [App::DocumentObjectGroupPython] O_element042  label="O_element : 0.381"  # scripted group (container) (typed FeaturePython)
  n = 0.38064
FEATURE [App::DocumentObjectGroupPython] S_element013  label="S_element : 0.011"  # scripted group (container) (typed FeaturePython)
  n = 0.01088
FEATURE [App::DocumentObjectGroupPython] G4_GEL_PHOTO_EMULSION  # scripted group (container) (typed FeaturePython)
  Dunit = g/cm3
  Dvalue = 1.2914
  Group = -> [H_element041,C_element048,N_element018,O_element042,S_element013]
  conduct = 2
  density = 1
  expand = 3
  formula = G4_GEL_PHOTO_EMULSION
  name = G4_GEL_PHOTO_EMULSION
  specific = 4
FEATURE [App::DocumentObjectGroupPython] B_element004  label="B_element : 0.040"  # scripted group (container) (typed FeaturePython)
  n = 0.0400639
FEATURE [App::DocumentObjectGroupPython] O_element043  label="O_element : 0.540"  # scripted group (container) (typed FeaturePython)
  n = 0.539561
FEATURE [App::DocumentObjectGroupPython] Na_element008  label="Na_element : 0.028"  # scripted group (container) (typed FeaturePython)
  n = 0.0281909
FEATURE [App::DocumentObjectGroupPython] Al_element003  label="Al_element : 0.012"  # scripted group (container) (typed FeaturePython)
  n = 0.011644
FEATURE [App::DocumentObjectGroupPython] Si_element003  label="Si_element : 0.377"  # scripted group (container) (typed FeaturePython)
  n = 0.377219
FEATURE [App::DocumentObjectGroupPython] K_element004  label="K_element : 0.014"  # scripted group (container) (typed FeaturePython)
  n = 0.00332099
FEATURE [App::DocumentObjectGroupPython] G4_Pyrex_Glass  # scripted group (container) (typed FeaturePython)
  Dunit = g/cm3
  Dvalue = 2.23
  Group = -> [B_element004,O_element043,Na_element008,Al_element003,Si_element003,K_element004]
  conduct = 2
  density = 1
  expand = 3
  formula = G4_Pyrex_Glass
  name = G4_Pyrex_Glass
  specific = 4
FEATURE [App::DocumentObjectGroupPython] O_element044  label="O_element : 0.156"  # scripted group (container) (typed FeaturePython)
  n = 0.156453
FEATURE [App::DocumentObjectGroupPython] Si_element004  label="Si_element : 0.081"  # scripted group (container) (typed FeaturePython)
  n = 0.080866
FEATURE [App::DocumentObjectGroupPython] Ti_element001  label="Ti_element : 0.008"  # scripted group (container) (typed FeaturePython)
  n = 0.008092
FEATURE [App::DocumentObjectGroupPython] As_element002  label="As_element : 0.003"  # scripted group (container) (typed FeaturePython)
  n = 0.002651
FEATURE [App::DocumentObjectGroupPython] Pb_element001  label="Pb_element : 0.752"  # scripted group (container) (typed FeaturePython)
  n = 0.751938
FEATURE [App::DocumentObjectGroupPython] G4_GLASS_LEAD  # scripted group (container) (typed FeaturePython)
  Dunit = g/cm3
  Dvalue = 6.22
  Group = -> [O_element044,Si_element004,Ti_element001,As_element002,Pb_element001]
  conduct = 2
  density = 1
  expand = 3
  formula = G4_GLASS_LEAD
  name = G4_GLASS_LEAD
  specific = 4
FEATURE [App::DocumentObjectGroupPython] O_element045  label="O_element : 0.460"  # scripted group (container) (typed FeaturePython)
  n = 0.4598
FEATURE [App::DocumentObjectGroupPython] Na_element009  label="Na_element : 0.096"  # scripted group (container) (typed FeaturePython)
  n = 0.0964411
FEATURE [App::DocumentObjectGroupPython] Si_element005  label="Si_element : 0.378"  # scripted group (container) (typed FeaturePython)
  n = 0.336553
FEATURE [App::DocumentObjectGroupPython] Ca_element011  label="Ca_element : 0.107"  # scripted group (container) (typed FeaturePython)
  n = 0.107205
FEATURE [App::DocumentObjectGroupPython] G4_GLASS_PLATE  # scripted group (container) (typed FeaturePython)
  Dunit = g/cm3
  Dvalue = 2.4
  Group = -> [O_element045,Na_element009,Si_element005,Ca_element011]
  conduct = 2
  density = 1
  expand = 3
  formula = G4_GLASS_PLATE
  name = G4_GLASS_PLATE
  specific = 4
FEATURE [App::DocumentObjectGroupPython] C_element049  label="C_element : 026"  # scripted group (container) (typed FeaturePython)
  n = 5
  ref = C_element
FEATURE [App::DocumentObjectGroupPython] H_element042  label="H_element : 021"  # scripted group (container) (typed FeaturePython)
  n = 10
  ref = H_element
FEATURE [App::DocumentObjectGroupPython] N_element019  label="N_element : 2"  # scripted group (container) (typed FeaturePython)
  n = 2
  ref = N_element
FEATURE [App::DocumentObjectGroupPython] O_element046  label="O_element : 022"  # scripted group (container) (typed FeaturePython)
  n = 3
  ref = O_element
FEATURE [App::DocumentObjectGroupPython] G4_GLUTAMINE  # scripted group (container) (typed FeaturePython)
  Dunit = g/cm3
  Dvalue = 1.46
  Group = -> [C_element049,H_element042,N_element019,O_element046]
  conduct = 2
  density = 1
  expand = 3
  formula = G4_GLUTAMINE
  name = G4_GLUTAMINE
  specific = 4
FEATURE [App::DocumentObjectGroupPython] C_element050  label="C_element : 027"  # scripted group (container) (typed FeaturePython)
  n = 3
  ref = C_element
FEATURE [App::DocumentObjectGroupPython] H_element043  label="H_element : 022"  # scripted group (container) (typed FeaturePython)
  n = 8
  ref = H_element
FEATURE [App::DocumentObjectGroupPython] O_element047  label="O_element : 023"  # scripted group (container) (typed FeaturePython)
  n = 3
  ref = O_element
FEATURE [App::DocumentObjectGroupPython] G4_GLYCEROL  # scripted group (container) (typed FeaturePython)
  Dunit = g/cm3
  Dvalue = 1.2613
  Group = -> [C_element050,H_element043,O_element047]
  conduct = 2
  density = 1
  expand = 3
  formula = G4_GLYCEROL
  name = G4_GLYCEROL
  specific = 4
FEATURE [App::DocumentObjectGroupPython] C_element051  label="C_element : 028"  # scripted group (container) (typed FeaturePython)
  n = 5
  ref = C_element
FEATURE [App::DocumentObjectGroupPython] H_element044  label="H_element : 023"  # scripted group (container) (typed FeaturePython)
  n = 5
  ref = H_element
FEATURE [App::DocumentObjectGroupPython] N_element020  label="N_element : 009"  # scripted group (container) (typed FeaturePython)
  n = 5
  ref = N_element
FEATURE [App::DocumentObjectGroupPython] O_element048  label="O_element : 024"  # scripted group (container) (typed FeaturePython)
  n = 1
  ref = O_element
FEATURE [App::DocumentObjectGroupPython] G4_GUANINE  # scripted group (container) (typed FeaturePython)
  Dunit = g/cm3
  Dvalue = 2.2
  Group = -> [C_element051,H_element044,N_element020,O_element048]
  conduct = 2
  density = 1
  expand = 3
  formula = G4_GUANINE
  name = G4_GUANINE
  specific = 4
FEATURE [App::DocumentObjectGroupPython] Ca_element012  label="Ca_element : 006"  # scripted group (container) (typed FeaturePython)
  n = 1
  ref = Ca_element
FEATURE [App::DocumentObjectGroupPython] S_element014  label="S_element : 005"  # scripted group (container) (typed FeaturePython)
  n = 1
  ref = S_element
FEATURE [App::DocumentObjectGroupPython] O_element049  label="O_element : 6"  # scripted group (container) (typed FeaturePython)
  n = 6
  ref = O_element
FEATURE [App::DocumentObjectGroupPython] H_element045  label="H_element : 024"  # scripted group (container) (typed FeaturePython)
  n = 4
  ref = H_element
FEATURE [App::DocumentObjectGroupPython] G4_GYPSUM  # scripted group (container) (typed FeaturePython)
  Dunit = g/cm3
  Dvalue = 2.32
  Group = -> [Ca_element012,S_element014,O_element049,H_element045]
  conduct = 2
  density = 1
  expand = 3
  formula = G4_GYPSUM
  name = G4_GYPSUM
  specific = 4
FEATURE [App::DocumentObjectGroupPython] C_element052  label="C_element : 7"  # scripted group (container) (typed FeaturePython)
  n = 7
  ref = C_element
FEATURE [App::DocumentObjectGroupPython] H_element046  label="H_element : 16"  # scripted group (container) (typed FeaturePython)
  n = 16
  ref = H_element
FEATURE [App::DocumentObjectGroupPython] G4_N_HEPTANE  label="G4_N-HEPTANE"  # scripted group (container) (typed FeaturePython)
  Dunit = g/cm3
  Dvalue = 0.68376
  Group = -> [C_element052,H_element046]
  conduct = 2
  density = 1
  expand = 3
  formula = G4_N-HEPTANE
  name = G4_N-HEPTANE
  specific = 4
FEATURE [App::DocumentObjectGroupPython] C_element053  label="C_element : 029"  # scripted group (container) (typed FeaturePython)
  n = 6
  ref = C_element
FEATURE [App::DocumentObjectGroupPython] H_element047  label="H_element : 14"  # scripted group (container) (typed FeaturePython)
  n = 14
  ref = H_element
FEATURE [App::DocumentObjectGroupPython] G4_N_HEXANE  label="G4_N-HEXANE"  # scripted group (container) (typed FeaturePython)
  Dunit = g/cm3
  Dvalue = 0.6603
  Group = -> [C_element053,H_element047]
  conduct = 2
  density = 1
  expand = 3
  formula = G4_N-HEXANE
  name = G4_N-HEXANE
  specific = 4
FEATURE [App::DocumentObjectGroupPython] C_element054  label="C_element : 22"  # scripted group (container) (typed FeaturePython)
  n = 22
  ref = C_element
FEATURE [App::DocumentObjectGroupPython] H_element048  label="H_element : 025"  # scripted group (container) (typed FeaturePython)
  n = 10
  ref = H_element
FEATURE [App::DocumentObjectGroupPython] N_element021  label="N_element : 010"  # scripted group (container) (typed FeaturePython)
  n = 2
  ref = N_element
FEATURE [App::DocumentObjectGroupPython] O_element050  label="O_element : 025"  # scripted group (container) (typed FeaturePython)
  n = 5
  ref = O_element
FEATURE [App::DocumentObjectGroupPython] G4_KAPTON  # scripted group (container) (typed FeaturePython)
  Dunit = g/cm3
  Dvalue = 1.42
  Group = -> [C_element054,H_element048,N_element021,O_element050]
  conduct = 2
  density = 1
  expand = 3
  formula = G4_KAPTON
  name = G4_KAPTON
  specific = 4
FEATURE [App::DocumentObjectGroupPython] La_element001  label="La_element : 1"  # scripted group (container) (typed FeaturePython)
  n = 1
  ref = La_element
FEATURE [App::DocumentObjectGroupPython] Br_element003  label="Br_element : 002"  # scripted group (container) (typed FeaturePython)
  n = 1
  ref = Br_element
FEATURE [App::DocumentObjectGroupPython] O_element051  label="O_element : 026"  # scripted group (container) (typed FeaturePython)
  n = 1
  ref = O_element
FEATURE [App::DocumentObjectGroupPython] G4_LANTHANUM_OXYBROMIDE  # scripted group (container) (typed FeaturePython)
  Dunit = g/cm3
  Dvalue = 6.28
  Group = -> [La_element001,Br_element003,O_element051]
  conduct = 2
  density = 1
  expand = 3
  formula = G4_LANTHANUM_OXYBROMIDE
  name = G4_LANTHANUM_OXYBROMIDE
  specific = 4
FEATURE [App::DocumentObjectGroupPython] La_element002  label="La_element : 2"  # scripted group (container) (typed FeaturePython)
  n = 2
  ref = La_element
FEATURE [App::DocumentObjectGroupPython] O_element052  label="O_element : 027"  # scripted group (container) (typed FeaturePython)
  n = 2
  ref = O_element
FEATURE [App::DocumentObjectGroupPython] S_element015  label="S_element : 006"  # scripted group (container) (typed FeaturePython)
  n = 1
  ref = S_element
FEATURE [App::DocumentObjectGroupPython] G4_LANTHANUM_OXYSULFIDE  # scripted group (container) (typed FeaturePython)
  Dunit = g/cm3
  Dvalue = 5.86
  Group = -> [La_element002,O_element052,S_element015]
  conduct = 2
  density = 1
  expand = 3
  formula = G4_LANTHANUM_OXYSULFIDE
  name = G4_LANTHANUM_OXYSULFIDE
  specific = 4
FEATURE [App::DocumentObjectGroupPython] O_element053  label="O_element : 0.072"  # scripted group (container) (typed FeaturePython)
  n = 0.071682
FEATURE [App::DocumentObjectGroupPython] Pb_element002  label="Pb_element : 0.928"  # scripted group (container) (typed FeaturePython)
  n = 0.928318
FEATURE [App::DocumentObjectGroupPython] G4_LEAD_OXIDE  # scripted group (container) (typed FeaturePython)
  Dunit = g/cm3
  Dvalue = 9.53
  Group = -> [O_element053,Pb_element002]
  conduct = 2
  density = 1
  expand = 3
  formula = G4_LEAD_OXIDE
  name = G4_LEAD_OXIDE
  specific = 4
FEATURE [App::DocumentObjectGroupPython] Li_element001  label="Li_element : 1"  # scripted group (container) (typed FeaturePython)
  n = 1
  ref = Li_element
FEATURE [App::DocumentObjectGroupPython] N_element022  label="N_element : 011"  # scripted group (container) (typed FeaturePython)
  n = 1
  ref = N_element
FEATURE [App::DocumentObjectGroupPython] H_element049  label="H_element : 026"  # scripted group (container) (typed FeaturePython)
  n = 2
  ref = H_element
FEATURE [App::DocumentObjectGroupPython] G4_LITHIUM_AMIDE  # scripted group (container) (typed FeaturePython)
  Dunit = g/cm3
  Dvalue = 1.178
  Group = -> [Li_element001,N_element022,H_element049]
  conduct = 2
  density = 1
  expand = 3
  formula = G4_LITHIUM_AMIDE
  name = G4_LITHIUM_AMIDE
  specific = 4
FEATURE [App::DocumentObjectGroupPython] Li_element002  label="Li_element : 2"  # scripted group (container) (typed FeaturePython)
  n = 2
  ref = Li_element
FEATURE [App::DocumentObjectGroupPython] C_element055  label="C_element : 030"  # scripted group (container) (typed FeaturePython)
  n = 1
  ref = C_element
FEATURE [App::DocumentObjectGroupPython] O_element054  label="O_element : 028"  # scripted group (container) (typed FeaturePython)
  n = 3
  ref = O_element
FEATURE [App::DocumentObjectGroupPython] G4_LITHIUM_CARBONATE  # scripted group (container) (typed FeaturePython)
  Dunit = g/cm3
  Dvalue = 2.11
  Group = -> [Li_element002,C_element055,O_element054]
  conduct = 2
  density = 1
  expand = 3
  formula = G4_LITHIUM_CARBONATE
  name = G4_LITHIUM_CARBONATE
  specific = 4
FEATURE [App::DocumentObjectGroupPython] Li_element003  label="Li_element : 003"  # scripted group (container) (typed FeaturePython)
  n = 1
  ref = Li_element
FEATURE [App::DocumentObjectGroupPython] F_element012  label="F_element : 004"  # scripted group (container) (typed FeaturePython)
  n = 1
  ref = F_element
FEATURE [App::DocumentObjectGroupPython] G4_LITHIUM_FLUORIDE  # scripted group (container) (typed FeaturePython)
  Dunit = g/cm3
  Dvalue = 2.635
  Group = -> [Li_element003,F_element012]
  conduct = 2
  density = 1
  expand = 3
  formula = G4_LITHIUM_FLUORIDE
  name = G4_LITHIUM_FLUORIDE
  specific = 4
FEATURE [App::DocumentObjectGroupPython] Li_element004  label="Li_element : 004"  # scripted group (container) (typed FeaturePython)
  n = 1
  ref = Li_element
FEATURE [App::DocumentObjectGroupPython] H_element050  label="H_element : 027"  # scripted group (container) (typed FeaturePython)
  n = 1
  ref = H_element
FEATURE [App::DocumentObjectGroupPython] G4_LITHIUM_HYDRIDE  # scripted group (container) (typed FeaturePython)
  Dunit = g/cm3
  Dvalue = 0.82
  Group = -> [Li_element004,H_element050]
  conduct = 2
  density = 1
  expand = 3
  formula = G4_LITHIUM_HYDRIDE
  name = G4_LITHIUM_HYDRIDE
  specific = 4
FEATURE [App::DocumentObjectGroupPython] Li_element005  label="Li_element : 005"  # scripted group (container) (typed FeaturePython)
  n = 1
  ref = Li_element
FEATURE [App::DocumentObjectGroupPython] I_element003  label="I_element : 002"  # scripted group (container) (typed FeaturePython)
  n = 1
  ref = I_element
FEATURE [App::DocumentObjectGroupPython] G4_LITHIUM_IODIDE  # scripted group (container) (typed FeaturePython)
  Dunit = g/cm3
  Dvalue = 3.494
  Group = -> [Li_element005,I_element003]
  conduct = 2
  density = 1
  expand = 3
  formula = G4_LITHIUM_IODIDE
  name = G4_LITHIUM_IODIDE
  specific = 4
FEATURE [App::DocumentObjectGroupPython] Li_element006  label="Li_element : 006"  # scripted group (container) (typed FeaturePython)
  n = 2
  ref = Li_element
FEATURE [App::DocumentObjectGroupPython] O_element055  label="O_element : 029"  # scripted group (container) (typed FeaturePython)
  n = 1
  ref = O_element
FEATURE [App::DocumentObjectGroupPython] G4_LITHIUM_OXIDE  # scripted group (container) (typed FeaturePython)
  Dunit = g/cm3
  Dvalue = 2.013
  Group = -> [Li_element006,O_element055]
  conduct = 2
  density = 1
  expand = 3
  formula = G4_LITHIUM_OXIDE
  name = G4_LITHIUM_OXIDE
  specific = 4
FEATURE [App::DocumentObjectGroupPython] Li_element007  label="Li_element : 007"  # scripted group (container) (typed FeaturePython)
  n = 2
  ref = Li_element
FEATURE [App::DocumentObjectGroupPython] B_element005  label="B_element : 005"  # scripted group (container) (typed FeaturePython)
  n = 4
  ref = B_element
FEATURE [App::DocumentObjectGroupPython] O_element056  label="O_element : 7"  # scripted group (container) (typed FeaturePython)
  n = 7
  ref = O_element
FEATURE [App::DocumentObjectGroupPython] G4_LITHIUM_TETRABORATE  # scripted group (container) (typed FeaturePython)
  Dunit = g/cm3
  Dvalue = 2.44
  Group = -> [Li_element007,B_element005,O_element056]
  conduct = 2
  density = 1
  expand = 3
  formula = G4_LITHIUM_TETRABORATE
  name = G4_LITHIUM_TETRABORATE
  specific = 4
FEATURE [App::DocumentObjectGroupPython] H_element051  label="H_element : 0.105"  # scripted group (container) (typed FeaturePython)
  n = 0.105
FEATURE [App::DocumentObjectGroupPython] C_element056  label="C_element : 0.083"  # scripted group (container) (typed FeaturePython)
  n = 0.083
FEATURE [App::DocumentObjectGroupPython] N_element023  label="N_element : 0.023"  # scripted group (container) (typed FeaturePython)
  n = 0.023
FEATURE [App::DocumentObjectGroupPython] O_element057  label="O_element : 0.779"  # scripted group (container) (typed FeaturePython)
  n = 0.779
FEATURE [App::DocumentObjectGroupPython] Na_element010  label="Na_element : 0.097"  # scripted group (container) (typed FeaturePython)
  n = 0.002
FEATURE [App::DocumentObjectGroupPython] P_element006  label="P_element : 0.105"  # scripted group (container) (typed FeaturePython)
  n = 0.001
FEATURE [App::DocumentObjectGroupPython] S_element016  label="S_element : 0.017"  # scripted group (container) (typed FeaturePython)
  n = 0.002
FEATURE [App::DocumentObjectGroupPython] Cl_element014  label="Cl_element : 0.587"  # scripted group (container) (typed FeaturePython)
  n = 0.003
FEATURE [App::DocumentObjectGroupPython] K_element005  label="K_element : 0.015"  # scripted group (container) (typed FeaturePython)
  n = 0.002
FEATURE [App::DocumentObjectGroupPython] G4_LUNG_ICRP  # scripted group (container) (typed FeaturePython)
  Dunit = g/cm3
  Dvalue = 1.04
  Group = -> [H_element051,C_element056,N_element023,O_element057,Na_element010,P_element006,S_element016,Cl_element014,K_element005]
  conduct = 2
  density = 1
  expand = 3
  formula = G4_LUNG_ICRP
  name = G4_LUNG_ICRP
  specific = 4
FEATURE [App::DocumentObjectGroupPython] H_element052  label="H_element : 0.116"  # scripted group (container) (typed FeaturePython)
  n = 0.114318
FEATURE [App::DocumentObjectGroupPython] C_element057  label="C_element : 0.656"  # scripted group (container) (typed FeaturePython)
  n = 0.655824
FEATURE [App::DocumentObjectGroupPython] O_element058  label="O_element : 0.092"  # scripted group (container) (typed FeaturePython)
  n = 0.0921831
FEATURE [App::DocumentObjectGroupPython] Mg_element004  label="Mg_element : 0.135"  # scripted group (container) (typed FeaturePython)
  n = 0.134792
FEATURE [App::DocumentObjectGroupPython] Ca_element013  label="Ca_element : 0.003"  # scripted group (container) (typed FeaturePython)
  n = 0.002883
FEATURE [App::DocumentObjectGroupPython] G4_M3_WAX  # scripted group (container) (typed FeaturePython)
  Dunit = g/cm3
  Dvalue = 1.05
  Group = -> [H_element052,C_element057,O_element058,Mg_element004,Ca_element013]
  conduct = 2
  density = 1
  expand = 3
  formula = G4_M3_WAX
  name = G4_M3_WAX
  specific = 4
FEATURE [App::DocumentObjectGroupPython] Mg_element005  label="Mg_element : 1"  # scripted group (container) (typed FeaturePython)
  n = 1
  ref = Mg_element
FEATURE [App::DocumentObjectGroupPython] C_element058  label="C_element : 031"  # scripted group (container) (typed FeaturePython)
  n = 1
  ref = C_element
FEATURE [App::DocumentObjectGroupPython] O_element059  label="O_element : 030"  # scripted group (container) (typed FeaturePython)
  n = 3
  ref = O_element
FEATURE [App::DocumentObjectGroupPython] G4_MAGNESIUM_CARBONATE  # scripted group (container) (typed FeaturePython)
  Dunit = g/cm3
  Dvalue = 2.958
  Group = -> [Mg_element005,C_element058,O_element059]
  conduct = 2
  density = 1
  expand = 3
  formula = G4_MAGNESIUM_CARBONATE
  name = G4_MAGNESIUM_CARBONATE
  specific = 4
FEATURE [App::DocumentObjectGroupPython] Mg_element006  label="Mg_element : 002"  # scripted group (container) (typed FeaturePython)
  n = 1
  ref = Mg_element
FEATURE [App::DocumentObjectGroupPython] F_element013  label="F_element : 005"  # scripted group (container) (typed FeaturePython)
  n = 2
  ref = F_element
FEATURE [App::DocumentObjectGroupPython] G4_MAGNESIUM_FLUORIDE  # scripted group (container) (typed FeaturePython)
  Dunit = g/cm3
  Dvalue = 3
  Group = -> [Mg_element006,F_element013]
  conduct = 2
  density = 1
  expand = 3
  formula = G4_MAGNESIUM_FLUORIDE
  name = G4_MAGNESIUM_FLUORIDE
  specific = 4
FEATURE [App::DocumentObjectGroupPython] Mg_element007  label="Mg_element : 003"  # scripted group (container) (typed FeaturePython)
  n = 1
  ref = Mg_element
FEATURE [App::DocumentObjectGroupPython] O_element060  label="O_element : 031"  # scripted group (container) (typed FeaturePython)
  n = 1
  ref = O_element
FEATURE [App::DocumentObjectGroupPython] G4_MAGNESIUM_OXIDE  # scripted group (container) (typed FeaturePython)
  Dunit = g/cm3
  Dvalue = 3.58
  Group = -> [Mg_element007,O_element060]
  conduct = 2
  density = 1
  expand = 3
  formula = G4_MAGNESIUM_OXIDE
  name = G4_MAGNESIUM_OXIDE
  specific = 4
FEATURE [App::DocumentObjectGroupPython] Mg_element008  label="Mg_element : 004"  # scripted group (container) (typed FeaturePython)
  n = 1
  ref = Mg_element
FEATURE [App::DocumentObjectGroupPython] B_element006  label="B_element : 006"  # scripted group (container) (typed FeaturePython)
  n = 4
  ref = B_element
FEATURE [App::DocumentObjectGroupPython] O_element061  label="O_element : 032"  # scripted group (container) (typed FeaturePython)
  n = 7
  ref = O_element
FEATURE [App::DocumentObjectGroupPython] G4_MAGNESIUM_TETRABORATE  # scripted group (container) (typed FeaturePython)
  Dunit = g/cm3
  Dvalue = 2.53
  Group = -> [Mg_element008,B_element006,O_element061]
  conduct = 2
  density = 1
  expand = 3
  formula = G4_MAGNESIUM_TETRABORATE
  name = G4_MAGNESIUM_TETRABORATE
  specific = 4
FEATURE [App::DocumentObjectGroupPython] Hg_element001  label="Hg_element : 1"  # scripted group (container) (typed FeaturePython)
  n = 1
  ref = Hg_element
FEATURE [App::DocumentObjectGroupPython] I_element004  label="I_element : 2"  # scripted group (container) (typed FeaturePython)
  n = 2
  ref = I_element
FEATURE [App::DocumentObjectGroupPython] G4_MERCURIC_IODIDE  # scripted group (container) (typed FeaturePython)
  Dunit = g/cm3
  Dvalue = 6.36
  Group = -> [Hg_element001,I_element004]
  conduct = 2
  density = 1
  expand = 3
  formula = G4_MERCURIC_IODIDE
  name = G4_MERCURIC_IODIDE
  specific = 4
FEATURE [App::DocumentObjectGroupPython] C_element059  label="C_element : 032"  # scripted group (container) (typed FeaturePython)
  n = 1
  ref = C_element
FEATURE [App::DocumentObjectGroupPython] H_element053  label="H_element : 028"  # scripted group (container) (typed FeaturePython)
  n = 4
  ref = H_element
FEATURE [App::DocumentObjectGroupPython] G4_METHANE  # scripted group (container) (typed FeaturePython)
  Dunit = g/cm3
  Dvalue = 0.000667151
  Group = -> [C_element059,H_element053]
  conduct = 2
  density = 1
  expand = 3
  formula = G4_METHANE
  name = G4_METHANE
  specific = 4
FEATURE [App::DocumentObjectGroupPython] C_element060  label="C_element : 033"  # scripted group (container) (typed FeaturePython)
  n = 1
  ref = C_element
FEATURE [App::DocumentObjectGroupPython] H_element054  label="H_element : 029"  # scripted group (container) (typed FeaturePython)
  n = 4
  ref = H_element
FEATURE [App::DocumentObjectGroupPython] O_element062  label="O_element : 033"  # scripted group (container) (typed FeaturePython)
  n = 1
  ref = O_element
FEATURE [App::DocumentObjectGroupPython] G4_METHANOL  # scripted group (container) (typed FeaturePython)
  Dunit = g/cm3
  Dvalue = 0.7914
  Group = -> [C_element060,H_element054,O_element062]
  conduct = 2
  density = 1
  expand = 3
  formula = G4_METHANOL
  name = G4_METHANOL
  specific = 4
FEATURE [App::DocumentObjectGroupPython] H_element055  label="H_element : 0.134"  # scripted group (container) (typed FeaturePython)
  n = 0.13404
FEATURE [App::DocumentObjectGroupPython] C_element061  label="C_element : 0.778"  # scripted group (container) (typed FeaturePython)
  n = 0.77796
FEATURE [App::DocumentObjectGroupPython] O_element063  label="O_element : 0.035"  # scripted group (container) (typed FeaturePython)
  n = 0.03502
FEATURE [App::DocumentObjectGroupPython] Mg_element009  label="Mg_element : 0.039"  # scripted group (container) (typed FeaturePython)
  n = 0.038594
FEATURE [App::DocumentObjectGroupPython] Ti_element002  label="Ti_element : 0.014"  # scripted group (container) (typed FeaturePython)
  n = 0.014386
FEATURE [App::DocumentObjectGroupPython] G4_MIX_D_WAX  # scripted group (container) (typed FeaturePython)
  Dunit = g/cm3
  Dvalue = 0.99
  Group = -> [H_element055,C_element061,O_element063,Mg_element009,Ti_element002]
  conduct = 2
  density = 1
  expand = 3
  formula = G4_MIX_D_WAX
  name = G4_MIX_D_WAX
  specific = 4
FEATURE [App::DocumentObjectGroupPython] H_element056  label="H_element : 0.135"  # scripted group (container) (typed FeaturePython)
  n = 0.081192
FEATURE [App::DocumentObjectGroupPython] C_element062  label="C_element : 0.583"  # scripted group (container) (typed FeaturePython)
  n = 0.583442
FEATURE [App::DocumentObjectGroupPython] N_element024  label="N_element : 0.018"  # scripted group (container) (typed FeaturePython)
  n = 0.017798
FEATURE [App::DocumentObjectGroupPython] O_element064  label="O_element : 0.186"  # scripted group (container) (typed FeaturePython)
  n = 0.186381
FEATURE [App::DocumentObjectGroupPython] Mg_element010  label="Mg_element : 0.130"  # scripted group (container) (typed FeaturePython)
  n = 0.130287
FEATURE [App::DocumentObjectGroupPython] Cl_element015  label="Cl_element : 0.588"  # scripted group (container) (typed FeaturePython)
  n = 0.0009
FEATURE [App::DocumentObjectGroupPython] G4_MS20_TISSUE  # scripted group (container) (typed FeaturePython)
  Dunit = g/cm3
  Dvalue = 1
  Group = -> [H_element056,C_element062,N_element024,O_element064,Mg_element010,Cl_element015]
  conduct = 2
  density = 1
  expand = 3
  formula = G4_MS20_TISSUE
  name = G4_MS20_TISSUE
  specific = 4
FEATURE [App::DocumentObjectGroupPython] H_element057  label="H_element : 0.136"  # scripted group (container) (typed FeaturePython)
  n = 0.102
FEATURE [App::DocumentObjectGroupPython] C_element063  label="C_element : 0.143"  # scripted group (container) (typed FeaturePython)
  n = 0.143
FEATURE [App::DocumentObjectGroupPython] N_element025  label="N_element : 0.034"  # scripted group (container) (typed FeaturePython)
  n = 0.034
FEATURE [App::DocumentObjectGroupPython] O_element065  label="O_element : 0.710"  # scripted group (container) (typed FeaturePython)
  n = 0.71
FEATURE [App::DocumentObjectGroupPython] Na_element011  label="Na_element : 0.098"  # scripted group (container) (typed FeaturePython)
  n = 0.001
FEATURE [App::DocumentObjectGroupPython] P_element007  label="P_element : 0.002"  # scripted group (container) (typed FeaturePython)
  n = 0.002
FEATURE [App::DocumentObjectGroupPython] S_element017  label="S_element : 0.018"  # scripted group (container) (typed FeaturePython)
  n = 0.003
FEATURE [App::DocumentObjectGroupPython] Cl_element016  label="Cl_element : 0.589"  # scripted group (container) (typed FeaturePython)
  n = 0.001
FEATURE [App::DocumentObjectGroupPython] K_element006  label="K_element : 0.004"  # scripted group (container) (typed FeaturePython)
  n = 0.004
FEATURE [App::DocumentObjectGroupPython] G4_MUSCLE_SKELETAL_ICRP  # scripted group (container) (typed FeaturePython)
  Dunit = g/cm3
  Dvalue = 1.05
  Group = -> [H_element057,C_element063,N_element025,O_element065,Na_element011,P_element007,S_element017,Cl_element016,K_element006]
  conduct = 2
  density = 1
  expand = 3
  formula = G4_MUSCLE_SKELETAL_ICRP
  name = G4_MUSCLE_SKELETAL_ICRP
  specific = 4
FEATURE [App::DocumentObjectGroupPython] H_element058  label="H_element : 0.137"  # scripted group (container) (typed FeaturePython)
  n = 0.102102
FEATURE [App::DocumentObjectGroupPython] C_element064  label="C_element : 0.123"  # scripted group (container) (typed FeaturePython)
  n = 0.123123
FEATURE [App::DocumentObjectGroupPython] N_element026  label="N_element : 0.756"  # scripted group (container) (typed FeaturePython)
  n = 0.035035
FEATURE [App::DocumentObjectGroupPython] O_element066  label="O_element : 0.730"  # scripted group (container) (typed FeaturePython)
  n = 0.72973
FEATURE [App::DocumentObjectGroupPython] Na_element012  label="Na_element : 0.099"  # scripted group (container) (typed FeaturePython)
  n = 0.001001
FEATURE [App::DocumentObjectGroupPython] P_element008  label="P_element : 0.106"  # scripted group (container) (typed FeaturePython)
  n = 0.002002
FEATURE [App::DocumentObjectGroupPython] S_element018  label="S_element : 0.019"  # scripted group (container) (typed FeaturePython)
  n = 0.004004
FEATURE [App::DocumentObjectGroupPython] K_element007  label="K_element : 0.016"  # scripted group (container) (typed FeaturePython)
  n = 0.003003
FEATURE [App::DocumentObjectGroupPython] G4_MUSCLE_STRIATED_ICRU  # scripted group (container) (typed FeaturePython)
  Dunit = g/cm3
  Dvalue = 1.04
  Group = -> [H_element058,C_element064,N_element026,O_element066,Na_element012,P_element008,S_element018,K_element007]
  conduct = 2
  density = 1
  expand = 3
  formula = G4_MUSCLE_STRIATED_ICRU
  name = G4_MUSCLE_STRIATED_ICRU
  specific = 4
FEATURE [App::DocumentObjectGroupPython] H_element059  label="H_element : 0.098"  # scripted group (container) (typed FeaturePython)
  n = 0.0982341
FEATURE [App::DocumentObjectGroupPython] C_element065  label="C_element : 0.156"  # scripted group (container) (typed FeaturePython)
  n = 0.156214
FEATURE [App::DocumentObjectGroupPython] N_element027  label="N_element : 0.757"  # scripted group (container) (typed FeaturePython)
  n = 0.035451
FEATURE [App::DocumentObjectGroupPython] O_element067  label="O_element : 0.880"  # scripted group (container) (typed FeaturePython)
  n = 0.710101
FEATURE [App::DocumentObjectGroupPython] G4_MUSCLE_WITH_SUCROSE  # scripted group (container) (typed FeaturePython)
  Dunit = g/cm3
  Dvalue = 1.11
  Group = -> [H_element059,C_element065,N_element027,O_element067]
  conduct = 2
  density = 1
  expand = 3
  formula = G4_MUSCLE_WITH_SUCROSE
  name = G4_MUSCLE_WITH_SUCROSE
  specific = 4
FEATURE [App::DocumentObjectGroupPython] H_element060  label="H_element : 0.138"  # scripted group (container) (typed FeaturePython)
  n = 0.101969
FEATURE [App::DocumentObjectGroupPython] C_element066  label="C_element : 0.120"  # scripted group (container) (typed FeaturePython)
  n = 0.120058
FEATURE [App::DocumentObjectGroupPython] N_element028  label="N_element : 0.758"  # scripted group (container) (typed FeaturePython)
  n = 0.035451
FEATURE [App::DocumentObjectGroupPython] O_element068  label="O_element : 0.743"  # scripted group (container) (typed FeaturePython)
  n = 0.742522
FEATURE [App::DocumentObjectGroupPython] G4_MUSCLE_WITHOUT_SUCROSE  # scripted group (container) (typed FeaturePython)
  Dunit = g/cm3
  Dvalue = 1.07
  Group = -> [H_element060,C_element066,N_element028,O_element068]
  conduct = 2
  density = 1
  expand = 3
  formula = G4_MUSCLE_WITHOUT_SUCROSE
  name = G4_MUSCLE_WITHOUT_SUCROSE
  specific = 4
FEATURE [App::DocumentObjectGroupPython] C_element067  label="C_element : 10"  # scripted group (container) (typed FeaturePython)
  n = 10
  ref = C_element
FEATURE [App::DocumentObjectGroupPython] H_element061  label="H_element : 030"  # scripted group (container) (typed FeaturePython)
  n = 8
  ref = H_element
FEATURE [App::DocumentObjectGroupPython] G4_NAPHTHALENE  # scripted group (container) (typed FeaturePython)
  Dunit = g/cm3
  Dvalue = 1.145
  Group = -> [C_element067,H_element061]
  conduct = 2
  density = 1
  expand = 3
  formula = G4_NAPHTHALENE
  name = G4_NAPHTHALENE
  specific = 4
FEATURE [App::DocumentObjectGroupPython] C_element068  label="C_element : 034"  # scripted group (container) (typed FeaturePython)
  n = 6
  ref = C_element
FEATURE [App::DocumentObjectGroupPython] H_element062  label="H_element : 031"  # scripted group (container) (typed FeaturePython)
  n = 5
  ref = H_element
FEATURE [App::DocumentObjectGroupPython] N_element029  label="N_element : 012"  # scripted group (container) (typed FeaturePython)
  n = 1
  ref = N_element
FEATURE [App::DocumentObjectGroupPython] O_element069  label="O_element : 034"  # scripted group (container) (typed FeaturePython)
  n = 2
  ref = O_element
FEATURE [App::DocumentObjectGroupPython] G4_NITROBENZENE  # scripted group (container) (typed FeaturePython)
  Dunit = g/cm3
  Dvalue = 1.19867
  Group = -> [C_element068,H_element062,N_element029,O_element069]
  conduct = 2
  density = 1
  expand = 3
  formula = G4_NITROBENZENE
  name = G4_NITROBENZENE
  specific = 4
FEATURE [App::DocumentObjectGroupPython] N_element030  label="N_element : 013"  # scripted group (container) (typed FeaturePython)
  n = 2
  ref = N_element
FEATURE [App::DocumentObjectGroupPython] O_element070  label="O_element : 035"  # scripted group (container) (typed FeaturePython)
  n = 1
  ref = O_element
FEATURE [App::DocumentObjectGroupPython] G4_NITROUS_OXIDE  # scripted group (container) (typed FeaturePython)
  Dunit = g/cm3
  Dvalue = 0.00183094
  Group = -> [N_element030,O_element070]
  conduct = 2
  density = 1
  expand = 3
  formula = G4_NITROUS_OXIDE
  name = G4_NITROUS_OXIDE
  specific = 4
FEATURE [App::DocumentObjectGroupPython] H_element063  label="H_element : 0.104"  # scripted group (container) (typed FeaturePython)
  n = 0.103509
FEATURE [App::DocumentObjectGroupPython] C_element069  label="C_element : 0.648"  # scripted group (container) (typed FeaturePython)
  n = 0.648416
FEATURE [App::DocumentObjectGroupPython] N_element031  label="N_element : 0.100"  # scripted group (container) (typed FeaturePython)
  n = 0.0995361
FEATURE [App::DocumentObjectGroupPython] O_element071  label="O_element : 0.149"  # scripted group (container) (typed FeaturePython)
  n = 0.148539
FEATURE [App::DocumentObjectGroupPython] G4_NYLON_8062  label="G4_NYLON-8062"  # scripted group (container) (typed FeaturePython)
  Dunit = g/cm3
  Dvalue = 1.08
  Group = -> [H_element063,C_element069,N_element031,O_element071]
  conduct = 2
  density = 1
  expand = 3
  formula = G4_NYLON-8062
  name = G4_NYLON-8062
  specific = 4
FEATURE [App::DocumentObjectGroupPython] C_element070  label="C_element : 035"  # scripted group (container) (typed FeaturePython)
  n = 6
  ref = C_element
FEATURE [App::DocumentObjectGroupPython] H_element064  label="H_element : 11"  # scripted group (container) (typed FeaturePython)
  n = 11
  ref = H_element
FEATURE [App::DocumentObjectGroupPython] N_element032  label="N_element : 014"  # scripted group (container) (typed FeaturePython)
  n = 1
  ref = N_element
FEATURE [App::DocumentObjectGroupPython] O_element072  label="O_element : 036"  # scripted group (container) (typed FeaturePython)
  n = 1
  ref = O_element
FEATURE [App::DocumentObjectGroupPython] G4_NYLON_6_6  label="G4_NYLON-6-6"  # scripted group (container) (typed FeaturePython)
  Dunit = g/cm3
  Dvalue = 1.14
  Group = -> [C_element070,H_element064,N_element032,O_element072]
  conduct = 2
  density = 1
  expand = 3
  formula = G4_NYLON-6-6
  name = G4_NYLON-6-6
  specific = 4
FEATURE [App::DocumentObjectGroupPython] H_element065  label="H_element : 0.139"  # scripted group (container) (typed FeaturePython)
  n = 0.107062
FEATURE [App::DocumentObjectGroupPython] C_element071  label="C_element : 0.680"  # scripted group (container) (typed FeaturePython)
  n = 0.680449
FEATURE [App::DocumentObjectGroupPython] N_element033  label="N_element : 0.099"  # scripted group (container) (typed FeaturePython)
  n = 0.099189
FEATURE [App::DocumentObjectGroupPython] O_element073  label="O_element : 0.113"  # scripted group (container) (typed FeaturePython)
  n = 0.1133
FEATURE [App::DocumentObjectGroupPython] G4_NYLON_6_10  label="G4_NYLON-6-10"  # scripted group (container) (typed FeaturePython)
  Dunit = g/cm3
  Dvalue = 1.14
  Group = -> [H_element065,C_element071,N_element033,O_element073]
  conduct = 2
  density = 1
  expand = 3
  formula = G4_NYLON-6-10
  name = G4_NYLON-6-10
  specific = 4
FEATURE [App::DocumentObjectGroupPython] H_element066  label="H_element : 0.140"  # scripted group (container) (typed FeaturePython)
  n = 0.115476
FEATURE [App::DocumentObjectGroupPython] C_element072  label="C_element : 0.721"  # scripted group (container) (typed FeaturePython)
  n = 0.720818
FEATURE [App::DocumentObjectGroupPython] N_element034  label="N_element : 0.076"  # scripted group (container) (typed FeaturePython)
  n = 0.0764169
FEATURE [App::DocumentObjectGroupPython] O_element074  label="O_element : 0.087"  # scripted group (container) (typed FeaturePython)
  n = 0.0872889
FEATURE [App::DocumentObjectGroupPython] G4_NYLON_11_RILSAN  label="G4_NYLON-11_RILSAN"  # scripted group (container) (typed FeaturePython)
  Dunit = g/cm3
  Dvalue = 1.425
  Group = -> [H_element066,C_element072,N_element034,O_element074]
  conduct = 2
  density = 1
  expand = 3
  formula = G4_NYLON-11_RILSAN
  name = G4_NYLON-11_RILSAN
  specific = 4
FEATURE [App::DocumentObjectGroupPython] C_element073  label="C_element : 8"  # scripted group (container) (typed FeaturePython)
  n = 8
  ref = C_element
FEATURE [App::DocumentObjectGroupPython] H_element067  label="H_element : 18"  # scripted group (container) (typed FeaturePython)
  n = 18
  ref = H_element
FEATURE [App::DocumentObjectGroupPython] G4_OCTANE  # scripted group (container) (typed FeaturePython)
  Dunit = g/cm3
  Dvalue = 0.7026
  Group = -> [C_element073,H_element067]
  conduct = 2
  density = 1
  expand = 3
  formula = G4_OCTANE
  name = G4_OCTANE
  specific = 4
FEATURE [App::DocumentObjectGroupPython] C_element074  label="C_element : 25"  # scripted group (container) (typed FeaturePython)
  n = 25
  ref = C_element
FEATURE [App::DocumentObjectGroupPython] H_element068  label="H_element : 52"  # scripted group (container) (typed FeaturePython)
  n = 52
  ref = H_element
FEATURE [App::DocumentObjectGroupPython] G4_PARAFFIN  # scripted group (container) (typed FeaturePython)
  Dunit = g/cm3
  Dvalue = 0.93
  Group = -> [C_element074,H_element068]
  conduct = 2
  density = 1
  expand = 3
  formula = G4_PARAFFIN
  name = G4_PARAFFIN
  specific = 4
FEATURE [App::DocumentObjectGroupPython] C_element075  label="C_element : 036"  # scripted group (container) (typed FeaturePython)
  n = 5
  ref = C_element
FEATURE [App::DocumentObjectGroupPython] H_element069  label="H_element : 032"  # scripted group (container) (typed FeaturePython)
  n = 12
  ref = H_element
FEATURE [App::DocumentObjectGroupPython] G4_N_PENTANE  label="G4_N-PENTANE"  # scripted group (container) (typed FeaturePython)
  Dunit = g/cm3
  Dvalue = 0.6262
  Group = -> [C_element075,H_element069]
  conduct = 2
  density = 1
  expand = 3
  formula = G4_N-PENTANE
  name = G4_N-PENTANE
  specific = 4
FEATURE [App::DocumentObjectGroupPython] H_element070  label="H_element : 0.014"  # scripted group (container) (typed FeaturePython)
  n = 0.0141
FEATURE [App::DocumentObjectGroupPython] C_element076  label="C_element : 0.072"  # scripted group (container) (typed FeaturePython)
  n = 0.072261
FEATURE [App::DocumentObjectGroupPython] N_element035  label="N_element : 0.019"  # scripted group (container) (typed FeaturePython)
  n = 0.01932
FEATURE [App::DocumentObjectGroupPython] O_element075  label="O_element : 0.066"  # scripted group (container) (typed FeaturePython)
  n = 0.066101
FEATURE [App::DocumentObjectGroupPython] S_element019  label="S_element : 0.020"  # scripted group (container) (typed FeaturePython)
  n = 0.00189
FEATURE [App::DocumentObjectGroupPython] Br_element004  label="Br_element : 0.349"  # scripted group (container) (typed FeaturePython)
  n = 0.349103
FEATURE [App::DocumentObjectGroupPython] Ag_element001  label="Ag_element : 0.474"  # scripted group (container) (typed FeaturePython)
  n = 0.474105
FEATURE [App::DocumentObjectGroupPython] I_element005  label="I_element : 0.003"  # scripted group (container) (typed FeaturePython)
  n = 0.00312
FEATURE [App::DocumentObjectGroupPython] G4_PHOTO_EMULSION  # scripted group (container) (typed FeaturePython)
  Dunit = g/cm3
  Dvalue = 3.815
  Group = -> [H_element070,C_element076,N_element035,O_element075,S_element019,Br_element004,Ag_element001,I_element005]
  conduct = 2
  density = 1
  expand = 3
  formula = G4_PHOTO_EMULSION
  name = G4_PHOTO_EMULSION
  specific = 4
FEATURE [App::DocumentObjectGroupPython] C_element077  label="C_element : 9"  # scripted group (container) (typed FeaturePython)
  n = 9
  ref = C_element
FEATURE [App::DocumentObjectGroupPython] H_element071  label="H_element : 033"  # scripted group (container) (typed FeaturePython)
  n = 10
  ref = H_element
FEATURE [App::DocumentObjectGroupPython] G4_PLASTIC_SC_VINYLTOLUENE  # scripted group (container) (typed FeaturePython)
  Dunit = g/cm3
  Dvalue = 1.032
  Group = -> [C_element077,H_element071]
  conduct = 2
  density = 1
  expand = 3
  formula = G4_PLASTIC_SC_VINYLTOLUENE
  name = G4_PLASTIC_SC_VINYLTOLUENE
  specific = 4
FEATURE [App::DocumentObjectGroupPython] Pu_element001  label="Pu_element : 1"  # scripted group (container) (typed FeaturePython)
  n = 1
  ref = Pu_element
FEATURE [App::DocumentObjectGroupPython] O_element076  label="O_element : 037"  # scripted group (container) (typed FeaturePython)
  n = 2
  ref = O_element
FEATURE [App::DocumentObjectGroupPython] G4_PLUTONIUM_DIOXIDE  # scripted group (container) (typed FeaturePython)
  Dunit = g/cm3
  Dvalue = 11.46
  Group = -> [Pu_element001,O_element076]
  conduct = 2
  density = 1
  expand = 3
  formula = G4_PLUTONIUM_DIOXIDE
  name = G4_PLUTONIUM_DIOXIDE
  specific = 4
FEATURE [App::DocumentObjectGroupPython] C_element078  label="C_element : 037"  # scripted group (container) (typed FeaturePython)
  n = 3
  ref = C_element
FEATURE [App::DocumentObjectGroupPython] H_element072  label="H_element : 034"  # scripted group (container) (typed FeaturePython)
  n = 3
  ref = H_element
FEATURE [App::DocumentObjectGroupPython] N_element036  label="N_element : 015"  # scripted group (container) (typed FeaturePython)
  n = 1
  ref = N_element
FEATURE [App::DocumentObjectGroupPython] G4_POLYACRYLONITRILE  # scripted group (container) (typed FeaturePython)
  Dunit = g/cm3
  Dvalue = 1.17
  Group = -> [C_element078,H_element072,N_element036]
  conduct = 2
  density = 1
  expand = 3
  formula = G4_POLYACRYLONITRILE
  name = G4_POLYACRYLONITRILE
  specific = 4
FEATURE [App::DocumentObjectGroupPython] C_element079  label="C_element : 16"  # scripted group (container) (typed FeaturePython)
  n = 16
  ref = C_element
FEATURE [App::DocumentObjectGroupPython] H_element073  label="H_element : 035"  # scripted group (container) (typed FeaturePython)
  n = 14
  ref = H_element
FEATURE [App::DocumentObjectGroupPython] O_element077  label="O_element : 038"  # scripted group (container) (typed FeaturePython)
  n = 3
  ref = O_element
FEATURE [App::DocumentObjectGroupPython] G4_POLYCARBONATE  # scripted group (container) (typed FeaturePython)
  Dunit = g/cm3
  Dvalue = 1.2
  Group = -> [C_element079,H_element073,O_element077]
  conduct = 2
  density = 1
  expand = 3
  formula = G4_POLYCARBONATE
  name = G4_POLYCARBONATE
  specific = 4
FEATURE [App::DocumentObjectGroupPython] C_element080  label="C_element : 038"  # scripted group (container) (typed FeaturePython)
  n = 8
  ref = C_element
FEATURE [App::DocumentObjectGroupPython] H_element074  label="H_element : 036"  # scripted group (container) (typed FeaturePython)
  n = 7
  ref = H_element
FEATURE [App::DocumentObjectGroupPython] Cl_element017  label="Cl_element : 007"  # scripted group (container) (typed FeaturePython)
  n = 1
  ref = Cl_element
FEATURE [App::DocumentObjectGroupPython] G4_POLYCHLOROSTYRENE  # scripted group (container) (typed FeaturePython)
  Dunit = g/cm3
  Dvalue = 1.3
  Group = -> [C_element080,H_element074,Cl_element017]
  conduct = 2
  density = 1
  expand = 3
  formula = G4_POLYCHLOROSTYRENE
  name = G4_POLYCHLOROSTYRENE
  specific = 4
FEATURE [App::DocumentObjectGroupPython] C_element081  label="C_element : 039"  # scripted group (container) (typed FeaturePython)
  n = 1
  ref = C_element
FEATURE [App::DocumentObjectGroupPython] H_element075  label="H_element : 037"  # scripted group (container) (typed FeaturePython)
  n = 2
  ref = H_element
FEATURE [App::DocumentObjectGroupPython] G4_POLYETHYLENE  # scripted group (container) (typed FeaturePython)
  Dunit = g/cm3
  Dvalue = 0.94
  Group = -> [C_element081,H_element075]
  conduct = 2
  density = 1
  expand = 3
  formula = G4_POLYETHYLENE
  name = G4_POLYETHYLENE
  specific = 4
FEATURE [App::DocumentObjectGroupPython] C_element082  label="C_element : 040"  # scripted group (container) (typed FeaturePython)
  n = 10
  ref = C_element
FEATURE [App::DocumentObjectGroupPython] H_element076  label="H_element : 038"  # scripted group (container) (typed FeaturePython)
  n = 8
  ref = H_element
FEATURE [App::DocumentObjectGroupPython] O_element078  label="O_element : 039"  # scripted group (container) (typed FeaturePython)
  n = 4
  ref = O_element
FEATURE [App::DocumentObjectGroupPython] G4_MYLAR  # scripted group (container) (typed FeaturePython)
  Dunit = g/cm3
  Dvalue = 1.4
  Group = -> [C_element082,H_element076,O_element078]
  conduct = 2
  density = 1
  expand = 3
  formula = G4_MYLAR
  name = G4_MYLAR
  specific = 4
FEATURE [App::DocumentObjectGroupPython] C_element083  label="C_element : 041"  # scripted group (container) (typed FeaturePython)
  n = 5
  ref = C_element
FEATURE [App::DocumentObjectGroupPython] H_element077  label="H_element : 039"  # scripted group (container) (typed FeaturePython)
  n = 8
  ref = H_element
FEATURE [App::DocumentObjectGroupPython] O_element079  label="O_element : 040"  # scripted group (container) (typed FeaturePython)
  n = 2
  ref = O_element
FEATURE [App::DocumentObjectGroupPython] G4_PLEXIGLASS  # scripted group (container) (typed FeaturePython)
  Dunit = g/cm3
  Dvalue = 1.19
  Group = -> [C_element083,H_element077,O_element079]
  conduct = 2
  density = 1
  expand = 3
  formula = G4_PLEXIGLASS
  name = G4_PLEXIGLASS
  specific = 4
FEATURE [App::DocumentObjectGroupPython] C_element084  label="C_element : 042"  # scripted group (container) (typed FeaturePython)
  n = 1
  ref = C_element
FEATURE [App::DocumentObjectGroupPython] H_element078  label="H_element : 040"  # scripted group (container) (typed FeaturePython)
  n = 2
  ref = H_element
FEATURE [App::DocumentObjectGroupPython] O_element080  label="O_element : 041"  # scripted group (container) (typed FeaturePython)
  n = 1
  ref = O_element
FEATURE [App::DocumentObjectGroupPython] G4_POLYOXYMETHYLENE  # scripted group (container) (typed FeaturePython)
  Dunit = g/cm3
  Dvalue = 1.425
  Group = -> [C_element084,H_element078,O_element080]
  conduct = 2
  density = 1
  expand = 3
  formula = G4_POLYOXYMETHYLENE
  name = G4_POLYOXYMETHYLENE
  specific = 4
FEATURE [App::DocumentObjectGroupPython] C_element085  label="C_element : 043"  # scripted group (container) (typed FeaturePython)
  n = 2
  ref = C_element
FEATURE [App::DocumentObjectGroupPython] H_element079  label="H_element : 041"  # scripted group (container) (typed FeaturePython)
  n = 4
  ref = H_element
FEATURE [App::DocumentObjectGroupPython] G4_POLYPROPYLENE  # scripted group (container) (typed FeaturePython)
  Dunit = g/cm3
  Dvalue = 0.9
  Group = -> [C_element085,H_element079]
  conduct = 2
  density = 1
  expand = 3
  formula = G4_POLYPROPYLENE
  name = G4_POLYPROPYLENE
  specific = 4
FEATURE [App::DocumentObjectGroupPython] C_element086  label="C_element : 044"  # scripted group (container) (typed FeaturePython)
  n = 8
  ref = C_element
FEATURE [App::DocumentObjectGroupPython] H_element080  label="H_element : 042"  # scripted group (container) (typed FeaturePython)
  n = 8
  ref = H_element
FEATURE [App::DocumentObjectGroupPython] G4_POLYSTYRENE  # scripted group (container) (typed FeaturePython)
  Dunit = g/cm3
  Dvalue = 1.06
  Group = -> [C_element086,H_element080]
  conduct = 2
  density = 1
  expand = 3
  formula = G4_POLYSTYRENE
  name = G4_POLYSTYRENE
  specific = 4
FEATURE [App::DocumentObjectGroupPython] C_element087  label="C_element : 045"  # scripted group (container) (typed FeaturePython)
  n = 2
  ref = C_element
FEATURE [App::DocumentObjectGroupPython] F_element014  label="F_element : 4"  # scripted group (container) (typed FeaturePython)
  n = 4
  ref = F_element
FEATURE [App::DocumentObjectGroupPython] G4_TEFLON  # scripted group (container) (typed FeaturePython)
  Dunit = g/cm3
  Dvalue = 2.2
  Group = -> [C_element087,F_element014]
  conduct = 2
  density = 1
  expand = 3
  formula = G4_TEFLON
  name = G4_TEFLON
  specific = 4
FEATURE [App::DocumentObjectGroupPython] C_element088  label="C_element : 046"  # scripted group (container) (typed FeaturePython)
  n = 2
  ref = C_element
FEATURE [App::DocumentObjectGroupPython] F_element015  label="F_element : 006"  # scripted group (container) (typed FeaturePython)
  n = 3
  ref = F_element
FEATURE [App::DocumentObjectGroupPython] Cl_element018  label="Cl_element : 008"  # scripted group (container) (typed FeaturePython)
  n = 1
  ref = Cl_element
FEATURE [App::DocumentObjectGroupPython] G4_POLYTRIFLUOROCHLOROETHYLENE  # scripted group (container) (typed FeaturePython)
  Dunit = g/cm3
  Dvalue = 2.1
  Group = -> [C_element088,F_element015,Cl_element018]
  conduct = 2
  density = 1
  expand = 3
  formula = G4_POLYTRIFLUOROCHLOROETHYLENE
  name = G4_POLYTRIFLUOROCHLOROETHYLENE
  specific = 4
FEATURE [App::DocumentObjectGroupPython] C_element089  label="C_element : 047"  # scripted group (container) (typed FeaturePython)
  n = 4
  ref = C_element
FEATURE [App::DocumentObjectGroupPython] H_element081  label="H_element : 043"  # scripted group (container) (typed FeaturePython)
  n = 6
  ref = H_element
FEATURE [App::DocumentObjectGroupPython] O_element081  label="O_element : 042"  # scripted group (container) (typed FeaturePython)
  n = 2
  ref = O_element
FEATURE [App::DocumentObjectGroupPython] G4_POLYVINYL_ACETATE  # scripted group (container) (typed FeaturePython)
  Dunit = g/cm3
  Dvalue = 1.19
  Group = -> [C_element089,H_element081,O_element081]
  conduct = 2
  density = 1
  expand = 3
  formula = G4_POLYVINYL_ACETATE
  name = G4_POLYVINYL_ACETATE
  specific = 4
FEATURE [App::DocumentObjectGroupPython] C_element090  label="C_element : 048"  # scripted group (container) (typed FeaturePython)
  n = 2
  ref = C_element
FEATURE [App::DocumentObjectGroupPython] H_element082  label="H_element : 044"  # scripted group (container) (typed FeaturePython)
  n = 4
  ref = H_element
FEATURE [App::DocumentObjectGroupPython] O_element082  label="O_element : 043"  # scripted group (container) (typed FeaturePython)
  n = 1
  ref = O_element
FEATURE [App::DocumentObjectGroupPython] G4_POLYVINYL_ALCOHOL  # scripted group (container) (typed FeaturePython)
  Dunit = g/cm3
  Dvalue = 1.3
  Group = -> [C_element090,H_element082,O_element082]
  conduct = 2
  density = 1
  expand = 3
  formula = G4_POLYVINYL_ALCOHOL
  name = G4_POLYVINYL_ALCOHOL
  specific = 4
FEATURE [App::DocumentObjectGroupPython] C_element091  label="C_element : 049"  # scripted group (container) (typed FeaturePython)
  n = 8
  ref = C_element
FEATURE [App::DocumentObjectGroupPython] H_element083  label="H_element : 045"  # scripted group (container) (typed FeaturePython)
  n = 14
  ref = H_element
FEATURE [App::DocumentObjectGroupPython] O_element083  label="O_element : 044"  # scripted group (container) (typed FeaturePython)
  n = 2
  ref = O_element
FEATURE [App::DocumentObjectGroupPython] G4_POLYVINYL_BUTYRAL  # scripted group (container) (typed FeaturePython)
  Dunit = g/cm3
  Dvalue = 1.12
  Group = -> [C_element091,H_element083,O_element083]
  conduct = 2
  density = 1
  expand = 3
  formula = G4_POLYVINYL_BUTYRAL
  name = G4_POLYVINYL_BUTYRAL
  specific = 4
FEATURE [App::DocumentObjectGroupPython] C_element092  label="C_element : 050"  # scripted group (container) (typed FeaturePython)
  n = 2
  ref = C_element
FEATURE [App::DocumentObjectGroupPython] H_element084  label="H_element : 046"  # scripted group (container) (typed FeaturePython)
  n = 3
  ref = H_element
FEATURE [App::DocumentObjectGroupPython] Cl_element019  label="Cl_element : 009"  # scripted group (container) (typed FeaturePython)
  n = 1
  ref = Cl_element
FEATURE [App::DocumentObjectGroupPython] G4_POLYVINYL_CHLORIDE  # scripted group (container) (typed FeaturePython)
  Dunit = g/cm3
  Dvalue = 1.3
  Group = -> [C_element092,H_element084,Cl_element019]
  conduct = 2
  density = 1
  expand = 3
  formula = G4_POLYVINYL_CHLORIDE
  name = G4_POLYVINYL_CHLORIDE
  specific = 4
FEATURE [App::DocumentObjectGroupPython] C_element093  label="C_element : 051"  # scripted group (container) (typed FeaturePython)
  n = 2
  ref = C_element
FEATURE [App::DocumentObjectGroupPython] H_element085  label="H_element : 047"  # scripted group (container) (typed FeaturePython)
  n = 2
  ref = H_element
FEATURE [App::DocumentObjectGroupPython] Cl_element020  label="Cl_element : 010"  # scripted group (container) (typed FeaturePython)
  n = 2
  ref = Cl_element
FEATURE [App::DocumentObjectGroupPython] G4_POLYVINYLIDENE_CHLORIDE  # scripted group (container) (typed FeaturePython)
  Dunit = g/cm3
  Dvalue = 1.7
  Group = -> [C_element093,H_element085,Cl_element020]
  conduct = 2
  density = 1
  expand = 3
  formula = G4_POLYVINYLIDENE_CHLORIDE
  name = G4_POLYVINYLIDENE_CHLORIDE
  specific = 4
FEATURE [App::DocumentObjectGroupPython] C_element094  label="C_element : 052"  # scripted group (container) (typed FeaturePython)
  n = 2
  ref = C_element
FEATURE [App::DocumentObjectGroupPython] H_element086  label="H_element : 048"  # scripted group (container) (typed FeaturePython)
  n = 2
  ref = H_element
FEATURE [App::DocumentObjectGroupPython] F_element016  label="F_element : 007"  # scripted group (container) (typed FeaturePython)
  n = 2
  ref = F_element
FEATURE [App::DocumentObjectGroupPython] G4_POLYVINYLIDENE_FLUORIDE  # scripted group (container) (typed FeaturePython)
  Dunit = g/cm3
  Dvalue = 1.76
  Group = -> [C_element094,H_element086,F_element016]
  conduct = 2
  density = 1
  expand = 3
  formula = G4_POLYVINYLIDENE_FLUORIDE
  name = G4_POLYVINYLIDENE_FLUORIDE
  specific = 4
FEATURE [App::DocumentObjectGroupPython] C_element095  label="C_element : 053"  # scripted group (container) (typed FeaturePython)
  n = 6
  ref = C_element
FEATURE [App::DocumentObjectGroupPython] H_element087  label="H_element : 9"  # scripted group (container) (typed FeaturePython)
  n = 9
  ref = H_element
FEATURE [App::DocumentObjectGroupPython] N_element037  label="N_element : 016"  # scripted group (container) (typed FeaturePython)
  n = 1
  ref = N_element
FEATURE [App::DocumentObjectGroupPython] O_element084  label="O_element : 045"  # scripted group (container) (typed FeaturePython)
  n = 1
  ref = O_element
FEATURE [App::DocumentObjectGroupPython] G4_POLYVINYL_PYRROLIDONE  # scripted group (container) (typed FeaturePython)
  Dunit = g/cm3
  Dvalue = 1.25
  Group = -> [C_element095,H_element087,N_element037,O_element084]
  conduct = 2
  density = 1
  expand = 3
  formula = G4_POLYVINYL_PYRROLIDONE
  name = G4_POLYVINYL_PYRROLIDONE
  specific = 4
FEATURE [App::DocumentObjectGroupPython] K_element008  label="K_element : 1"  # scripted group (container) (typed FeaturePython)
  n = 1
  ref = K_element
FEATURE [App::DocumentObjectGroupPython] I_element006  label="I_element : 003"  # scripted group (container) (typed FeaturePython)
  n = 1
  ref = I_element
FEATURE [App::DocumentObjectGroupPython] G4_POTASSIUM_IODIDE  # scripted group (container) (typed FeaturePython)
  Dunit = g/cm3
  Dvalue = 3.13
  Group = -> [K_element008,I_element006]
  conduct = 2
  density = 1
  expand = 3
  formula = G4_POTASSIUM_IODIDE
  name = G4_POTASSIUM_IODIDE
  specific = 4
FEATURE [App::DocumentObjectGroupPython] K_element009  label="K_element : 2"  # scripted group (container) (typed FeaturePython)
  n = 2
  ref = K_element
FEATURE [App::DocumentObjectGroupPython] O_element085  label="O_element : 046"  # scripted group (container) (typed FeaturePython)
  n = 1
  ref = O_element
FEATURE [App::DocumentObjectGroupPython] G4_POTASSIUM_OXIDE  # scripted group (container) (typed FeaturePython)
  Dunit = g/cm3
  Dvalue = 2.32
  Group = -> [K_element009,O_element085]
  conduct = 2
  density = 1
  expand = 3
  formula = G4_POTASSIUM_OXIDE
  name = G4_POTASSIUM_OXIDE
  specific = 4
FEATURE [App::DocumentObjectGroupPython] C_element096  label="C_element : 054"  # scripted group (container) (typed FeaturePython)
  n = 3
  ref = C_element
FEATURE [App::DocumentObjectGroupPython] H_element088  label="H_element : 049"  # scripted group (container) (typed FeaturePython)
  n = 8
  ref = H_element
FEATURE [App::DocumentObjectGroupPython] G4_PROPANE  # scripted group (container) (typed FeaturePython)
  Dunit = g/cm3
  Dvalue = 0.00187939
  Group = -> [C_element096,H_element088]
  conduct = 2
  density = 1
  expand = 3
  formula = G4_PROPANE
  name = G4_PROPANE
  specific = 4
FEATURE [App::DocumentObjectGroupPython] C_element097  label="C_element : 055"  # scripted group (container) (typed FeaturePython)
  n = 3
  ref = C_element
FEATURE [App::DocumentObjectGroupPython] H_element089  label="H_element : 050"  # scripted group (container) (typed FeaturePython)
  n = 8
  ref = H_element
FEATURE [App::DocumentObjectGroupPython] G4_lPROPANE  # scripted group (container) (typed FeaturePython)
  Dunit = g/cm3
  Dvalue = 0.43
  Group = -> [C_element097,H_element089]
  conduct = 2
  density = 1
  expand = 3
  formula = G4_lPROPANE
  name = G4_lPROPANE
  specific = 4
FEATURE [App::DocumentObjectGroupPython] C_element098  label="C_element : 056"  # scripted group (container) (typed FeaturePython)
  n = 3
  ref = C_element
FEATURE [App::DocumentObjectGroupPython] H_element090  label="H_element : 051"  # scripted group (container) (typed FeaturePython)
  n = 8
  ref = H_element
FEATURE [App::DocumentObjectGroupPython] O_element086  label="O_element : 047"  # scripted group (container) (typed FeaturePython)
  n = 1
  ref = O_element
FEATURE [App::DocumentObjectGroupPython] G4_N_PROPYL_ALCOHOL  label="G4_N-PROPYL_ALCOHOL"  # scripted group (container) (typed FeaturePython)
  Dunit = g/cm3
  Dvalue = 0.8035
  Group = -> [C_element098,H_element090,O_element086]
  conduct = 2
  density = 1
  expand = 3
  formula = G4_N-PROPYL_ALCOHOL
  name = G4_N-PROPYL_ALCOHOL
  specific = 4
FEATURE [App::DocumentObjectGroupPython] C_element099  label="C_element : 057"  # scripted group (container) (typed FeaturePython)
  n = 5
  ref = C_element
FEATURE [App::DocumentObjectGroupPython] H_element091  label="H_element : 052"  # scripted group (container) (typed FeaturePython)
  n = 5
  ref = H_element
FEATURE [App::DocumentObjectGroupPython] N_element038  label="N_element : 017"  # scripted group (container) (typed FeaturePython)
  n = 1
  ref = N_element
FEATURE [App::DocumentObjectGroupPython] G4_PYRIDINE  # scripted group (container) (typed FeaturePython)
  Dunit = g/cm3
  Dvalue = 0.9819
  Group = -> [C_element099,H_element091,N_element038]
  conduct = 2
  density = 1
  expand = 3
  formula = G4_PYRIDINE
  name = G4_PYRIDINE
  specific = 4
FEATURE [App::DocumentObjectGroupPython] H_element092  label="H_element : 0.144"  # scripted group (container) (typed FeaturePython)
  n = 0.143711
FEATURE [App::DocumentObjectGroupPython] C_element100  label="C_element : 0.856"  # scripted group (container) (typed FeaturePython)
  n = 0.856289
FEATURE [App::DocumentObjectGroupPython] G4_RUBBER_BUTYL  # scripted group (container) (typed FeaturePython)
  Dunit = g/cm3
  Dvalue = 0.92
  Group = -> [H_element092,C_element100]
  conduct = 2
  density = 1
  expand = 3
  formula = G4_RUBBER_BUTYL
  name = G4_RUBBER_BUTYL
  specific = 4
FEATURE [App::DocumentObjectGroupPython] H_element093  label="H_element : 0.118"  # scripted group (container) (typed FeaturePython)
  n = 0.118371
FEATURE [App::DocumentObjectGroupPython] C_element101  label="C_element : 0.882"  # scripted group (container) (typed FeaturePython)
  n = 0.881629
FEATURE [App::DocumentObjectGroupPython] G4_RUBBER_NATURAL  # scripted group (container) (typed FeaturePython)
  Dunit = g/cm3
  Dvalue = 0.92
  Group = -> [H_element093,C_element101]
  conduct = 2
  density = 1
  expand = 3
  formula = G4_RUBBER_NATURAL
  name = G4_RUBBER_NATURAL
  specific = 4
FEATURE [App::DocumentObjectGroupPython] H_element094  label="H_element : 0.145"  # scripted group (container) (typed FeaturePython)
  n = 0.05692
FEATURE [App::DocumentObjectGroupPython] C_element102  label="C_element : 0.543"  # scripted group (container) (typed FeaturePython)
  n = 0.542646
FEATURE [App::DocumentObjectGroupPython] Cl_element021  label="Cl_element : 0.400"  # scripted group (container) (typed FeaturePython)
  n = 0.400434
FEATURE [App::DocumentObjectGroupPython] G4_RUBBER_NEOPRENE  # scripted group (container) (typed FeaturePython)
  Dunit = g/cm3
  Dvalue = 1.23
  Group = -> [H_element094,C_element102,Cl_element021]
  conduct = 2
  density = 1
  expand = 3
  formula = G4_RUBBER_NEOPRENE
  name = G4_RUBBER_NEOPRENE
  specific = 4
FEATURE [App::DocumentObjectGroupPython] Si_element006  label="Si_element : 1"  # scripted group (container) (typed FeaturePython)
  n = 1
  ref = Si_element
FEATURE [App::DocumentObjectGroupPython] O_element087  label="O_element : 048"  # scripted group (container) (typed FeaturePython)
  n = 2
  ref = O_element
FEATURE [App::DocumentObjectGroupPython] G4_SILICON_DIOXIDE  # scripted group (container) (typed FeaturePython)
  Dunit = g/cm3
  Dvalue = 2.32
  Group = -> [Si_element006,O_element087]
  conduct = 2
  density = 1
  expand = 3
  formula = G4_SILICON_DIOXIDE
  name = G4_SILICON_DIOXIDE
  specific = 4
FEATURE [App::DocumentObjectGroupPython] Ag_element002  label="Ag_element : 1"  # scripted group (container) (typed FeaturePython)
  n = 1
  ref = Ag_element
FEATURE [App::DocumentObjectGroupPython] Br_element005  label="Br_element : 003"  # scripted group (container) (typed FeaturePython)
  n = 1
  ref = Br_element
FEATURE [App::DocumentObjectGroupPython] G4_SILVER_BROMIDE  # scripted group (container) (typed FeaturePython)
  Dunit = g/cm3
  Dvalue = 6.473
  Group = -> [Ag_element002,Br_element005]
  conduct = 2
  density = 1
  expand = 3
  formula = G4_SILVER_BROMIDE
  name = G4_SILVER_BROMIDE
  specific = 4
FEATURE [App::DocumentObjectGroupPython] Ag_element003  label="Ag_element : 002"  # scripted group (container) (typed FeaturePython)
  n = 1
  ref = Ag_element
FEATURE [App::DocumentObjectGroupPython] Cl_element022  label="Cl_element : 011"  # scripted group (container) (typed FeaturePython)
  n = 1
  ref = Cl_element
FEATURE [App::DocumentObjectGroupPython] G4_SILVER_CHLORIDE  # scripted group (container) (typed FeaturePython)
  Dunit = g/cm3
  Dvalue = 5.56
  Group = -> [Ag_element003,Cl_element022]
  conduct = 2
  density = 1
  expand = 3
  formula = G4_SILVER_CHLORIDE
  name = G4_SILVER_CHLORIDE
  specific = 4
FEATURE [App::DocumentObjectGroupPython] Br_element006  label="Br_element : 0.423"  # scripted group (container) (typed FeaturePython)
  n = 0.422895
FEATURE [App::DocumentObjectGroupPython] Ag_element004  label="Ag_element : 0.574"  # scripted group (container) (typed FeaturePython)
  n = 0.573748
FEATURE [App::DocumentObjectGroupPython] I_element007  label="I_element : 0.649"  # scripted group (container) (typed FeaturePython)
  n = 0.003357
FEATURE [App::DocumentObjectGroupPython] G4_SILVER_HALIDES  # scripted group (container) (typed FeaturePython)
  Dunit = g/cm3
  Dvalue = 6.47
  Group = -> [Br_element006,Ag_element004,I_element007]
  conduct = 2
  density = 1
  expand = 3
  formula = G4_SILVER_HALIDES
  name = G4_SILVER_HALIDES
  specific = 4
FEATURE [App::DocumentObjectGroupPython] Ag_element005  label="Ag_element : 003"  # scripted group (container) (typed FeaturePython)
  n = 1
  ref = Ag_element
FEATURE [App::DocumentObjectGroupPython] I_element008  label="I_element : 004"  # scripted group (container) (typed FeaturePython)
  n = 1
  ref = I_element
FEATURE [App::DocumentObjectGroupPython] G4_SILVER_IODIDE  # scripted group (container) (typed FeaturePython)
  Dunit = g/cm3
  Dvalue = 6.01
  Group = -> [Ag_element005,I_element008]
  conduct = 2
  density = 1
  expand = 3
  formula = G4_SILVER_IODIDE
  name = G4_SILVER_IODIDE
  specific = 4
FEATURE [App::DocumentObjectGroupPython] H_element095  label="H_element : 0.100"  # scripted group (container) (typed FeaturePython)
  n = 0.1
FEATURE [App::DocumentObjectGroupPython] C_element103  label="C_element : 0.204"  # scripted group (container) (typed FeaturePython)
  n = 0.204
FEATURE [App::DocumentObjectGroupPython] N_element039  label="N_element : 0.759"  # scripted group (container) (typed FeaturePython)
  n = 0.042
FEATURE [App::DocumentObjectGroupPython] O_element088  label="O_element : 0.645"  # scripted group (container) (typed FeaturePython)
  n = 0.645
FEATURE [App::DocumentObjectGroupPython] Na_element013  label="Na_element : 0.100"  # scripted group (container) (typed FeaturePython)
  n = 0.002
FEATURE [App::DocumentObjectGroupPython] P_element009  label="P_element : 0.107"  # scripted group (container) (typed FeaturePython)
  n = 0.001
FEATURE [App::DocumentObjectGroupPython] S_element020  label="S_element : 0.021"  # scripted group (container) (typed FeaturePython)
  n = 0.002
FEATURE [App::DocumentObjectGroupPython] Cl_element023  label="Cl_element : 0.590"  # scripted group (container) (typed FeaturePython)
  n = 0.003
FEATURE [App::DocumentObjectGroupPython] K_element010  label="K_element : 0.001"  # scripted group (container) (typed FeaturePython)
  n = 0.001
FEATURE [App::DocumentObjectGroupPython] G4_SKIN_ICRP  # scripted group (container) (typed FeaturePython)
  Dunit = g/cm3
  Dvalue = 1.09
  Group = -> [H_element095,C_element103,N_element039,O_element088,Na_element013,P_element009,S_element020,Cl_element023,K_element010]
  conduct = 2
  density = 1
  expand = 3
  formula = G4_SKIN_ICRP
  name = G4_SKIN_ICRP
  specific = 4
FEATURE [App::DocumentObjectGroupPython] Na_element014  label="Na_element : 2"  # scripted group (container) (typed FeaturePython)
  n = 2
  ref = Na_element
FEATURE [App::DocumentObjectGroupPython] C_element104  label="C_element : 058"  # scripted group (container) (typed FeaturePython)
  n = 1
  ref = C_element
FEATURE [App::DocumentObjectGroupPython] O_element089  label="O_element : 049"  # scripted group (container) (typed FeaturePython)
  n = 3
  ref = O_element
FEATURE [App::DocumentObjectGroupPython] G4_SODIUM_CARBONATE  # scripted group (container) (typed FeaturePython)
  Dunit = g/cm3
  Dvalue = 2.532
  Group = -> [Na_element014,C_element104,O_element089]
  conduct = 2
  density = 1
  expand = 3
  formula = G4_SODIUM_CARBONATE
  name = G4_SODIUM_CARBONATE
  specific = 4
FEATURE [App::DocumentObjectGroupPython] Na_element015  label="Na_element : 1"  # scripted group (container) (typed FeaturePython)
  n = 1
  ref = Na_element
FEATURE [App::DocumentObjectGroupPython] I_element009  label="I_element : 005"  # scripted group (container) (typed FeaturePython)
  n = 1
  ref = I_element
FEATURE [App::DocumentObjectGroupPython] G4_SODIUM_IODIDE  # scripted group (container) (typed FeaturePython)
  Dunit = g/cm3
  Dvalue = 3.667
  Group = -> [Na_element015,I_element009]
  conduct = 2
  density = 1
  expand = 3
  formula = G4_SODIUM_IODIDE
  name = G4_SODIUM_IODIDE
  specific = 4
FEATURE [App::DocumentObjectGroupPython] Na_element016  label="Na_element : 003"  # scripted group (container) (typed FeaturePython)
  n = 2
  ref = Na_element
FEATURE [App::DocumentObjectGroupPython] O_element090  label="O_element : 050"  # scripted group (container) (typed FeaturePython)
  n = 1
  ref = O_element
FEATURE [App::DocumentObjectGroupPython] G4_SODIUM_MONOXIDE  # scripted group (container) (typed FeaturePython)
  Dunit = g/cm3
  Dvalue = 2.27
  Group = -> [Na_element016,O_element090]
  conduct = 2
  density = 1
  expand = 3
  formula = G4_SODIUM_MONOXIDE
  name = G4_SODIUM_MONOXIDE
  specific = 4
FEATURE [App::DocumentObjectGroupPython] Na_element017  label="Na_element : 004"  # scripted group (container) (typed FeaturePython)
  n = 1
  ref = Na_element
FEATURE [App::DocumentObjectGroupPython] N_element040  label="N_element : 018"  # scripted group (container) (typed FeaturePython)
  n = 1
  ref = N_element
FEATURE [App::DocumentObjectGroupPython] O_element091  label="O_element : 051"  # scripted group (container) (typed FeaturePython)
  n = 3
  ref = O_element
FEATURE [App::DocumentObjectGroupPython] G4_SODIUM_NITRATE  # scripted group (container) (typed FeaturePython)
  Dunit = g/cm3
  Dvalue = 2.261
  Group = -> [Na_element017,N_element040,O_element091]
  conduct = 2
  density = 1
  expand = 3
  formula = G4_SODIUM_NITRATE
  name = G4_SODIUM_NITRATE
  specific = 4
FEATURE [App::DocumentObjectGroupPython] C_element105  label="C_element : 059"  # scripted group (container) (typed FeaturePython)
  n = 14
  ref = C_element
FEATURE [App::DocumentObjectGroupPython] H_element096  label="H_element : 053"  # scripted group (container) (typed FeaturePython)
  n = 12
  ref = H_element
FEATURE [App::DocumentObjectGroupPython] G4_STILBENE  # scripted group (container) (typed FeaturePython)
  Dunit = g/cm3
  Dvalue = 0.9707
  Group = -> [C_element105,H_element096]
  conduct = 2
  density = 1
  expand = 3
  formula = G4_STILBENE
  name = G4_STILBENE
  specific = 4
FEATURE [App::DocumentObjectGroupPython] C_element106  label="C_element : 12"  # scripted group (container) (typed FeaturePython)
  n = 12
  ref = C_element
FEATURE [App::DocumentObjectGroupPython] H_element097  label="H_element : 22"  # scripted group (container) (typed FeaturePython)
  n = 22
  ref = H_element
FEATURE [App::DocumentObjectGroupPython] O_element092  label="O_element : 11"  # scripted group (container) (typed FeaturePython)
  n = 11
  ref = O_element
FEATURE [App::DocumentObjectGroupPython] G4_SUCROSE  # scripted group (container) (typed FeaturePython)
  Dunit = g/cm3
  Dvalue = 1.5805
  Group = -> [C_element106,H_element097,O_element092]
  conduct = 2
  density = 1
  expand = 3
  formula = G4_SUCROSE
  name = G4_SUCROSE
  specific = 4
FEATURE [App::DocumentObjectGroupPython] C_element107  label="C_element : 18"  # scripted group (container) (typed FeaturePython)
  n = 18
  ref = C_element
FEATURE [App::DocumentObjectGroupPython] H_element098  label="H_element : 054"  # scripted group (container) (typed FeaturePython)
  n = 14
  ref = H_element
FEATURE [App::DocumentObjectGroupPython] G4_TERPHENYL  # scripted group (container) (typed FeaturePython)
  Dunit = g/cm3
  Dvalue = 1.24
  Group = -> [C_element107,H_element098]
  conduct = 2
  density = 1
  expand = 3
  formula = G4_TERPHENYL
  name = G4_TERPHENYL
  specific = 4
FEATURE [App::DocumentObjectGroupPython] H_element099  label="H_element : 0.146"  # scripted group (container) (typed FeaturePython)
  n = 0.106
FEATURE [App::DocumentObjectGroupPython] C_element108  label="C_element : 0.883"  # scripted group (container) (typed FeaturePython)
  n = 0.099
FEATURE [App::DocumentObjectGroupPython] N_element041  label="N_element : 0.020"  # scripted group (container) (typed FeaturePython)
  n = 0.02
FEATURE [App::DocumentObjectGroupPython] O_element093  label="O_element : 0.766"  # scripted group (container) (typed FeaturePython)
  n = 0.766
FEATURE [App::DocumentObjectGroupPython] Na_element018  label="Na_element : 0.101"  # scripted group (container) (typed FeaturePython)
  n = 0.002
FEATURE [App::DocumentObjectGroupPython] P_element010  label="P_element : 0.108"  # scripted group (container) (typed FeaturePython)
  n = 0.001
FEATURE [App::DocumentObjectGroupPython] S_element021  label="S_element : 0.022"  # scripted group (container) (typed FeaturePython)
  n = 0.002
FEATURE [App::DocumentObjectGroupPython] Cl_element024  label="Cl_element : 0.002"  # scripted group (container) (typed FeaturePython)
  n = 0.002
FEATURE [App::DocumentObjectGroupPython] K_element011  label="K_element : 0.017"  # scripted group (container) (typed FeaturePython)
  n = 0.002
FEATURE [App::DocumentObjectGroupPython] G4_TESTIS_ICRP  # scripted group (container) (typed FeaturePython)
  Dunit = g/cm3
  Dvalue = 1.04
  Group = -> [H_element099,C_element108,N_element041,O_element093,Na_element018,P_element010,S_element021,Cl_element024,K_element011]
  conduct = 2
  density = 1
  expand = 3
  formula = G4_TESTIS_ICRP
  name = G4_TESTIS_ICRP
  specific = 4
FEATURE [App::DocumentObjectGroupPython] C_element109  label="C_element : 060"  # scripted group (container) (typed FeaturePython)
  n = 2
  ref = C_element
FEATURE [App::DocumentObjectGroupPython] Cl_element025  label="Cl_element : 012"  # scripted group (container) (typed FeaturePython)
  n = 4
  ref = Cl_element
FEATURE [App::DocumentObjectGroupPython] G4_TETRACHLOROETHYLENE  # scripted group (container) (typed FeaturePython)
  Dunit = g/cm3
  Dvalue = 1.625
  Group = -> [C_element109,Cl_element025]
  conduct = 2
  density = 1
  expand = 3
  formula = G4_TETRACHLOROETHYLENE
  name = G4_TETRACHLOROETHYLENE
  specific = 4
FEATURE [App::DocumentObjectGroupPython] Tl_element001  label="Tl_element : 1"  # scripted group (container) (typed FeaturePython)
  n = 1
  ref = Tl_element
FEATURE [App::DocumentObjectGroupPython] Cl_element026  label="Cl_element : 013"  # scripted group (container) (typed FeaturePython)
  n = 1
  ref = Cl_element
FEATURE [App::DocumentObjectGroupPython] G4_THALLIUM_CHLORIDE  # scripted group (container) (typed FeaturePython)
  Dunit = g/cm3
  Dvalue = 7.004
  Group = -> [Tl_element001,Cl_element026]
  conduct = 2
  density = 1
  expand = 3
  formula = G4_THALLIUM_CHLORIDE
  name = G4_THALLIUM_CHLORIDE
  specific = 4
FEATURE [App::DocumentObjectGroupPython] H_element100  label="H_element : 0.147"  # scripted group (container) (typed FeaturePython)
  n = 0.105
FEATURE [App::DocumentObjectGroupPython] C_element110  label="C_element : 0.256"  # scripted group (container) (typed FeaturePython)
  n = 0.256
FEATURE [App::DocumentObjectGroupPython] N_element042  label="N_element : 0.760"  # scripted group (container) (typed FeaturePython)
  n = 0.027
FEATURE [App::DocumentObjectGroupPython] O_element094  label="O_element : 0.602"  # scripted group (container) (typed FeaturePython)
  n = 0.602
FEATURE [App::DocumentObjectGroupPython] Na_element019  label="Na_element : 0.102"  # scripted group (container) (typed FeaturePython)
  n = 0.001
FEATURE [App::DocumentObjectGroupPython] P_element011  label="P_element : 0.109"  # scripted group (container) (typed FeaturePython)
  n = 0.002
FEATURE [App::DocumentObjectGroupPython] S_element022  label="S_element : 0.023"  # scripted group (container) (typed FeaturePython)
  n = 0.003
FEATURE [App::DocumentObjectGroupPython] Cl_element027  label="Cl_element : 0.591"  # scripted group (container) (typed FeaturePython)
  n = 0.002
FEATURE [App::DocumentObjectGroupPython] K_element012  label="K_element : 0.018"  # scripted group (container) (typed FeaturePython)
  n = 0.002
FEATURE [App::DocumentObjectGroupPython] G4_TISSUE_SOFT_ICRP  # scripted group (container) (typed FeaturePython)
  Dunit = g/cm3
  Dvalue = 1.03
  Group = -> [H_element100,C_element110,N_element042,O_element094,Na_element019,P_element011,S_element022,Cl_element027,K_element012]
  conduct = 2
  density = 1
  expand = 3
  formula = G4_TISSUE_SOFT_ICRP
  name = G4_TISSUE_SOFT_ICRP
  specific = 4
FEATURE [App::DocumentObjectGroupPython] H_element101  label="H_element : 0.148"  # scripted group (container) (typed FeaturePython)
  n = 0.101
FEATURE [App::DocumentObjectGroupPython] C_element111  label="C_element : 0.111"  # scripted group (container) (typed FeaturePython)
  n = 0.111
FEATURE [App::DocumentObjectGroupPython] N_element043  label="N_element : 0.026"  # scripted group (container) (typed FeaturePython)
  n = 0.026
FEATURE [App::DocumentObjectGroupPython] O_element095  label="O_element : 0.762"  # scripted group (container) (typed FeaturePython)
  n = 0.762
FEATURE [App::DocumentObjectGroupPython] G4_TISSUE_SOFT_ICRU_4  label="G4_TISSUE_SOFT_ICRU-4"  # scripted group (container) (typed FeaturePython)
  Dunit = g/cm3
  Dvalue = 1
  Group = -> [H_element101,C_element111,N_element043,O_element095]
  conduct = 2
  density = 1
  expand = 3
  formula = G4_TISSUE_SOFT_ICRU-4
  name = G4_TISSUE_SOFT_ICRU-4
  specific = 4
FEATURE [App::DocumentObjectGroupPython] H_element102  label="H_element : 0.149"  # scripted group (container) (typed FeaturePython)
  n = 0.101869
FEATURE [App::DocumentObjectGroupPython] C_element112  label="C_element : 0.456"  # scripted group (container) (typed FeaturePython)
  n = 0.456179
FEATURE [App::DocumentObjectGroupPython] N_element044  label="N_element : 0.761"  # scripted group (container) (typed FeaturePython)
  n = 0.035172
FEATURE [App::DocumentObjectGroupPython] O_element096  label="O_element : 0.407"  # scripted group (container) (typed FeaturePython)
  n = 0.40678
FEATURE [App::DocumentObjectGroupPython] G4_TISSUE_METHANE  label="G4_TISSUE-METHANE"  # scripted group (container) (typed FeaturePython)
  Dunit = g/cm3
  Dvalue = 0.00106409
  Group = -> [H_element102,C_element112,N_element044,O_element096]
  conduct = 2
  density = 1
  expand = 3
  formula = G4_TISSUE-METHANE
  name = G4_TISSUE-METHANE
  specific = 4
FEATURE [App::DocumentObjectGroupPython] H_element103  label="H_element : 0.103"  # scripted group (container) (typed FeaturePython)
  n = 0.102672
FEATURE [App::DocumentObjectGroupPython] C_element113  label="C_element : 0.569"  # scripted group (container) (typed FeaturePython)
  n = 0.56894
FEATURE [App::DocumentObjectGroupPython] N_element045  label="N_element : 0.762"  # scripted group (container) (typed FeaturePython)
  n = 0.035022
FEATURE [App::DocumentObjectGroupPython] O_element097  label="O_element : 0.293"  # scripted group (container) (typed FeaturePython)
  n = 0.293366
FEATURE [App::DocumentObjectGroupPython] G4_TISSUE_PROPANE  label="G4_TISSUE-PROPANE"  # scripted group (container) (typed FeaturePython)
  Dunit = g/cm3
  Dvalue = 0.00182628
  Group = -> [H_element103,C_element113,N_element045,O_element097]
  conduct = 2
  density = 1
  expand = 3
  formula = G4_TISSUE-PROPANE
  name = G4_TISSUE-PROPANE
  specific = 4
FEATURE [App::DocumentObjectGroupPython] Ti_element003  label="Ti_element : 1"  # scripted group (container) (typed FeaturePython)
  n = 1
  ref = Ti_element
FEATURE [App::DocumentObjectGroupPython] O_element098  label="O_element : 052"  # scripted group (container) (typed FeaturePython)
  n = 2
  ref = O_element
FEATURE [App::DocumentObjectGroupPython] G4_TITANIUM_DIOXIDE  # scripted group (container) (typed FeaturePython)
  Dunit = g/cm3
  Dvalue = 4.26
  Group = -> [Ti_element003,O_element098]
  conduct = 2
  density = 1
  expand = 3
  formula = G4_TITANIUM_DIOXIDE
  name = G4_TITANIUM_DIOXIDE
  specific = 4
FEATURE [App::DocumentObjectGroupPython] C_element114  label="C_element : 061"  # scripted group (container) (typed FeaturePython)
  n = 7
  ref = C_element
FEATURE [App::DocumentObjectGroupPython] H_element104  label="H_element : 055"  # scripted group (container) (typed FeaturePython)
  n = 8
  ref = H_element
FEATURE [App::DocumentObjectGroupPython] G4_TOLUENE  # scripted group (container) (typed FeaturePython)
  Dunit = g/cm3
  Dvalue = 0.8669
  Group = -> [C_element114,H_element104]
  conduct = 2
  density = 1
  expand = 3
  formula = G4_TOLUENE
  name = G4_TOLUENE
  specific = 4
FEATURE [App::DocumentObjectGroupPython] C_element115  label="C_element : 062"  # scripted group (container) (typed FeaturePython)
  n = 2
  ref = C_element
FEATURE [App::DocumentObjectGroupPython] H_element105  label="H_element : 056"  # scripted group (container) (typed FeaturePython)
  n = 1
  ref = H_element
FEATURE [App::DocumentObjectGroupPython] Cl_element028  label="Cl_element : 014"  # scripted group (container) (typed FeaturePython)
  n = 3
  ref = Cl_element
FEATURE [App::DocumentObjectGroupPython] G4_TRICHLOROETHYLENE  # scripted group (container) (typed FeaturePython)
  Dunit = g/cm3
  Dvalue = 1.46
  Group = -> [C_element115,H_element105,Cl_element028]
  conduct = 2
  density = 1
  expand = 3
  formula = G4_TRICHLOROETHYLENE
  name = G4_TRICHLOROETHYLENE
  specific = 4
FEATURE [App::DocumentObjectGroupPython] C_element116  label="C_element : 063"  # scripted group (container) (typed FeaturePython)
  n = 6
  ref = C_element
FEATURE [App::DocumentObjectGroupPython] H_element106  label="H_element : 15"  # scripted group (container) (typed FeaturePython)
  n = 15
  ref = H_element
FEATURE [App::DocumentObjectGroupPython] O_element099  label="O_element : 053"  # scripted group (container) (typed FeaturePython)
  n = 4
  ref = O_element
FEATURE [App::DocumentObjectGroupPython] P_element012  label="P_element : 1"  # scripted group (container) (typed FeaturePython)
  n = 1
  ref = P_element
FEATURE [App::DocumentObjectGroupPython] G4_TRIETHYL_PHOSPHATE  # scripted group (container) (typed FeaturePython)
  Dunit = g/cm3
  Dvalue = 1.07
  Group = -> [C_element116,H_element106,O_element099,P_element012]
  conduct = 2
  density = 1
  expand = 3
  formula = G4_TRIETHYL_PHOSPHATE
  name = G4_TRIETHYL_PHOSPHATE
  specific = 4
FEATURE [App::DocumentObjectGroupPython] W_element003  label="W_element : 003"  # scripted group (container) (typed FeaturePython)
  n = 1
  ref = W_element
FEATURE [App::DocumentObjectGroupPython] F_element017  label="F_element : 6"  # scripted group (container) (typed FeaturePython)
  n = 6
  ref = F_element
FEATURE [App::DocumentObjectGroupPython] G4_TUNGSTEN_HEXAFLUORIDE  # scripted group (container) (typed FeaturePython)
  Dunit = g/cm3
  Dvalue = 2.4
  Group = -> [W_element003,F_element017]
  conduct = 2
  density = 1
  expand = 3
  formula = G4_TUNGSTEN_HEXAFLUORIDE
  name = G4_TUNGSTEN_HEXAFLUORIDE
  specific = 4
FEATURE [App::DocumentObjectGroupPython] U_element001  label="U_element : 1"  # scripted group (container) (typed FeaturePython)
  n = 1
  ref = U_element
FEATURE [App::DocumentObjectGroupPython] C_element117  label="C_element : 064"  # scripted group (container) (typed FeaturePython)
  n = 2
  ref = C_element
FEATURE [App::DocumentObjectGroupPython] G4_URANIUM_DICARBIDE  # scripted group (container) (typed FeaturePython)
  Dunit = g/cm3
  Dvalue = 11.28
  Group = -> [U_element001,C_element117]
  conduct = 2
  density = 1
  expand = 3
  formula = G4_URANIUM_DICARBIDE
  name = G4_URANIUM_DICARBIDE
  specific = 4
FEATURE [App::DocumentObjectGroupPython] U_element002  label="U_element : 002"  # scripted group (container) (typed FeaturePython)
  n = 1
  ref = U_element
FEATURE [App::DocumentObjectGroupPython] C_element118  label="C_element : 065"  # scripted group (container) (typed FeaturePython)
  n = 1
  ref = C_element
FEATURE [App::DocumentObjectGroupPython] G4_URANIUM_MONOCARBIDE  # scripted group (container) (typed FeaturePython)
  Dunit = g/cm3
  Dvalue = 13.63
  Group = -> [U_element002,C_element118]
  conduct = 2
  density = 1
  expand = 3
  formula = G4_URANIUM_MONOCARBIDE
  name = G4_URANIUM_MONOCARBIDE
  specific = 4
FEATURE [App::DocumentObjectGroupPython] U_element003  label="U_element : 003"  # scripted group (container) (typed FeaturePython)
  n = 1
  ref = U_element
FEATURE [App::DocumentObjectGroupPython] O_element100  label="O_element : 054"  # scripted group (container) (typed FeaturePython)
  n = 2
  ref = O_element
FEATURE [App::DocumentObjectGroupPython] G4_URANIUM_OXIDE  # scripted group (container) (typed FeaturePython)
  Dunit = g/cm3
  Dvalue = 10.96
  Group = -> [U_element003,O_element100]
  conduct = 2
  density = 1
  expand = 3
  formula = G4_URANIUM_OXIDE
  name = G4_URANIUM_OXIDE
  specific = 4
FEATURE [App::DocumentObjectGroupPython] C_element119  label="C_element : 066"  # scripted group (container) (typed FeaturePython)
  n = 1
  ref = C_element
FEATURE [App::DocumentObjectGroupPython] H_element107  label="H_element : 057"  # scripted group (container) (typed FeaturePython)
  n = 4
  ref = H_element
FEATURE [App::DocumentObjectGroupPython] N_element046  label="N_element : 019"  # scripted group (container) (typed FeaturePython)
  n = 2
  ref = N_element
FEATURE [App::DocumentObjectGroupPython] O_element101  label="O_element : 055"  # scripted group (container) (typed FeaturePython)
  n = 1
  ref = O_element
FEATURE [App::DocumentObjectGroupPython] G4_UREA  # scripted group (container) (typed FeaturePython)
  Dunit = g/cm3
  Dvalue = 1.323
  Group = -> [C_element119,H_element107,N_element046,O_element101]
  conduct = 2
  density = 1
  expand = 3
  formula = G4_UREA
  name = G4_UREA
  specific = 4
FEATURE [App::DocumentObjectGroupPython] C_element120  label="C_element : 067"  # scripted group (container) (typed FeaturePython)
  n = 5
  ref = C_element
FEATURE [App::DocumentObjectGroupPython] H_element108  label="H_element : 058"  # scripted group (container) (typed FeaturePython)
  n = 11
  ref = H_element
FEATURE [App::DocumentObjectGroupPython] N_element047  label="N_element : 020"  # scripted group (container) (typed FeaturePython)
  n = 1
  ref = N_element
FEATURE [App::DocumentObjectGroupPython] O_element102  label="O_element : 056"  # scripted group (container) (typed FeaturePython)
  n = 2
  ref = O_element
FEATURE [App::DocumentObjectGroupPython] G4_VALINE  # scripted group (container) (typed FeaturePython)
  Dunit = g/cm3
  Dvalue = 1.23
  Group = -> [C_element120,H_element108,N_element047,O_element102]
  conduct = 2
  density = 1
  expand = 3
  formula = G4_VALINE
  name = G4_VALINE
  specific = 4
FEATURE [App::DocumentObjectGroupPython] H_element109  label="H_element : 0.009"  # scripted group (container) (typed FeaturePython)
  n = 0.009417
FEATURE [App::DocumentObjectGroupPython] C_element121  label="C_element : 0.281"  # scripted group (container) (typed FeaturePython)
  n = 0.280555
FEATURE [App::DocumentObjectGroupPython] F_element018  label="F_element : 0.710"  # scripted group (container) (typed FeaturePython)
  n = 0.710028
FEATURE [App::DocumentObjectGroupPython] G4_VITON  # scripted group (container) (typed FeaturePython)
  Dunit = g/cm3
  Dvalue = 1.8
  Group = -> [H_element109,C_element121,F_element018]
  conduct = 2
  density = 1
  expand = 3
  formula = G4_VITON
  name = G4_VITON
  specific = 4
FEATURE [App::DocumentObjectGroupPython] H_element110  label="H_element : 059"  # scripted group (container) (typed FeaturePython)
  n = 2
  ref = H_element
FEATURE [App::DocumentObjectGroupPython] O_element103  label="O_element : 057"  # scripted group (container) (typed FeaturePython)
  n = 1
  ref = O_element
FEATURE [App::DocumentObjectGroupPython] G4_WATER  # scripted group (container) (typed FeaturePython)
  Dunit = g/cm3
  Dvalue = 1
  Group = -> [H_element110,O_element103]
  conduct = 2
  density = 1
  expand = 3
  formula = G4_WATER
  name = G4_WATER
  specific = 4
FEATURE [App::DocumentObjectGroupPython] H_element111  label="H_element : 060"  # scripted group (container) (typed FeaturePython)
  n = 2
  ref = H_element
FEATURE [App::DocumentObjectGroupPython] O_element104  label="O_element : 058"  # scripted group (container) (typed FeaturePython)
  n = 1
  ref = O_element
FEATURE [App::DocumentObjectGroupPython] G4_WATER_VAPOR  # scripted group (container) (typed FeaturePython)
  Dunit = g/cm3
  Dvalue = 0.000756182
  Group = -> [H_element111,O_element104]
  conduct = 2
  density = 1
  expand = 3
  formula = G4_WATER_VAPOR
  name = G4_WATER_VAPOR
  specific = 4
FEATURE [App::DocumentObjectGroupPython] C_element122  label="C_element : 068"  # scripted group (container) (typed FeaturePython)
  n = 8
  ref = C_element
FEATURE [App::DocumentObjectGroupPython] H_element112  label="H_element : 061"  # scripted group (container) (typed FeaturePython)
  n = 10
  ref = H_element
FEATURE [App::DocumentObjectGroupPython] G4_XYLENE  # scripted group (container) (typed FeaturePython)
  Dunit = g/cm3
  Dvalue = 0.87
  Group = -> [C_element122,H_element112]
  conduct = 2
  density = 1
  expand = 3
  formula = G4_XYLENE
  name = G4_XYLENE
  specific = 4
FEATURE [App::DocumentObjectGroupPython] C_element123  label="C_element : 069"  # scripted group (container) (typed FeaturePython)
  n = 1
  ref = C_element
FEATURE [App::DocumentObjectGroupPython] G4_GRAPHITE  # scripted group (container) (typed FeaturePython)
  Dunit = g/cm3
  Dvalue = 2.21
  Group = -> [C_element123]
  conduct = 2
  density = 1
  expand = 3
  formula = G4_GRAPHITE
  name = G4_GRAPHITE
  specific = 4
FEATURE [App::DocumentObjectGroupPython] NIST  # scripted group (container) (typed FeaturePython)
  Group = -> [G4_A_150_TISSUE,G4_ACETONE,G4_ACETYLENE,G4_ADENINE,G4_ADIPOSE_TISSUE_ICRP,G4_AIR,G4_ALANINE,G4_ALUMINUM_OXIDE,G4_AMBER,G4_AMMONIA,G4_ANILINE,G4_ANTHRACENE,G4_B_100_BONE,G4_BAKELITE,G4_BARIUM_FLUORIDE,G4_BARIUM_SULFATE,G4_BENZENE,G4_BERYLLIUM_OXIDE,G4_BGO,G4_BLOOD_ICRP,G4_BONE_COMPACT_ICRU,G4_BONE_CORTICAL_ICRP,G4_BORON_CARBIDE,G4_BORON_OXIDE,G4_BRAIN_ICRP,G4_BUTANE,G4_N_BUTYL_ALCOHOL,G4_C_552,+152 more]
FEATURE [App::DocumentObjectGroupPython] H_element113  label="H_element : 062"  # scripted group (container) (typed FeaturePython)
  n = 1
  ref = H_element
FEATURE [App::DocumentObjectGroupPython] G4_H  # scripted group (container) (typed FeaturePython)
  Dunit = g/cm3
  Dvalue = 8.3748e-05
  Group = -> [H_element113]
  conduct = 2
  density = 1
  expand = 3
  formula = H
  name = G4_H
  specific = 4
FEATURE [App::DocumentObjectGroupPython] He_element001  label="He_element : 1"  # scripted group (container) (typed FeaturePython)
  n = 1
  ref = He_element
FEATURE [App::DocumentObjectGroupPython] G4_He  # scripted group (container) (typed FeaturePython)
  Dunit = g/cm3
  Dvalue = 0.000166322
  Group = -> [He_element001]
  conduct = 2
  density = 1
  expand = 3
  formula = He
  name = G4_He
  specific = 4
FEATURE [App::DocumentObjectGroupPython] Li_element008  label="Li_element : 008"  # scripted group (container) (typed FeaturePython)
  n = 1
  ref = Li_element
FEATURE [App::DocumentObjectGroupPython] G4_Li  # scripted group (container) (typed FeaturePython)
  Dunit = g/cm3
  Dvalue = 0.534
  Group = -> [Li_element008]
  conduct = 2
  density = 1
  expand = 3
  formula = Li
  name = G4_Li
  specific = 4
FEATURE [App::DocumentObjectGroupPython] Be_element002  label="Be_element : 002"  # scripted group (container) (typed FeaturePython)
  n = 1
  ref = Be_element
FEATURE [App::DocumentObjectGroupPython] G4_Be  # scripted group (container) (typed FeaturePython)
  Dunit = g/cm3
  Dvalue = 1.848
  Group = -> [Be_element002]
  conduct = 2
  density = 1
  expand = 3
  formula = Be
  name = G4_Be
  specific = 4
FEATURE [App::DocumentObjectGroupPython] B_element007  label="B_element : 007"  # scripted group (container) (typed FeaturePython)
  n = 1
  ref = B_element
FEATURE [App::DocumentObjectGroupPython] G4_B  # scripted group (container) (typed FeaturePython)
  Dunit = g/cm3
  Dvalue = 2.37
  Group = -> [B_element007]
  conduct = 2
  density = 1
  expand = 3
  formula = B
  name = G4_B
  specific = 4
FEATURE [App::DocumentObjectGroupPython] C_element124  label="C_element : 070"  # scripted group (container) (typed FeaturePython)
  n = 1
  ref = C_element
FEATURE [App::DocumentObjectGroupPython] G4_C  # scripted group (container) (typed FeaturePython)
  Dunit = g/cm3
  Dvalue = 2
  Group = -> [C_element124]
  conduct = 2
  density = 1
  expand = 3
  formula = C
  name = G4_C
  specific = 4
FEATURE [App::DocumentObjectGroupPython] N_element048  label="N_element : 021"  # scripted group (container) (typed FeaturePython)
  n = 1
  ref = N_element
FEATURE [App::DocumentObjectGroupPython] G4_N  # scripted group (container) (typed FeaturePython)
  Dunit = g/cm3
  Dvalue = 0.0011652
  Group = -> [N_element048]
  conduct = 2
  density = 1
  expand = 3
  formula = N
  name = G4_N
  specific = 4
FEATURE [App::DocumentObjectGroupPython] O_element105  label="O_element : 059"  # scripted group (container) (typed FeaturePython)
  n = 1
  ref = O_element
FEATURE [App::DocumentObjectGroupPython] G4_O  # scripted group (container) (typed FeaturePython)
  Dunit = g/cm3
  Dvalue = 0.00133151
  Group = -> [O_element105]
  conduct = 2
  density = 1
  expand = 3
  formula = O
  name = G4_O
  specific = 4
FEATURE [App::DocumentObjectGroupPython] F_element019  label="F_element : 008"  # scripted group (container) (typed FeaturePython)
  n = 1
  ref = F_element
FEATURE [App::DocumentObjectGroupPython] G4_F  # scripted group (container) (typed FeaturePython)
  Dunit = g/cm3
  Dvalue = 0.00158029
  Group = -> [F_element019]
  conduct = 2
  density = 1
  expand = 3
  formula = F
  name = G4_F
  specific = 4
FEATURE [App::DocumentObjectGroupPython] Ne_element001  label="Ne_element : 1"  # scripted group (container) (typed FeaturePython)
  n = 1
  ref = Ne_element
FEATURE [App::DocumentObjectGroupPython] G4_Ne  # scripted group (container) (typed FeaturePython)
  Dunit = g/cm3
  Dvalue = 0.000838505
  Group = -> [Ne_element001]
  conduct = 2
  density = 1
  expand = 3
  formula = Ne
  name = G4_Ne
  specific = 4
FEATURE [App::DocumentObjectGroupPython] Na_element020  label="Na_element : 005"  # scripted group (container) (typed FeaturePython)
  n = 1
  ref = Na_element
FEATURE [App::DocumentObjectGroupPython] G4_Na  # scripted group (container) (typed FeaturePython)
  Dunit = g/cm3
  Dvalue = 0.971
  Group = -> [Na_element020]
  conduct = 2
  density = 1
  expand = 3
  formula = Na
  name = G4_Na
  specific = 4
FEATURE [App::DocumentObjectGroupPython] Mg_element011  label="Mg_element : 005"  # scripted group (container) (typed FeaturePython)
  n = 1
  ref = Mg_element
FEATURE [App::DocumentObjectGroupPython] G4_Mg  # scripted group (container) (typed FeaturePython)
  Dunit = g/cm3
  Dvalue = 1.74
  Group = -> [Mg_element011]
  conduct = 2
  density = 1
  expand = 3
  formula = Mg
  name = G4_Mg
  specific = 4
FEATURE [App::DocumentObjectGroupPython] Al_element004  label="Al_element : 1"  # scripted group (container) (typed FeaturePython)
  n = 1
  ref = Al_element
FEATURE [App::DocumentObjectGroupPython] G4_Al  # scripted group (container) (typed FeaturePython)
  Dunit = g/cm3
  Dvalue = 2.699
  Group = -> [Al_element004]
  conduct = 2
  density = 1
  expand = 3
  formula = Al
  name = G4_Al
  specific = 4
FEATURE [App::DocumentObjectGroupPython] Si_element007  label="Si_element : 002"  # scripted group (container) (typed FeaturePython)
  n = 1
  ref = Si_element
FEATURE [App::DocumentObjectGroupPython] G4_Si  # scripted group (container) (typed FeaturePython)
  Dunit = g/cm3
  Dvalue = 2.33
  Group = -> [Si_element007]
  conduct = 2
  density = 1
  expand = 3
  formula = Si
  name = G4_Si
  specific = 4
FEATURE [App::DocumentObjectGroupPython] P_element013  label="P_element : 002"  # scripted group (container) (typed FeaturePython)
  n = 1
  ref = P_element
FEATURE [App::DocumentObjectGroupPython] G4_P  # scripted group (container) (typed FeaturePython)
  Dunit = g/cm3
  Dvalue = 2.2
  Group = -> [P_element013]
  conduct = 2
  density = 1
  expand = 3
  formula = P
  name = G4_P
  specific = 4
FEATURE [App::DocumentObjectGroupPython] S_element023  label="S_element : 007"  # scripted group (container) (typed FeaturePython)
  n = 1
  ref = S_element
FEATURE [App::DocumentObjectGroupPython] G4_S  # scripted group (container) (typed FeaturePython)
  Dunit = g/cm3
  Dvalue = 2
  Group = -> [S_element023]
  conduct = 2
  density = 1
  expand = 3
  formula = S
  name = G4_S
  specific = 4
FEATURE [App::DocumentObjectGroupPython] Cl_element029  label="Cl_element : 015"  # scripted group (container) (typed FeaturePython)
  n = 1
  ref = Cl_element
FEATURE [App::DocumentObjectGroupPython] G4_Cl  # scripted group (container) (typed FeaturePython)
  Dunit = g/cm3
  Dvalue = 0.00299473
  Group = -> [Cl_element029]
  conduct = 2
  density = 1
  expand = 3
  formula = Cl
  name = G4_Cl
  specific = 4
FEATURE [App::DocumentObjectGroupPython] Ar_element002  label="Ar_element : 1"  # scripted group (container) (typed FeaturePython)
  n = 1
  ref = Ar_element
FEATURE [App::DocumentObjectGroupPython] G4_Ar  # scripted group (container) (typed FeaturePython)
  Dunit = g/cm3
  Dvalue = 0.00166201
  Group = -> [Ar_element002]
  conduct = 2
  density = 1
  expand = 3
  formula = Ar
  name = G4_Ar
  specific = 4
FEATURE [App::DocumentObjectGroupPython] K_element013  label="K_element : 003"  # scripted group (container) (typed FeaturePython)
  n = 1
  ref = K_element
FEATURE [App::DocumentObjectGroupPython] G4_K  # scripted group (container) (typed FeaturePython)
  Dunit = g/cm3
  Dvalue = 0.862
  Group = -> [K_element013]
  conduct = 2
  density = 1
  expand = 3
  formula = K
  name = G4_K
  specific = 4
FEATURE [App::DocumentObjectGroupPython] Ca_element014  label="Ca_element : 007"  # scripted group (container) (typed FeaturePython)
  n = 1
  ref = Ca_element
FEATURE [App::DocumentObjectGroupPython] G4_Ca  # scripted group (container) (typed FeaturePython)
  Dunit = g/cm3
  Dvalue = 1.55
  Group = -> [Ca_element014]
  conduct = 2
  density = 1
  expand = 3
  formula = Ca
  name = G4_Ca
  specific = 4
FEATURE [App::DocumentObjectGroupPython] Sc_element001  label="Sc_element : 1"  # scripted group (container) (typed FeaturePython)
  n = 1
  ref = Sc_element
FEATURE [App::DocumentObjectGroupPython] G4_Sc  # scripted group (container) (typed FeaturePython)
  Dunit = g/cm3
  Dvalue = 2.989
  Group = -> [Sc_element001]
  conduct = 2
  density = 1
  expand = 3
  formula = Sc
  name = G4_Sc
  specific = 4
FEATURE [App::DocumentObjectGroupPython] Ti_element004  label="Ti_element : 002"  # scripted group (container) (typed FeaturePython)
  n = 1
  ref = Ti_element
FEATURE [App::DocumentObjectGroupPython] G4_Ti  # scripted group (container) (typed FeaturePython)
  Dunit = g/cm3
  Dvalue = 4.54
  Group = -> [Ti_element004]
  conduct = 2
  density = 1
  expand = 3
  formula = Ti
  name = G4_Ti
  specific = 4
FEATURE [App::DocumentObjectGroupPython] V_element001  label="V_element : 1"  # scripted group (container) (typed FeaturePython)
  n = 1
  ref = V_element
FEATURE [App::DocumentObjectGroupPython] G4_V  # scripted group (container) (typed FeaturePython)
  Dunit = g/cm3
  Dvalue = 6.11
  Group = -> [V_element001]
  conduct = 2
  density = 1
  expand = 3
  formula = V
  name = G4_V
  specific = 4
FEATURE [App::DocumentObjectGroupPython] Cr_element001  label="Cr_element : 1"  # scripted group (container) (typed FeaturePython)
  n = 1
  ref = Cr_element
FEATURE [App::DocumentObjectGroupPython] G4_Cr  # scripted group (container) (typed FeaturePython)
  Dunit = g/cm3
  Dvalue = 7.18
  Group = -> [Cr_element001]
  conduct = 2
  density = 1
  expand = 3
  formula = Cr
  name = G4_Cr
  specific = 4
FEATURE [App::DocumentObjectGroupPython] Mn_element001  label="Mn_element : 1"  # scripted group (container) (typed FeaturePython)
  n = 1
  ref = Mn_element
FEATURE [App::DocumentObjectGroupPython] G4_Mn  # scripted group (container) (typed FeaturePython)
  Dunit = g/cm3
  Dvalue = 7.44
  Group = -> [Mn_element001]
  conduct = 2
  density = 1
  expand = 3
  formula = Mn
  name = G4_Mn
  specific = 4
FEATURE [App::DocumentObjectGroupPython] Fe_element007  label="Fe_element : 004"  # scripted group (container) (typed FeaturePython)
  n = 1
  ref = Fe_element
FEATURE [App::DocumentObjectGroupPython] G4_Fe  # scripted group (container) (typed FeaturePython)
  Dunit = g/cm3
  Dvalue = 7.874
  Group = -> [Fe_element007]
  conduct = 2
  density = 1
  expand = 3
  formula = Fe
  name = G4_Fe
  specific = 4
FEATURE [App::DocumentObjectGroupPython] Co_element001  label="Co_element : 1"  # scripted group (container) (typed FeaturePython)
  n = 1
  ref = Co_element
FEATURE [App::DocumentObjectGroupPython] G4_Co  # scripted group (container) (typed FeaturePython)
  Dunit = g/cm3
  Dvalue = 8.9
  Group = -> [Co_element001]
  conduct = 2
  density = 1
  expand = 3
  formula = Co
  name = G4_Co
  specific = 4
FEATURE [App::DocumentObjectGroupPython] Ni_element001  label="Ni_element : 1"  # scripted group (container) (typed FeaturePython)
  n = 1
  ref = Ni_element
FEATURE [App::DocumentObjectGroupPython] G4_Ni  # scripted group (container) (typed FeaturePython)
  Dunit = g/cm3
  Dvalue = 8.902
  Group = -> [Ni_element001]
  conduct = 2
  density = 1
  expand = 3
  formula = Ni
  name = G4_Ni
  specific = 4
FEATURE [App::DocumentObjectGroupPython] Cu_element001  label="Cu_element : 1"  # scripted group (container) (typed FeaturePython)
  n = 1
  ref = Cu_element
FEATURE [App::DocumentObjectGroupPython] G4_Cu  # scripted group (container) (typed FeaturePython)
  Dunit = g/cm3
  Dvalue = 8.96
  Group = -> [Cu_element001]
  conduct = 2
  density = 1
  expand = 3
  formula = Cu
  name = G4_Cu
  specific = 4
FEATURE [App::DocumentObjectGroupPython] Zn_element001  label="Zn_element : 1"  # scripted group (container) (typed FeaturePython)
  n = 1
  ref = Zn_element
FEATURE [App::DocumentObjectGroupPython] G4_Zn  # scripted group (container) (typed FeaturePython)
  Dunit = g/cm3
  Dvalue = 7.133
  Group = -> [Zn_element001]
  conduct = 2
  density = 1
  expand = 3
  formula = Zn
  name = G4_Zn
  specific = 4
FEATURE [App::DocumentObjectGroupPython] Ga_element002  label="Ga_element : 002"  # scripted group (container) (typed FeaturePython)
  n = 1
  ref = Ga_element
FEATURE [App::DocumentObjectGroupPython] G4_Ga  # scripted group (container) (typed FeaturePython)
  Dunit = g/cm3
  Dvalue = 5.904
  Group = -> [Ga_element002]
  conduct = 2
  density = 1
  expand = 3
  formula = Ga
  name = G4_Ga
  specific = 4
FEATURE [App::DocumentObjectGroupPython] Ge_element002  label="Ge_element : 1"  # scripted group (container) (typed FeaturePython)
  n = 1
  ref = Ge_element
FEATURE [App::DocumentObjectGroupPython] G4_Ge  # scripted group (container) (typed FeaturePython)
  Dunit = g/cm3
  Dvalue = 5.323
  Group = -> [Ge_element002]
  conduct = 2
  density = 1
  expand = 3
  formula = Ge
  name = G4_Ge
  specific = 4
FEATURE [App::DocumentObjectGroupPython] As_element003  label="As_element : 002"  # scripted group (container) (typed FeaturePython)
  n = 1
  ref = As_element
FEATURE [App::DocumentObjectGroupPython] G4_As  # scripted group (container) (typed FeaturePython)
  Dunit = g/cm3
  Dvalue = 5.73
  Group = -> [As_element003]
  conduct = 2
  density = 1
  expand = 3
  formula = As
  name = G4_As
  specific = 4
FEATURE [App::DocumentObjectGroupPython] Se_element001  label="Se_element : 1"  # scripted group (container) (typed FeaturePython)
  n = 1
  ref = Se_element
FEATURE [App::DocumentObjectGroupPython] G4_Se  # scripted group (container) (typed FeaturePython)
  Dunit = g/cm3
  Dvalue = 4.5
  Group = -> [Se_element001]
  conduct = 2
  density = 1
  expand = 3
  formula = Se
  name = G4_Se
  specific = 4
FEATURE [App::DocumentObjectGroupPython] Br_element007  label="Br_element : 004"  # scripted group (container) (typed FeaturePython)
  n = 1
  ref = Br_element
FEATURE [App::DocumentObjectGroupPython] G4_Br  # scripted group (container) (typed FeaturePython)
  Dunit = g/cm3
  Dvalue = 0.0070721
  Group = -> [Br_element007]
  conduct = 2
  density = 1
  expand = 3
  formula = Br
  name = G4_Br
  specific = 4
FEATURE [App::DocumentObjectGroupPython] Kr_element001  label="Kr_element : 1"  # scripted group (container) (typed FeaturePython)
  n = 1
  ref = Kr_element
FEATURE [App::DocumentObjectGroupPython] G4_Kr  # scripted group (container) (typed FeaturePython)
  Dunit = g/cm3
  Dvalue = 0.00347832
  Group = -> [Kr_element001]
  conduct = 2
  density = 1
  expand = 3
  formula = Kr
  name = G4_Kr
  specific = 4
FEATURE [App::DocumentObjectGroupPython] Rb_element001  label="Rb_element : 1"  # scripted group (container) (typed FeaturePython)
  n = 1
  ref = Rb_element
FEATURE [App::DocumentObjectGroupPython] G4_Rb  # scripted group (container) (typed FeaturePython)
  Dunit = g/cm3
  Dvalue = 1.532
  Group = -> [Rb_element001]
  conduct = 2
  density = 1
  expand = 3
  formula = Rb
  name = G4_Rb
  specific = 4
FEATURE [App::DocumentObjectGroupPython] Sr_element001  label="Sr_element : 1"  # scripted group (container) (typed FeaturePython)
  n = 1
  ref = Sr_element
FEATURE [App::DocumentObjectGroupPython] G4_Sr  # scripted group (container) (typed FeaturePython)
  Dunit = g/cm3
  Dvalue = 2.54
  Group = -> [Sr_element001]
  conduct = 2
  density = 1
  expand = 3
  formula = Sr
  name = G4_Sr
  specific = 4
FEATURE [App::DocumentObjectGroupPython] Y_element001  label="Y_element : 1"  # scripted group (container) (typed FeaturePython)
  n = 1
  ref = Y_element
FEATURE [App::DocumentObjectGroupPython] G4_Y  # scripted group (container) (typed FeaturePython)
  Dunit = g/cm3
  Dvalue = 4.469
  Group = -> [Y_element001]
  conduct = 2
  density = 1
  expand = 3
  formula = Y
  name = G4_Y
  specific = 4
FEATURE [App::DocumentObjectGroupPython] Zr_element001  label="Zr_element : 1"  # scripted group (container) (typed FeaturePython)
  n = 1
  ref = Zr_element
FEATURE [App::DocumentObjectGroupPython] G4_Zr  # scripted group (container) (typed FeaturePython)
  Dunit = g/cm3
  Dvalue = 6.506
  Group = -> [Zr_element001]
  conduct = 2
  density = 1
  expand = 3
  formula = Zr
  name = G4_Zr
  specific = 4
FEATURE [App::DocumentObjectGroupPython] Nb_element001  label="Nb_element : 1"  # scripted group (container) (typed FeaturePython)
  n = 1
  ref = Nb_element
FEATURE [App::DocumentObjectGroupPython] G4_Nb  # scripted group (container) (typed FeaturePython)
  Dunit = g/cm3
  Dvalue = 8.57
  Group = -> [Nb_element001]
  conduct = 2
  density = 1
  expand = 3
  formula = Nb
  name = G4_Nb
  specific = 4
FEATURE [App::DocumentObjectGroupPython] Mo_element001  label="Mo_element : 1"  # scripted group (container) (typed FeaturePython)
  n = 1
  ref = Mo_element
FEATURE [App::DocumentObjectGroupPython] G4_Mo  # scripted group (container) (typed FeaturePython)
  Dunit = g/cm3
  Dvalue = 10.22
  Group = -> [Mo_element001]
  conduct = 2
  density = 1
  expand = 3
  formula = Mo
  name = G4_Mo
  specific = 4
FEATURE [App::DocumentObjectGroupPython] Tc_element001  label="Tc_element : 1"  # scripted group (container) (typed FeaturePython)
  n = 1
  ref = Tc_element
FEATURE [App::DocumentObjectGroupPython] G4_Tc  # scripted group (container) (typed FeaturePython)
  Dunit = g/cm3
  Dvalue = 11.5
  Group = -> [Tc_element001]
  conduct = 2
  density = 1
  expand = 3
  formula = Tc
  name = G4_Tc
  specific = 4
FEATURE [App::DocumentObjectGroupPython] Ru_element001  label="Ru_element : 1"  # scripted group (container) (typed FeaturePython)
  n = 1
  ref = Ru_element
FEATURE [App::DocumentObjectGroupPython] G4_Ru  # scripted group (container) (typed FeaturePython)
  Dunit = g/cm3
  Dvalue = 12.41
  Group = -> [Ru_element001]
  conduct = 2
  density = 1
  expand = 3
  formula = Ru
  name = G4_Ru
  specific = 4
FEATURE [App::DocumentObjectGroupPython] Rh_element001  label="Rh_element : 1"  # scripted group (container) (typed FeaturePython)
  n = 1
  ref = Rh_element
FEATURE [App::DocumentObjectGroupPython] G4_Rh  # scripted group (container) (typed FeaturePython)
  Dunit = g/cm3
  Dvalue = 12.41
  Group = -> [Rh_element001]
  conduct = 2
  density = 1
  expand = 3
  formula = Rh
  name = G4_Rh
  specific = 4
FEATURE [App::DocumentObjectGroupPython] Pd_element001  label="Pd_element : 1"  # scripted group (container) (typed FeaturePython)
  n = 1
  ref = Pd_element
FEATURE [App::DocumentObjectGroupPython] G4_Pd  # scripted group (container) (typed FeaturePython)
  Dunit = g/cm3
  Dvalue = 12.02
  Group = -> [Pd_element001]
  conduct = 2
  density = 1
  expand = 3
  formula = Pd
  name = G4_Pd
  specific = 4
FEATURE [App::DocumentObjectGroupPython] Ag_element006  label="Ag_element : 004"  # scripted group (container) (typed FeaturePython)
  n = 1
  ref = Ag_element
FEATURE [App::DocumentObjectGroupPython] G4_Ag  # scripted group (container) (typed FeaturePython)
  Dunit = g/cm3
  Dvalue = 10.5
  Group = -> [Ag_element006]
  conduct = 2
  density = 1
  expand = 3
  formula = Ag
  name = G4_Ag
  specific = 4
FEATURE [App::DocumentObjectGroupPython] Cd_element003  label="Cd_element : 003"  # scripted group (container) (typed FeaturePython)
  n = 1
  ref = Cd_element
FEATURE [App::DocumentObjectGroupPython] G4_Cd  # scripted group (container) (typed FeaturePython)
  Dunit = g/cm3
  Dvalue = 8.65
  Group = -> [Cd_element003]
  conduct = 2
  density = 1
  expand = 3
  formula = Cd
  name = G4_Cd
  specific = 4
FEATURE [App::DocumentObjectGroupPython] In_element001  label="In_element : 1"  # scripted group (container) (typed FeaturePython)
  n = 1
  ref = In_element
FEATURE [App::DocumentObjectGroupPython] G4_In  # scripted group (container) (typed FeaturePython)
  Dunit = g/cm3
  Dvalue = 7.31
  Group = -> [In_element001]
  conduct = 2
  density = 1
  expand = 3
  formula = In
  name = G4_In
  specific = 4
FEATURE [App::DocumentObjectGroupPython] Sn_element001  label="Sn_element : 1"  # scripted group (container) (typed FeaturePython)
  n = 1
  ref = Sn_element
FEATURE [App::DocumentObjectGroupPython] G4_Sn  # scripted group (container) (typed FeaturePython)
  Dunit = g/cm3
  Dvalue = 7.31
  Group = -> [Sn_element001]
  conduct = 2
  density = 1
  expand = 3
  formula = Sn
  name = G4_Sn
  specific = 4
FEATURE [App::DocumentObjectGroupPython] Sb_element001  label="Sb_element : 1"  # scripted group (container) (typed FeaturePython)
  n = 1
  ref = Sb_element
FEATURE [App::DocumentObjectGroupPython] G4_Sb  # scripted group (container) (typed FeaturePython)
  Dunit = g/cm3
  Dvalue = 6.691
  Group = -> [Sb_element001]
  conduct = 2
  density = 1
  expand = 3
  formula = Sb
  name = G4_Sb
  specific = 4
FEATURE [App::DocumentObjectGroupPython] Te_element002  label="Te_element : 002"  # scripted group (container) (typed FeaturePython)
  n = 1
  ref = Te_element
FEATURE [App::DocumentObjectGroupPython] G4_Te  # scripted group (container) (typed FeaturePython)
  Dunit = g/cm3
  Dvalue = 6.24
  Group = -> [Te_element002]
  conduct = 2
  density = 1
  expand = 3
  formula = Te
  name = G4_Te
  specific = 4
FEATURE [App::DocumentObjectGroupPython] I_element010  label="I_element : 006"  # scripted group (container) (typed FeaturePython)
  n = 1
  ref = I_element
FEATURE [App::DocumentObjectGroupPython] G4_I  # scripted group (container) (typed FeaturePython)
  Dunit = g/cm3
  Dvalue = 4.93
  Group = -> [I_element010]
  conduct = 2
  density = 1
  expand = 3
  formula = I
  name = G4_I
  specific = 4
FEATURE [App::DocumentObjectGroupPython] Xe_element001  label="Xe_element : 1"  # scripted group (container) (typed FeaturePython)
  n = 1
  ref = Xe_element
FEATURE [App::DocumentObjectGroupPython] G4_Xe  # scripted group (container) (typed FeaturePython)
  Dunit = g/cm3
  Dvalue = 0.00548536
  Group = -> [Xe_element001]
  conduct = 2
  density = 1
  expand = 3
  formula = Xe
  name = G4_Xe
  specific = 4
FEATURE [App::DocumentObjectGroupPython] Cs_element003  label="Cs_element : 003"  # scripted group (container) (typed FeaturePython)
  n = 1
  ref = Cs_element
FEATURE [App::DocumentObjectGroupPython] G4_Cs  # scripted group (container) (typed FeaturePython)
  Dunit = g/cm3
  Dvalue = 1.873
  Group = -> [Cs_element003]
  conduct = 2
  density = 1
  expand = 3
  formula = Cs
  name = G4_Cs
  specific = 4
FEATURE [App::DocumentObjectGroupPython] Ba_element003  label="Ba_element : 003"  # scripted group (container) (typed FeaturePython)
  n = 1
  ref = Ba_element
FEATURE [App::DocumentObjectGroupPython] G4_Ba  # scripted group (container) (typed FeaturePython)
  Dunit = g/cm3
  Dvalue = 3.5
  Group = -> [Ba_element003]
  conduct = 2
  density = 1
  expand = 3
  formula = Ba
  name = G4_Ba
  specific = 4
FEATURE [App::DocumentObjectGroupPython] La_element003  label="La_element : 003"  # scripted group (container) (typed FeaturePython)
  n = 1
  ref = La_element
FEATURE [App::DocumentObjectGroupPython] G4_La  # scripted group (container) (typed FeaturePython)
  Dunit = g/cm3
  Dvalue = 6.154
  Group = -> [La_element003]
  conduct = 2
  density = 1
  expand = 3
  formula = La
  name = G4_La
  specific = 4
FEATURE [App::DocumentObjectGroupPython] Ce_element002  label="Ce_element : 1"  # scripted group (container) (typed FeaturePython)
  n = 1
  ref = Ce_element
FEATURE [App::DocumentObjectGroupPython] G4_Ce  # scripted group (container) (typed FeaturePython)
  Dunit = g/cm3
  Dvalue = 6.657
  Group = -> [Ce_element002]
  conduct = 2
  density = 1
  expand = 3
  formula = Ce
  name = G4_Ce
  specific = 4
FEATURE [App::DocumentObjectGroupPython] Pr_element001  label="Pr_element : 1"  # scripted group (container) (typed FeaturePython)
  n = 1
  ref = Pr_element
FEATURE [App::DocumentObjectGroupPython] G4_Pr  # scripted group (container) (typed FeaturePython)
  Dunit = g/cm3
  Dvalue = 6.71
  Group = -> [Pr_element001]
  conduct = 2
  density = 1
  expand = 3
  formula = Pr
  name = G4_Pr
  specific = 4
FEATURE [App::DocumentObjectGroupPython] Nd_element001  label="Nd_element : 1"  # scripted group (container) (typed FeaturePython)
  n = 1
  ref = Nd_element
FEATURE [App::DocumentObjectGroupPython] G4_Nd  # scripted group (container) (typed FeaturePython)
  Dunit = g/cm3
  Dvalue = 6.9
  Group = -> [Nd_element001]
  conduct = 2
  density = 1
  expand = 3
  formula = Nd
  name = G4_Nd
  specific = 4
FEATURE [App::DocumentObjectGroupPython] Pm_element001  label="Pm_element : 1"  # scripted group (container) (typed FeaturePython)
  n = 1
  ref = Pm_element
FEATURE [App::DocumentObjectGroupPython] G4_Pm  # scripted group (container) (typed FeaturePython)
  Dunit = g/cm3
  Dvalue = 7.22
  Group = -> [Pm_element001]
  conduct = 2
  density = 1
  expand = 3
  formula = Pm
  name = G4_Pm
  specific = 4
FEATURE [App::DocumentObjectGroupPython] Sm_element001  label="Sm_element : 1"  # scripted group (container) (typed FeaturePython)
  n = 1
  ref = Sm_element
FEATURE [App::DocumentObjectGroupPython] G4_Sm  # scripted group (container) (typed FeaturePython)
  Dunit = g/cm3
  Dvalue = 7.46
  Group = -> [Sm_element001]
  conduct = 2
  density = 1
  expand = 3
  formula = Sm
  name = G4_Sm
  specific = 4
FEATURE [App::DocumentObjectGroupPython] Eu_element001  label="Eu_element : 1"  # scripted group (container) (typed FeaturePython)
  n = 1
  ref = Eu_element
FEATURE [App::DocumentObjectGroupPython] G4_Eu  # scripted group (container) (typed FeaturePython)
  Dunit = g/cm3
  Dvalue = 5.243
  Group = -> [Eu_element001]
  conduct = 2
  density = 1
  expand = 3
  formula = Eu
  name = G4_Eu
  specific = 4
FEATURE [App::DocumentObjectGroupPython] Gd_element002  label="Gd_element : 1"  # scripted group (container) (typed FeaturePython)
  n = 1
  ref = Gd_element
FEATURE [App::DocumentObjectGroupPython] G4_Gd  # scripted group (container) (typed FeaturePython)
  Dunit = g/cm3
  Dvalue = 7.9004
  Group = -> [Gd_element002]
  conduct = 2
  density = 1
  expand = 3
  formula = Gd
  name = G4_Gd
  specific = 4
FEATURE [App::DocumentObjectGroupPython] Tb_element001  label="Tb_element : 1"  # scripted group (container) (typed FeaturePython)
  n = 1
  ref = Tb_element
FEATURE [App::DocumentObjectGroupPython] G4_Tb  # scripted group (container) (typed FeaturePython)
  Dunit = g/cm3
  Dvalue = 8.229
  Group = -> [Tb_element001]
  conduct = 2
  density = 1
  expand = 3
  formula = Tb
  name = G4_Tb
  specific = 4
FEATURE [App::DocumentObjectGroupPython] Dy_element001  label="Dy_element : 1"  # scripted group (container) (typed FeaturePython)
  n = 1
  ref = Dy_element
FEATURE [App::DocumentObjectGroupPython] G4_Dy  # scripted group (container) (typed FeaturePython)
  Dunit = g/cm3
  Dvalue = 8.55
  Group = -> [Dy_element001]
  conduct = 2
  density = 1
  expand = 3
  formula = Dy
  name = G4_Dy
  specific = 4
FEATURE [App::DocumentObjectGroupPython] Ho_element001  label="Ho_element : 1"  # scripted group (container) (typed FeaturePython)
  n = 1
  ref = Ho_element
FEATURE [App::DocumentObjectGroupPython] G4_Ho  # scripted group (container) (typed FeaturePython)
  Dunit = g/cm3
  Dvalue = 8.795
  Group = -> [Ho_element001]
  conduct = 2
  density = 1
  expand = 3
  formula = Ho
  name = G4_Ho
  specific = 4
FEATURE [App::DocumentObjectGroupPython] Er_element001  label="Er_element : 1"  # scripted group (container) (typed FeaturePython)
  n = 1
  ref = Er_element
FEATURE [App::DocumentObjectGroupPython] G4_Er  # scripted group (container) (typed FeaturePython)
  Dunit = g/cm3
  Dvalue = 9.066
  Group = -> [Er_element001]
  conduct = 2
  density = 1
  expand = 3
  formula = Er
  name = G4_Er
  specific = 4
FEATURE [App::DocumentObjectGroupPython] Tm_element001  label="Tm_element : 1"  # scripted group (container) (typed FeaturePython)
  n = 1
  ref = Tm_element
FEATURE [App::DocumentObjectGroupPython] G4_Tm  # scripted group (container) (typed FeaturePython)
  Dunit = g/cm3
  Dvalue = 9.321
  Group = -> [Tm_element001]
  conduct = 2
  density = 1
  expand = 3
  formula = Tm
  name = G4_Tm
  specific = 4
FEATURE [App::DocumentObjectGroupPython] Yb_element001  label="Yb_element : 1"  # scripted group (container) (typed FeaturePython)
  n = 1
  ref = Yb_element
FEATURE [App::DocumentObjectGroupPython] G4_Yb  # scripted group (container) (typed FeaturePython)
  Dunit = g/cm3
  Dvalue = 6.73
  Group = -> [Yb_element001]
  conduct = 2
  density = 1
  expand = 3
  formula = Yb
  name = G4_Yb
  specific = 4
FEATURE [App::DocumentObjectGroupPython] Lu_element001  label="Lu_element : 1"  # scripted group (container) (typed FeaturePython)
  n = 1
  ref = Lu_element
FEATURE [App::DocumentObjectGroupPython] G4_Lu  # scripted group (container) (typed FeaturePython)
  Dunit = g/cm3
  Dvalue = 9.84
  Group = -> [Lu_element001]
  conduct = 2
  density = 1
  expand = 3
  formula = Lu
  name = G4_Lu
  specific = 4
FEATURE [App::DocumentObjectGroupPython] Hf_element001  label="Hf_element : 1"  # scripted group (container) (typed FeaturePython)
  n = 1
  ref = Hf_element
FEATURE [App::DocumentObjectGroupPython] G4_Hf  # scripted group (container) (typed FeaturePython)
  Dunit = g/cm3
  Dvalue = 13.31
  Group = -> [Hf_element001]
  conduct = 2
  density = 1
  expand = 3
  formula = Hf
  name = G4_Hf
  specific = 4
FEATURE [App::DocumentObjectGroupPython] Ta_element001  label="Ta_element : 1"  # scripted group (container) (typed FeaturePython)
  n = 1
  ref = Ta_element
FEATURE [App::DocumentObjectGroupPython] G4_Ta  # scripted group (container) (typed FeaturePython)
  Dunit = g/cm3
  Dvalue = 16.654
  Group = -> [Ta_element001]
  conduct = 2
  density = 1
  expand = 3
  formula = Ta
  name = G4_Ta
  specific = 4
FEATURE [App::DocumentObjectGroupPython] W_element004  label="W_element : 004"  # scripted group (container) (typed FeaturePython)
  n = 1
  ref = W_element
FEATURE [App::DocumentObjectGroupPython] G4_W  # scripted group (container) (typed FeaturePython)
  Dunit = g/cm3
  Dvalue = 19.3
  Group = -> [W_element004]
  conduct = 2
  density = 1
  expand = 3
  formula = W
  name = G4_W
  specific = 4
FEATURE [App::DocumentObjectGroupPython] Re_element001  label="Re_element : 1"  # scripted group (container) (typed FeaturePython)
  n = 1
  ref = Re_element
FEATURE [App::DocumentObjectGroupPython] G4_Re  # scripted group (container) (typed FeaturePython)
  Dunit = g/cm3
  Dvalue = 21.02
  Group = -> [Re_element001]
  conduct = 2
  density = 1
  expand = 3
  formula = Re
  name = G4_Re
  specific = 4
FEATURE [App::DocumentObjectGroupPython] Os_element001  label="Os_element : 1"  # scripted group (container) (typed FeaturePython)
  n = 1
  ref = Os_element
FEATURE [App::DocumentObjectGroupPython] G4_Os  # scripted group (container) (typed FeaturePython)
  Dunit = g/cm3
  Dvalue = 22.57
  Group = -> [Os_element001]
  conduct = 2
  density = 1
  expand = 3
  formula = Os
  name = G4_Os
  specific = 4
FEATURE [App::DocumentObjectGroupPython] Ir_element001  label="Ir_element : 1"  # scripted group (container) (typed FeaturePython)
  n = 1
  ref = Ir_element
FEATURE [App::DocumentObjectGroupPython] G4_Ir  # scripted group (container) (typed FeaturePython)
  Dunit = g/cm3
  Dvalue = 22.42
  Group = -> [Ir_element001]
  conduct = 2
  density = 1
  expand = 3
  formula = Ir
  name = G4_Ir
  specific = 4
FEATURE [App::DocumentObjectGroupPython] Pt_element001  label="Pt_element : 1"  # scripted group (container) (typed FeaturePython)
  n = 1
  ref = Pt_element
FEATURE [App::DocumentObjectGroupPython] G4_Pt  # scripted group (container) (typed FeaturePython)
  Dunit = g/cm3
  Dvalue = 21.45
  Group = -> [Pt_element001]
  conduct = 2
  density = 1
  expand = 3
  formula = Pt
  name = G4_Pt
  specific = 4
FEATURE [App::DocumentObjectGroupPython] Au_element001  label="Au_element : 1"  # scripted group (container) (typed FeaturePython)
  n = 1
  ref = Au_element
FEATURE [App::DocumentObjectGroupPython] G4_Au  # scripted group (container) (typed FeaturePython)
  Dunit = g/cm3
  Dvalue = 19.32
  Group = -> [Au_element001]
  conduct = 2
  density = 1
  expand = 3
  formula = Au
  name = G4_Au
  specific = 4
FEATURE [App::DocumentObjectGroupPython] Hg_element002  label="Hg_element : 002"  # scripted group (container) (typed FeaturePython)
  n = 1
  ref = Hg_element
FEATURE [App::DocumentObjectGroupPython] G4_Hg  # scripted group (container) (typed FeaturePython)
  Dunit = g/cm3
  Dvalue = 13.546
  Group = -> [Hg_element002]
  conduct = 2
  density = 1
  expand = 3
  formula = Hg
  name = G4_Hg
  specific = 4
FEATURE [App::DocumentObjectGroupPython] Tl_element002  label="Tl_element : 002"  # scripted group (container) (typed FeaturePython)
  n = 1
  ref = Tl_element
FEATURE [App::DocumentObjectGroupPython] G4_Tl  # scripted group (container) (typed FeaturePython)
  Dunit = g/cm3
  Dvalue = 11.72
  Group = -> [Tl_element002]
  conduct = 2
  density = 1
  expand = 3
  formula = Tl
  name = G4_Tl
  specific = 4
FEATURE [App::DocumentObjectGroupPython] Pb_element003  label="Pb_element : 1"  # scripted group (container) (typed FeaturePython)
  n = 1
  ref = Pb_element
FEATURE [App::DocumentObjectGroupPython] G4_Pb  # scripted group (container) (typed FeaturePython)
  Dunit = g/cm3
  Dvalue = 11.35
  Group = -> [Pb_element003]
  conduct = 2
  density = 1
  expand = 3
  formula = Pb
  name = G4_Pb
  specific = 4
FEATURE [App::DocumentObjectGroupPython] Bi_element002  label="Bi_element : 1"  # scripted group (container) (typed FeaturePython)
  n = 1
  ref = Bi_element
FEATURE [App::DocumentObjectGroupPython] G4_Bi  # scripted group (container) (typed FeaturePython)
  Dunit = g/cm3
  Dvalue = 9.747
  Group = -> [Bi_element002]
  conduct = 2
  density = 1
  expand = 3
  formula = Bi
  name = G4_Bi
  specific = 4
FEATURE [App::DocumentObjectGroupPython] Po_element001  label="Po_element : 1"  # scripted group (container) (typed FeaturePython)
  n = 1
  ref = Po_element
FEATURE [App::DocumentObjectGroupPython] G4_Po  # scripted group (container) (typed FeaturePython)
  Dunit = g/cm3
  Dvalue = 9.32
  Group = -> [Po_element001]
  conduct = 2
  density = 1
  expand = 3
  formula = Po
  name = G4_Po
  specific = 4
FEATURE [App::DocumentObjectGroupPython] At_element001  label="At_element : 1"  # scripted group (container) (typed FeaturePython)
  n = 1
  ref = At_element
FEATURE [App::DocumentObjectGroupPython] G4_At  # scripted group (container) (typed FeaturePython)
  Dunit = g/cm3
  Dvalue = 9.32
  Group = -> [At_element001]
  conduct = 2
  density = 1
  expand = 3
  formula = At
  name = G4_At
  specific = 4
FEATURE [App::DocumentObjectGroupPython] Rn_element001  label="Rn_element : 1"  # scripted group (container) (typed FeaturePython)
  n = 1
  ref = Rn_element
FEATURE [App::DocumentObjectGroupPython] G4_Rn  # scripted group (container) (typed FeaturePython)
  Dunit = g/cm3
  Dvalue = 0.00900662
  Group = -> [Rn_element001]
  conduct = 2
  density = 1
  expand = 3
  formula = Rn
  name = G4_Rn
  specific = 4
FEATURE [App::DocumentObjectGroupPython] Fr_element001  label="Fr_element : 1"  # scripted group (container) (typed FeaturePython)
  n = 1
  ref = Fr_element
FEATURE [App::DocumentObjectGroupPython] G4_Fr  # scripted group (container) (typed FeaturePython)
  Dunit = g/cm3
  Dvalue = 1
  Group = -> [Fr_element001]
  conduct = 2
  density = 1
  expand = 3
  formula = Fr
  name = G4_Fr
  specific = 4
FEATURE [App::DocumentObjectGroupPython] Ra_element001  label="Ra_element : 1"  # scripted group (container) (typed FeaturePython)
  n = 1
  ref = Ra_element
FEATURE [App::DocumentObjectGroupPython] G4_Ra  # scripted group (container) (typed FeaturePython)
  Dunit = g/cm3
  Dvalue = 5
  Group = -> [Ra_element001]
  conduct = 2
  density = 1
  expand = 3
  formula = Ra
  name = G4_Ra
  specific = 4
FEATURE [App::DocumentObjectGroupPython] Ac_element001  label="Ac_element : 1"  # scripted group (container) (typed FeaturePython)
  n = 1
  ref = Ac_element
FEATURE [App::DocumentObjectGroupPython] G4_Ac  # scripted group (container) (typed FeaturePython)
  Dunit = g/cm3
  Dvalue = 10.07
  Group = -> [Ac_element001]
  conduct = 2
  density = 1
  expand = 3
  formula = Ac
  name = G4_Ac
  specific = 4
FEATURE [App::DocumentObjectGroupPython] Th_element001  label="Th_element : 1"  # scripted group (container) (typed FeaturePython)
  n = 1
  ref = Th_element
FEATURE [App::DocumentObjectGroupPython] G4_Th  # scripted group (container) (typed FeaturePython)
  Dunit = g/cm3
  Dvalue = 11.72
  Group = -> [Th_element001]
  conduct = 2
  density = 1
  expand = 3
  formula = Th
  name = G4_Th
  specific = 4
FEATURE [App::DocumentObjectGroupPython] Pa_element001  label="Pa_element : 1"  # scripted group (container) (typed FeaturePython)
  n = 1
  ref = Pa_element
FEATURE [App::DocumentObjectGroupPython] G4_Pa  # scripted group (container) (typed FeaturePython)
  Dunit = g/cm3
  Dvalue = 15.37
  Group = -> [Pa_element001]
  conduct = 2
  density = 1
  expand = 3
  formula = Pa
  name = G4_Pa
  specific = 4
FEATURE [App::DocumentObjectGroupPython] U_element004  label="U_element : 004"  # scripted group (container) (typed FeaturePython)
  n = 1
  ref = U_element
FEATURE [App::DocumentObjectGroupPython] G4_U  # scripted group (container) (typed FeaturePython)
  Dunit = g/cm3
  Dvalue = 18.95
  Group = -> [U_element004]
  conduct = 2
  density = 1
  expand = 3
  formula = U
  name = G4_U
  specific = 4
FEATURE [App::DocumentObjectGroupPython] Np_element001  label="Np_element : 1"  # scripted group (container) (typed FeaturePython)
  n = 1
  ref = Np_element
FEATURE [App::DocumentObjectGroupPython] G4_Np  # scripted group (container) (typed FeaturePython)
  Dunit = g/cm3
  Dvalue = 20.25
  Group = -> [Np_element001]
  conduct = 2
  density = 1
  expand = 3
  formula = Np
  name = G4_Np
  specific = 4
FEATURE [App::DocumentObjectGroupPython] Pu_element002  label="Pu_element : 002"  # scripted group (container) (typed FeaturePython)
  n = 1
  ref = Pu_element
FEATURE [App::DocumentObjectGroupPython] G4_Pu  # scripted group (container) (typed FeaturePython)
  Dunit = g/cm3
  Dvalue = 19.84
  Group = -> [Pu_element002]
  conduct = 2
  density = 1
  expand = 3
  formula = Pu
  name = G4_Pu
  specific = 4
FEATURE [App::DocumentObjectGroupPython] Am_element001  label="Am_element : 1"  # scripted group (container) (typed FeaturePython)
  n = 1
  ref = Am_element
FEATURE [App::DocumentObjectGroupPython] G4_Am  # scripted group (container) (typed FeaturePython)
  Dunit = g/cm3
  Dvalue = 13.67
  Group = -> [Am_element001]
  conduct = 2
  density = 1
  expand = 3
  formula = Am
  name = G4_Am
  specific = 4
FEATURE [App::DocumentObjectGroupPython] Cm_element001  label="Cm_element : 1"  # scripted group (container) (typed FeaturePython)
  n = 1
  ref = Cm_element
FEATURE [App::DocumentObjectGroupPython] G4_Cm  # scripted group (container) (typed FeaturePython)
  Dunit = g/cm3
  Dvalue = 13.51
  Group = -> [Cm_element001]
  conduct = 2
  density = 1
  expand = 3
  formula = Cm
  name = G4_Cm
  specific = 4
FEATURE [App::DocumentObjectGroupPython] Bk_element001  label="Bk_element : 1"  # scripted group (container) (typed FeaturePython)
  n = 1
  ref = Bk_element
FEATURE [App::DocumentObjectGroupPython] G4_Bk  # scripted group (container) (typed FeaturePython)
  Dunit = g/cm3
  Dvalue = 14
  Group = -> [Bk_element001]
  conduct = 2
  density = 1
  expand = 3
  formula = Bk
  name = G4_Bk
  specific = 4
FEATURE [App::DocumentObjectGroupPython] Cf_element001  label="Cf_element : 1"  # scripted group (container) (typed FeaturePython)
  n = 1
  ref = Cf_element
FEATURE [App::DocumentObjectGroupPython] G4_Cf  # scripted group (container) (typed FeaturePython)
  Dunit = g/cm3
  Dvalue = 10
  Group = -> [Cf_element001]
  conduct = 2
  density = 1
  expand = 3
  formula = Cf
  name = G4_Cf
  specific = 4
FEATURE [App::DocumentObjectGroupPython] Element  # scripted group (container) (typed FeaturePython)
  Group = -> [G4_H,G4_He,G4_Li,G4_Be,G4_B,G4_C,G4_N,G4_O,G4_F,G4_Ne,G4_Na,G4_Mg,G4_Al,G4_Si,G4_P,G4_S,G4_Cl,G4_Ar,G4_K,G4_Ca,G4_Sc,G4_Ti,G4_V,G4_Cr,G4_Mn,G4_Fe,G4_Co,G4_Ni,G4_Cu,G4_Zn,G4_Ga,G4_Ge,G4_As,G4_Se,G4_Br,G4_Kr,G4_Rb,G4_Sr,G4_Y,G4_Zr,G4_Nb,G4_Mo,G4_Tc,G4_Ru,G4_Rh,G4_Pd,G4_Ag,G4_Cd,G4_In,G4_Sn,G4_Sb,G4_Te,G4_I,G4_Xe,G4_Cs,G4_Ba,G4_La,G4_Ce,G4_Pr,G4_Nd,G4_Pm,G4_Sm,G4_Eu,G4_Gd,G4_Tb,G4_Dy,G4_Ho,G4_Er,+30 more]
FEATURE [App::DocumentObjectGroupPython] H_element114  label="H_element : 063"  # scripted group (container) (typed FeaturePython)
  n = 2
  ref = H_element
FEATURE [App::DocumentObjectGroupPython] G4_lH2  # scripted group (container) (typed FeaturePython)
  Dunit = g/cm3
  Dvalue = 0.0708
  Group = -> [H_element114]
  conduct = 2
  density = 1
  expand = 3
  formula = G4_lH2
  name = G4_lH2
  specific = 4
FEATURE [App::DocumentObjectGroupPython] N_element049  label="N_element : 022"  # scripted group (container) (typed FeaturePython)
  n = 2
  ref = N_element
FEATURE [App::DocumentObjectGroupPython] G4_lN2  # scripted group (container) (typed FeaturePython)
  Dunit = g/cm3
  Dvalue = 0.807
  Group = -> [N_element049]
  conduct = 2
  density = 1
  expand = 3
  formula = G4_lN2
  name = G4_lN2
  specific = 4
FEATURE [App::DocumentObjectGroupPython] O_element106  label="O_element : 060"  # scripted group (container) (typed FeaturePython)
  n = 2
  ref = O_element
FEATURE [App::DocumentObjectGroupPython] G4_lO2  # scripted group (container) (typed FeaturePython)
  Dunit = g/cm3
  Dvalue = 1.141
  Group = -> [O_element106]
  conduct = 2
  density = 1
  expand = 3
  formula = G4_lO2
  name = G4_lO2
  specific = 4
FEATURE [App::DocumentObjectGroupPython] Ar  label="Ar : 1"  # scripted group (container) (typed FeaturePython)
  n = 1
  ref = Ar
FEATURE [App::DocumentObjectGroupPython] G4_lAr  # scripted group (container) (typed FeaturePython)
  Dunit = g/cm3
  Dvalue = 1.396
  Group = -> [Ar]
  conduct = 2
  density = 1
  expand = 3
  formula = G4_lAr
  name = G4_lAr
  specific = 4
FEATURE [App::DocumentObjectGroupPython] Br  label="Br : 1"  # scripted group (container) (typed FeaturePython)
  n = 1
  ref = Br
FEATURE [App::DocumentObjectGroupPython] G4_lBr  # scripted group (container) (typed FeaturePython)
  Dunit = g/cm3
  Dvalue = 3.1028
  Group = -> [Br]
  conduct = 2
  density = 1
  expand = 3
  formula = G4_lBr
  name = G4_lBr
  specific = 4
FEATURE [App::DocumentObjectGroupPython] Kr  label="Kr : 1"  # scripted group (container) (typed FeaturePython)
  n = 1
  ref = Kr
FEATURE [App::DocumentObjectGroupPython] G4_lKr  # scripted group (container) (typed FeaturePython)
  Dunit = g/cm3
  Dvalue = 2.418
  Group = -> [Kr]
  conduct = 2
  density = 1
  expand = 3
  formula = G4_lKr
  name = G4_lKr
  specific = 4
FEATURE [App::DocumentObjectGroupPython] Xe  label="Xe : 1"  # scripted group (container) (typed FeaturePython)
  n = 1
  ref = Xe
FEATURE [App::DocumentObjectGroupPython] G4_lXe  # scripted group (container) (typed FeaturePython)
  Dunit = g/cm3
  Dvalue = 2.953
  Group = -> [Xe]
  conduct = 2
  density = 1
  expand = 3
  formula = G4_lXe
  name = G4_lXe
  specific = 4
FEATURE [App::DocumentObjectGroupPython] O_element107  label="O_element : 061"  # scripted group (container) (typed FeaturePython)
  n = 4
  ref = O_element
FEATURE [App::DocumentObjectGroupPython] Pb_element004  label="Pb_element : 002"  # scripted group (container) (typed FeaturePython)
  n = 1
  ref = Pb_element
FEATURE [App::DocumentObjectGroupPython] W_element005  label="W_element : 005"  # scripted group (container) (typed FeaturePython)
  n = 1
  ref = W_element
FEATURE [App::DocumentObjectGroupPython] G4_PbWO4  # scripted group (container) (typed FeaturePython)
  Dunit = g/cm3
  Dvalue = 8.28
  Group = -> [O_element107,Pb_element004,W_element005]
  conduct = 2
  density = 1
  expand = 3
  formula = G4_PbWO4
  name = G4_PbWO4
  specific = 4
FEATURE [App::DocumentObjectGroupPython] alactic  label="alactic : 1"  # scripted group (container) (typed FeaturePython)
  n = 1
  ref = alactic
FEATURE [App::DocumentObjectGroupPython] G4_Galactic  # scripted group (container) (typed FeaturePython)
  Dunit = g/cm3
  Dvalue = 0
  Group = -> [alactic]
  conduct = 2
  density = 1
  expand = 3
  formula = G4_Galactic
  name = G4_Galactic
  specific = 4
FEATURE [App::DocumentObjectGroupPython] RAPHITE_POROUS  label="RAPHITE_POROUS : 1"  # scripted group (container) (typed FeaturePython)
  n = 1
  ref = RAPHITE_POROUS
FEATURE [App::DocumentObjectGroupPython] G4_GRAPHITE_POROUS  # scripted group (container) (typed FeaturePython)
  Dunit = g/cm3
  Dvalue = 1.7
  Group = -> [RAPHITE_POROUS]
  conduct = 2
  density = 1
  expand = 3
  formula = G4_GRAPHITE_POROUS
  name = G4_GRAPHITE_POROUS
  specific = 4
FEATURE [App::DocumentObjectGroupPython] H_element115  label="H_element : 0.150"  # scripted group (container) (typed FeaturePython)
  n = 0.080538
FEATURE [App::DocumentObjectGroupPython] C_element125  label="C_element : 0.600"  # scripted group (container) (typed FeaturePython)
  n = 0.599848
FEATURE [App::DocumentObjectGroupPython] O_element108  label="O_element : 0.320"  # scripted group (container) (typed FeaturePython)
  n = 0.319614
FEATURE [App::DocumentObjectGroupPython] G4_LUCITE  # scripted group (container) (typed FeaturePython)
  Dunit = g/cm3
  Dvalue = 1.19
  Group = -> [H_element115,C_element125,O_element108]
  conduct = 2
  density = 1
  expand = 3
  formula = G4_LUCITE
  name = G4_LUCITE
  specific = 4
FEATURE [App::DocumentObjectGroupPython] Cu_element002  label="Cu_element : 62"  # scripted group (container) (typed FeaturePython)
  n = 62
  ref = Cu_element
FEATURE [App::DocumentObjectGroupPython] Zn_element002  label="Zn_element : 35"  # scripted group (container) (typed FeaturePython)
  n = 35
  ref = Zn_element
FEATURE [App::DocumentObjectGroupPython] Pb_element005  label="Pb_element : 3"  # scripted group (container) (typed FeaturePython)
  n = 3
  ref = Pb_element
FEATURE [App::DocumentObjectGroupPython] G4_BRASS  # scripted group (container) (typed FeaturePython)
  Dunit = g/cm3
  Dvalue = 8.52
  Group = -> [Cu_element002,Zn_element002,Pb_element005]
  conduct = 2
  density = 1
  expand = 3
  formula = G4_BRASS
  name = G4_BRASS
  specific = 4
FEATURE [App::DocumentObjectGroupPython] Cu_element003  label="Cu_element : 89"  # scripted group (container) (typed FeaturePython)
  n = 89
  ref = Cu_element
FEATURE [App::DocumentObjectGroupPython] Zn_element003  label="Zn_element : 9"  # scripted group (container) (typed FeaturePython)
  n = 9
  ref = Zn_element
FEATURE [App::DocumentObjectGroupPython] Pb_element006  label="Pb_element : 2"  # scripted group (container) (typed FeaturePython)
  n = 2
  ref = Pb_element
FEATURE [App::DocumentObjectGroupPython] G4_BRONZE  # scripted group (container) (typed FeaturePython)
  Dunit = g/cm3
  Dvalue = 8.82
  Group = -> [Cu_element003,Zn_element003,Pb_element006]
  conduct = 2
  density = 1
  expand = 3
  formula = G4_BRONZE
  name = G4_BRONZE
  specific = 4
FEATURE [App::DocumentObjectGroupPython] Fe_element008  label="Fe_element : 74"  # scripted group (container) (typed FeaturePython)
  n = 74
  ref = Fe_element
FEATURE [App::DocumentObjectGroupPython] Cr_element002  label="Cr_element : 18"  # scripted group (container) (typed FeaturePython)
  n = 18
  ref = Cr_element
FEATURE [App::DocumentObjectGroupPython] Ni_element002  label="Ni_element : 8"  # scripted group (container) (typed FeaturePython)
  n = 8
  ref = Ni_element
FEATURE [App::DocumentObjectGroupPython] G4_STAINLESS_STEEL  label="G4_STAINLESS-STEEL"  # scripted group (container) (typed FeaturePython)
  Dunit = g/cm3
  Dvalue = 8
  Group = -> [Fe_element008,Cr_element002,Ni_element002]
  conduct = 2
  density = 1
  expand = 3
  formula = G4_STAINLESS-STEEL
  name = G4_STAINLESS-STEEL
  specific = 4
FEATURE [App::DocumentObjectGroupPython] H_element116  label="H_element : 064"  # scripted group (container) (typed FeaturePython)
  n = 18
  ref = H_element
FEATURE [App::DocumentObjectGroupPython] C_element126  label="C_element : 071"  # scripted group (container) (typed FeaturePython)
  n = 12
  ref = C_element
FEATURE [App::DocumentObjectGroupPython] O_element109  label="O_element : 062"  # scripted group (container) (typed FeaturePython)
  n = 7
  ref = O_element
FEATURE [App::DocumentObjectGroupPython] G4_CR39  # scripted group (container) (typed FeaturePython)
  Dunit = g/cm3
  Dvalue = 1.32
  Group = -> [H_element116,C_element126,O_element109]
  conduct = 2
  density = 1
  expand = 3
  formula = G4_CR39
  name = G4_CR39
  specific = 4
FEATURE [App::DocumentObjectGroupPython] H_element117  label="H_element : 38"  # scripted group (container) (typed FeaturePython)
  n = 38
  ref = H_element
FEATURE [App::DocumentObjectGroupPython] C_element127  label="C_element : 072"  # scripted group (container) (typed FeaturePython)
  n = 18
  ref = C_element
FEATURE [App::DocumentObjectGroupPython] O_element110  label="O_element : 063"  # scripted group (container) (typed FeaturePython)
  n = 1
  ref = O_element
FEATURE [App::DocumentObjectGroupPython] G4_OCTADECANOL  # scripted group (container) (typed FeaturePython)
  Dunit = g/cm3
  Dvalue = 0.812
  Group = -> [H_element117,C_element127,O_element110]
  conduct = 2
  density = 1
  expand = 3
  formula = G4_OCTADECANOL
  name = G4_OCTADECANOL
  specific = 4
FEATURE [App::DocumentObjectGroupPython] HEP  # scripted group (container) (typed FeaturePython)
  Group = -> [G4_lH2,G4_lN2,G4_lO2,G4_lAr,G4_lBr,G4_lKr,G4_lXe,G4_PbWO4,G4_Galactic,G4_GRAPHITE_POROUS,G4_LUCITE,G4_BRASS,G4_BRONZE,G4_STAINLESS_STEEL,G4_CR39,G4_OCTADECANOL]
FEATURE [App::DocumentObjectGroupPython] C_element128  label="C_element : 073"  # scripted group (container) (typed FeaturePython)
  n = 14
  ref = C_element
FEATURE [App::DocumentObjectGroupPython] H_element118  label="H_element : 065"  # scripted group (container) (typed FeaturePython)
  n = 10
  ref = H_element
FEATURE [App::DocumentObjectGroupPython] O_element111  label="O_element : 064"  # scripted group (container) (typed FeaturePython)
  n = 2
  ref = O_element
FEATURE [App::DocumentObjectGroupPython] N_element050  label="N_element : 023"  # scripted group (container) (typed FeaturePython)
  n = 2
  ref = N_element
FEATURE [App::DocumentObjectGroupPython] G4_KEVLAR  # scripted group (container) (typed FeaturePython)
  Dunit = g/cm3
  Dvalue = 1.44
  Group = -> [C_element128,H_element118,O_element111,N_element050]
  conduct = 2
  density = 1
  expand = 3
  formula = G4_KEVLAR
  name = G4_KEVLAR
  specific = 4
FEATURE [App::DocumentObjectGroupPython] C_element129  label="C_element : 074"  # scripted group (container) (typed FeaturePython)
  n = 10
  ref = C_element
FEATURE [App::DocumentObjectGroupPython] H_element119  label="H_element : 066"  # scripted group (container) (typed FeaturePython)
  n = 8
  ref = H_element
FEATURE [App::DocumentObjectGroupPython] O_element112  label="O_element : 065"  # scripted group (container) (typed FeaturePython)
  n = 4
  ref = O_element
FEATURE [App::DocumentObjectGroupPython] G4_DACRON  # scripted group (container) (typed FeaturePython)
  Dunit = g/cm3
  Dvalue = 1.4
  Group = -> [C_element129,H_element119,O_element112]
  conduct = 2
  density = 1
  expand = 3
  formula = G4_DACRON
  name = G4_DACRON
  specific = 4
FEATURE [App::DocumentObjectGroupPython] C_element130  label="C_element : 075"  # scripted group (container) (typed FeaturePython)
  n = 4
  ref = C_element
FEATURE [App::DocumentObjectGroupPython] H_element120  label="H_element : 067"  # scripted group (container) (typed FeaturePython)
  n = 5
  ref = H_element
FEATURE [App::DocumentObjectGroupPython] Cl_element030  label="Cl_element : 016"  # scripted group (container) (typed FeaturePython)
  n = 1
  ref = Cl_element
FEATURE [App::DocumentObjectGroupPython] G4_NEOPRENE  # scripted group (container) (typed FeaturePython)
  Dunit = g/cm3
  Dvalue = 1.23
  Group = -> [C_element130,H_element120,Cl_element030]
  conduct = 2
  density = 1
  expand = 3
  formula = G4_NEOPRENE
  name = G4_NEOPRENE
  specific = 4
FEATURE [App::DocumentObjectGroupPython] Space  # scripted group (container) (typed FeaturePython)
  Group = -> [G4_KEVLAR,G4_DACRON,G4_NEOPRENE]
FEATURE [App::DocumentObjectGroupPython] H_element121  label="H_element : 068"  # scripted group (container) (typed FeaturePython)
  n = 5
  ref = H_element
FEATURE [App::DocumentObjectGroupPython] C_element131  label="C_element : 076"  # scripted group (container) (typed FeaturePython)
  n = 4
  ref = C_element
FEATURE [App::DocumentObjectGroupPython] N_element051  label="N_element : 3"  # scripted group (container) (typed FeaturePython)
  n = 3
  ref = N_element
FEATURE [App::DocumentObjectGroupPython] O_element113  label="O_element : 066"  # scripted group (container) (typed FeaturePython)
  n = 1
  ref = O_element
FEATURE [App::DocumentObjectGroupPython] G4_CYTOSINE  # scripted group (container) (typed FeaturePython)
  Dunit = g/cm3
  Dvalue = 1.55
  Group = -> [H_element121,C_element131,N_element051,O_element113]
  conduct = 2
  density = 1
  expand = 3
  formula = G4_CYTOSINE
  name = G4_CYTOSINE
  specific = 4
FEATURE [App::DocumentObjectGroupPython] H_element122  label="H_element : 069"  # scripted group (container) (typed FeaturePython)
  n = 6
  ref = H_element
FEATURE [App::DocumentObjectGroupPython] C_element132  label="C_element : 077"  # scripted group (container) (typed FeaturePython)
  n = 5
  ref = C_element
FEATURE [App::DocumentObjectGroupPython] N_element052  label="N_element : 024"  # scripted group (container) (typed FeaturePython)
  n = 2
  ref = N_element
FEATURE [App::DocumentObjectGroupPython] O_element114  label="O_element : 067"  # scripted group (container) (typed FeaturePython)
  n = 2
  ref = O_element
FEATURE [App::DocumentObjectGroupPython] G4_THYMINE  # scripted group (container) (typed FeaturePython)
  Dunit = g/cm3
  Dvalue = 1.23
  Group = -> [H_element122,C_element132,N_element052,O_element114]
  conduct = 2
  density = 1
  expand = 3
  formula = G4_THYMINE
  name = G4_THYMINE
  specific = 4
FEATURE [App::DocumentObjectGroupPython] H_element123  label="H_element : 070"  # scripted group (container) (typed FeaturePython)
  n = 4
  ref = H_element
FEATURE [App::DocumentObjectGroupPython] C_element133  label="C_element : 078"  # scripted group (container) (typed FeaturePython)
  n = 4
  ref = C_element
FEATURE [App::DocumentObjectGroupPython] N_element053  label="N_element : 025"  # scripted group (container) (typed FeaturePython)
  n = 2
  ref = N_element
FEATURE [App::DocumentObjectGroupPython] O_element115  label="O_element : 068"  # scripted group (container) (typed FeaturePython)
  n = 2
  ref = O_element
FEATURE [App::DocumentObjectGroupPython] G4_URACIL  # scripted group (container) (typed FeaturePython)
  Dunit = g/cm3
  Dvalue = 1.32
  Group = -> [H_element123,C_element133,N_element053,O_element115]
  conduct = 2
  density = 1
  expand = 3
  formula = G4_URACIL
  name = G4_URACIL
  specific = 4
FEATURE [App::DocumentObjectGroupPython] H_element124  label="H_element : 071"  # scripted group (container) (typed FeaturePython)
  n = 4
  ref = H_element
FEATURE [App::DocumentObjectGroupPython] C_element134  label="C_element : 079"  # scripted group (container) (typed FeaturePython)
  n = 5
  ref = C_element
FEATURE [App::DocumentObjectGroupPython] N_element054  label="N_element : 026"  # scripted group (container) (typed FeaturePython)
  n = 5
  ref = N_element
FEATURE [App::DocumentObjectGroupPython] G4_DNA_ADENINE  # scripted group (container) (typed FeaturePython)
  Dunit = g/cm3
  Dvalue = 1
  Group = -> [H_element124,C_element134,N_element054]
  conduct = 2
  density = 1
  expand = 3
  formula = G4_DNA_ADENINE
  name = G4_DNA_ADENINE
  specific = 4
FEATURE [App::DocumentObjectGroupPython] H_element125  label="H_element : 072"  # scripted group (container) (typed FeaturePython)
  n = 4
  ref = H_element
FEATURE [App::DocumentObjectGroupPython] C_element135  label="C_element : 080"  # scripted group (container) (typed FeaturePython)
  n = 5
  ref = C_element
FEATURE [App::DocumentObjectGroupPython] N_element055  label="N_element : 027"  # scripted group (container) (typed FeaturePython)
  n = 5
  ref = N_element
FEATURE [App::DocumentObjectGroupPython] O_element116  label="O_element : 069"  # scripted group (container) (typed FeaturePython)
  n = 1
  ref = O_element
FEATURE [App::DocumentObjectGroupPython] G4_DNA_GUANINE  # scripted group (container) (typed FeaturePython)
  Dunit = g/cm3
  Dvalue = 1
  Group = -> [H_element125,C_element135,N_element055,O_element116]
  conduct = 2
  density = 1
  expand = 3
  formula = G4_DNA_GUANINE
  name = G4_DNA_GUANINE
  specific = 4
FEATURE [App::DocumentObjectGroupPython] H_element126  label="H_element : 073"  # scripted group (container) (typed FeaturePython)
  n = 4
  ref = H_element
FEATURE [App::DocumentObjectGroupPython] C_element136  label="C_element : 081"  # scripted group (container) (typed FeaturePython)
  n = 4
  ref = C_element
FEATURE [App::DocumentObjectGroupPython] N_element056  label="N_element : 028"  # scripted group (container) (typed FeaturePython)
  n = 3
  ref = N_element
FEATURE [App::DocumentObjectGroupPython] O_element117  label="O_element : 070"  # scripted group (container) (typed FeaturePython)
  n = 1
  ref = O_element
FEATURE [App::DocumentObjectGroupPython] G4_DNA_CYTOSINE  # scripted group (container) (typed FeaturePython)
  Dunit = g/cm3
  Dvalue = 1
  Group = -> [H_element126,C_element136,N_element056,O_element117]
  conduct = 2
  density = 1
  expand = 3
  formula = G4_DNA_CYTOSINE
  name = G4_DNA_CYTOSINE
  specific = 4
FEATURE [App::DocumentObjectGroupPython] H_element127  label="H_element : 074"  # scripted group (container) (typed FeaturePython)
  n = 5
  ref = H_element
FEATURE [App::DocumentObjectGroupPython] C_element137  label="C_element : 082"  # scripted group (container) (typed FeaturePython)
  n = 5
  ref = C_element
FEATURE [App::DocumentObjectGroupPython] N_element057  label="N_element : 029"  # scripted group (container) (typed FeaturePython)
  n = 2
  ref = N_element
FEATURE [App::DocumentObjectGroupPython] O_element118  label="O_element : 071"  # scripted group (container) (typed FeaturePython)
  n = 2
  ref = O_element
FEATURE [App::DocumentObjectGroupPython] G4_DNA_THYMINE  # scripted group (container) (typed FeaturePython)
  Dunit = g/cm3
  Dvalue = 1
  Group = -> [H_element127,C_element137,N_element057,O_element118]
  conduct = 2
  density = 1
  expand = 3
  formula = G4_DNA_THYMINE
  name = G4_DNA_THYMINE
  specific = 4
FEATURE [App::DocumentObjectGroupPython] H_element128  label="H_element : 075"  # scripted group (container) (typed FeaturePython)
  n = 3
  ref = H_element
FEATURE [App::DocumentObjectGroupPython] C_element138  label="C_element : 083"  # scripted group (container) (typed FeaturePython)
  n = 4
  ref = C_element
FEATURE [App::DocumentObjectGroupPython] N_element058  label="N_element : 030"  # scripted group (container) (typed FeaturePython)
  n = 2
  ref = N_element
FEATURE [App::DocumentObjectGroupPython] O_element119  label="O_element : 072"  # scripted group (container) (typed FeaturePython)
  n = 2
  ref = O_element
FEATURE [App::DocumentObjectGroupPython] G4_DNA_URACIL  # scripted group (container) (typed FeaturePython)
  Dunit = g/cm3
  Dvalue = 1
  Group = -> [H_element128,C_element138,N_element058,O_element119]
  conduct = 2
  density = 1
  expand = 3
  formula = G4_DNA_URACIL
  name = G4_DNA_URACIL
  specific = 4
FEATURE [App::DocumentObjectGroupPython] H_element129  label="H_element : 076"  # scripted group (container) (typed FeaturePython)
  n = 10
  ref = H_element
FEATURE [App::DocumentObjectGroupPython] C_element139  label="C_element : 084"  # scripted group (container) (typed FeaturePython)
  n = 10
  ref = C_element
FEATURE [App::DocumentObjectGroupPython] N_element059  label="N_element : 031"  # scripted group (container) (typed FeaturePython)
  n = 5
  ref = N_element
FEATURE [App::DocumentObjectGroupPython] O_element120  label="O_element : 073"  # scripted group (container) (typed FeaturePython)
  n = 4
  ref = O_element
FEATURE [App::DocumentObjectGroupPython] G4_DNA_ADENOSINE  # scripted group (container) (typed FeaturePython)
  Dunit = g/cm3
  Dvalue = 1
  Group = -> [H_element129,C_element139,N_element059,O_element120]
  conduct = 2
  density = 1
  expand = 3
  formula = G4_DNA_ADENOSINE
  name = G4_DNA_ADENOSINE
  specific = 4
FEATURE [App::DocumentObjectGroupPython] H_element130  label="H_element : 077"  # scripted group (container) (typed FeaturePython)
  n = 10
  ref = H_element
FEATURE [App::DocumentObjectGroupPython] C_element140  label="C_element : 085"  # scripted group (container) (typed FeaturePython)
  n = 10
  ref = C_element
FEATURE [App::DocumentObjectGroupPython] N_element060  label="N_element : 032"  # scripted group (container) (typed FeaturePython)
  n = 5
  ref = N_element
FEATURE [App::DocumentObjectGroupPython] O_element121  label="O_element : 074"  # scripted group (container) (typed FeaturePython)
  n = 5
  ref = O_element
FEATURE [App::DocumentObjectGroupPython] G4_DNA_GUANOSINE  # scripted group (container) (typed FeaturePython)
  Dunit = g/cm3
  Dvalue = 1
  Group = -> [H_element130,C_element140,N_element060,O_element121]
  conduct = 2
  density = 1
  expand = 3
  formula = G4_DNA_GUANOSINE
  name = G4_DNA_GUANOSINE
  specific = 4
FEATURE [App::DocumentObjectGroupPython] H_element131  label="H_element : 078"  # scripted group (container) (typed FeaturePython)
  n = 10
  ref = H_element
FEATURE [App::DocumentObjectGroupPython] C_element141  label="C_element : 086"  # scripted group (container) (typed FeaturePython)
  n = 9
  ref = C_element
FEATURE [App::DocumentObjectGroupPython] N_element061  label="N_element : 033"  # scripted group (container) (typed FeaturePython)
  n = 3
  ref = N_element
FEATURE [App::DocumentObjectGroupPython] O_element122  label="O_element : 075"  # scripted group (container) (typed FeaturePython)
  n = 5
  ref = O_element
FEATURE [App::DocumentObjectGroupPython] G4_DNA_CYTIDINE  # scripted group (container) (typed FeaturePython)
  Dunit = g/cm3
  Dvalue = 1
  Group = -> [H_element131,C_element141,N_element061,O_element122]
  conduct = 2
  density = 1
  expand = 3
  formula = G4_DNA_CYTIDINE
  name = G4_DNA_CYTIDINE
  specific = 4
FEATURE [App::DocumentObjectGroupPython] H_element132  label="H_element : 079"  # scripted group (container) (typed FeaturePython)
  n = 9
  ref = H_element
FEATURE [App::DocumentObjectGroupPython] C_element142  label="C_element : 087"  # scripted group (container) (typed FeaturePython)
  n = 9
  ref = C_element
FEATURE [App::DocumentObjectGroupPython] N_element062  label="N_element : 034"  # scripted group (container) (typed FeaturePython)
  n = 2
  ref = N_element
FEATURE [App::DocumentObjectGroupPython] O_element123  label="O_element : 076"  # scripted group (container) (typed FeaturePython)
  n = 6
  ref = O_element
FEATURE [App::DocumentObjectGroupPython] G4_DNA_URIDINE  # scripted group (container) (typed FeaturePython)
  Dunit = g/cm3
  Dvalue = 1
  Group = -> [H_element132,C_element142,N_element062,O_element123]
  conduct = 2
  density = 1
  expand = 3
  formula = G4_DNA_URIDINE
  name = G4_DNA_URIDINE
  specific = 4
FEATURE [App::DocumentObjectGroupPython] H_element133  label="H_element : 080"  # scripted group (container) (typed FeaturePython)
  n = 11
  ref = H_element
FEATURE [App::DocumentObjectGroupPython] C_element143  label="C_element : 088"  # scripted group (container) (typed FeaturePython)
  n = 10
  ref = C_element
FEATURE [App::DocumentObjectGroupPython] N_element063  label="N_element : 035"  # scripted group (container) (typed FeaturePython)
  n = 2
  ref = N_element
FEATURE [App::DocumentObjectGroupPython] O_element124  label="O_element : 077"  # scripted group (container) (typed FeaturePython)
  n = 6
  ref = O_element
FEATURE [App::DocumentObjectGroupPython] G4_DNA_METHYLURIDINE  # scripted group (container) (typed FeaturePython)
  Dunit = g/cm3
  Dvalue = 1
  Group = -> [H_element133,C_element143,N_element063,O_element124]
  conduct = 2
  density = 1
  expand = 3
  formula = G4_DNA_METHYLURIDINE
  name = G4_DNA_METHYLURIDINE
  specific = 4
FEATURE [App::DocumentObjectGroupPython] P_element014  label="P_element : 003"  # scripted group (container) (typed FeaturePython)
  n = 1
  ref = P_element
FEATURE [App::DocumentObjectGroupPython] O_element125  label="O_element : 078"  # scripted group (container) (typed FeaturePython)
  n = 3
  ref = O_element
FEATURE [App::DocumentObjectGroupPython] G4_DNA_MONOPHOSPHATE  # scripted group (container) (typed FeaturePython)
  Dunit = g/cm3
  Dvalue = 1
  Group = -> [P_element014,O_element125]
  conduct = 2
  density = 1
  expand = 3
  formula = G4_DNA_MONOPHOSPHATE
  name = G4_DNA_MONOPHOSPHATE
  specific = 4
FEATURE [App::DocumentObjectGroupPython] H_element134  label="H_element : 081"  # scripted group (container) (typed FeaturePython)
  n = 10
  ref = H_element
FEATURE [App::DocumentObjectGroupPython] C_element144  label="C_element : 089"  # scripted group (container) (typed FeaturePython)
  n = 10
  ref = C_element
FEATURE [App::DocumentObjectGroupPython] N_element064  label="N_element : 036"  # scripted group (container) (typed FeaturePython)
  n = 5
  ref = N_element
FEATURE [App::DocumentObjectGroupPython] O_element126  label="O_element : 079"  # scripted group (container) (typed FeaturePython)
  n = 7
  ref = O_element
FEATURE [App::DocumentObjectGroupPython] P_element015  label="P_element : 004"  # scripted group (container) (typed FeaturePython)
  n = 1
  ref = P_element
FEATURE [App::DocumentObjectGroupPython] G4_DNA_A  # scripted group (container) (typed FeaturePython)
  Dunit = g/cm3
  Dvalue = 1
  Group = -> [H_element134,C_element144,N_element064,O_element126,P_element015]
  conduct = 2
  density = 1
  expand = 3
  formula = G4_DNA_A
  name = G4_DNA_A
  specific = 4
FEATURE [App::DocumentObjectGroupPython] H_element135  label="H_element : 082"  # scripted group (container) (typed FeaturePython)
  n = 10
  ref = H_element
FEATURE [App::DocumentObjectGroupPython] C_element145  label="C_element : 090"  # scripted group (container) (typed FeaturePython)
  n = 10
  ref = C_element
FEATURE [App::DocumentObjectGroupPython] N_element065  label="N_element : 037"  # scripted group (container) (typed FeaturePython)
  n = 5
  ref = N_element
FEATURE [App::DocumentObjectGroupPython] O_element127  label="O_element : 8"  # scripted group (container) (typed FeaturePython)
  n = 8
  ref = O_element
FEATURE [App::DocumentObjectGroupPython] P_element016  label="P_element : 005"  # scripted group (container) (typed FeaturePython)
  n = 1
  ref = P_element
FEATURE [App::DocumentObjectGroupPython] G4_DNA_G  # scripted group (container) (typed FeaturePython)
  Dunit = g/cm3
  Dvalue = 1
  Group = -> [H_element135,C_element145,N_element065,O_element127,P_element016]
  conduct = 2
  density = 1
  expand = 3
  formula = G4_DNA_G
  name = G4_DNA_G
  specific = 4
FEATURE [App::DocumentObjectGroupPython] H_element136  label="H_element : 083"  # scripted group (container) (typed FeaturePython)
  n = 10
  ref = H_element
FEATURE [App::DocumentObjectGroupPython] C_element146  label="C_element : 091"  # scripted group (container) (typed FeaturePython)
  n = 9
  ref = C_element
FEATURE [App::DocumentObjectGroupPython] N_element066  label="N_element : 038"  # scripted group (container) (typed FeaturePython)
  n = 3
  ref = N_element
FEATURE [App::DocumentObjectGroupPython] O_element128  label="O_element : 080"  # scripted group (container) (typed FeaturePython)
  n = 8
  ref = O_element
FEATURE [App::DocumentObjectGroupPython] P_element017  label="P_element : 006"  # scripted group (container) (typed FeaturePython)
  n = 1
  ref = P_element
FEATURE [App::DocumentObjectGroupPython] G4_DNA_C  # scripted group (container) (typed FeaturePython)
  Dunit = g/cm3
  Dvalue = 1
  Group = -> [H_element136,C_element146,N_element066,O_element128,P_element017]
  conduct = 2
  density = 1
  expand = 3
  formula = G4_DNA_C
  name = G4_DNA_C
  specific = 4
FEATURE [App::DocumentObjectGroupPython] H_element137  label="H_element : 084"  # scripted group (container) (typed FeaturePython)
  n = 9
  ref = H_element
FEATURE [App::DocumentObjectGroupPython] C_element147  label="C_element : 092"  # scripted group (container) (typed FeaturePython)
  n = 9
  ref = C_element
FEATURE [App::DocumentObjectGroupPython] N_element067  label="N_element : 039"  # scripted group (container) (typed FeaturePython)
  n = 2
  ref = N_element
FEATURE [App::DocumentObjectGroupPython] O_element129  label="O_element : 9"  # scripted group (container) (typed FeaturePython)
  n = 9
  ref = O_element
FEATURE [App::DocumentObjectGroupPython] P_element018  label="P_element : 007"  # scripted group (container) (typed FeaturePython)
  n = 1
  ref = P_element
FEATURE [App::DocumentObjectGroupPython] G4_DNA_U  # scripted group (container) (typed FeaturePython)
  Dunit = g/cm3
  Dvalue = 1
  Group = -> [H_element137,C_element147,N_element067,O_element129,P_element018]
  conduct = 2
  density = 1
  expand = 3
  formula = G4_DNA_U
  name = G4_DNA_U
  specific = 4
FEATURE [App::DocumentObjectGroupPython] H_element138  label="H_element : 085"  # scripted group (container) (typed FeaturePython)
  n = 11
  ref = H_element
FEATURE [App::DocumentObjectGroupPython] C_element148  label="C_element : 093"  # scripted group (container) (typed FeaturePython)
  n = 10
  ref = C_element
FEATURE [App::DocumentObjectGroupPython] N_element068  label="N_element : 040"  # scripted group (container) (typed FeaturePython)
  n = 2
  ref = N_element
FEATURE [App::DocumentObjectGroupPython] O_element130  label="O_element : 081"  # scripted group (container) (typed FeaturePython)
  n = 9
  ref = O_element
FEATURE [App::DocumentObjectGroupPython] P_element019  label="P_element : 008"  # scripted group (container) (typed FeaturePython)
  n = 1
  ref = P_element
FEATURE [App::DocumentObjectGroupPython] G4_DNA_MU  # scripted group (container) (typed FeaturePython)
  Dunit = g/cm3
  Dvalue = 1
  Group = -> [H_element138,C_element148,N_element068,O_element130,P_element019]
  conduct = 2
  density = 1
  expand = 3
  formula = G4_DNA_MU
  name = G4_DNA_MU
  specific = 4
FEATURE [App::DocumentObjectGroupPython] BioChemical  # scripted group (container) (typed FeaturePython)
  Group = -> [G4_CYTOSINE,G4_THYMINE,G4_URACIL,G4_DNA_ADENINE,G4_DNA_GUANINE,G4_DNA_CYTOSINE,G4_DNA_THYMINE,G4_DNA_URACIL,G4_DNA_ADENOSINE,G4_DNA_GUANOSINE,G4_DNA_CYTIDINE,G4_DNA_URIDINE,G4_DNA_METHYLURIDINE,G4_DNA_MONOPHOSPHATE,G4_DNA_A,G4_DNA_G,G4_DNA_C,G4_DNA_U,G4_DNA_MU]
FEATURE [App::DocumentObjectGroupPython] G4Materials  # scripted group (container) (typed FeaturePython)
  Group = -> [NIST,Element,HEP,Space,BioChemical]
  version = 1
FEATURE [App::DocumentObjectGroupPython] Geant4  # scripted group (container) (typed FeaturePython)
  Group = -> [G4Isotopes,G4Elements,G4Materials]
FEATURE [App::DocumentObjectGroupPython] Materials  # scripted group (container) (typed FeaturePython)
  Group = -> [Geant4]
FEATURE [Part::FeaturePython] GDMLBox_WorldBox  # WARN: FeaturePython — macro-defined, semantics opaque (R4)
  lunit = 2
  material = 5
  x = 52
  y = 52
  z = 13
FEATURE [Part::FeaturePython] GDMLBox_Box  # WARN: FeaturePython — macro-defined, semantics opaque (R4)
  lunit = 2
  material = 0
  x = 10
  y = 10
  z = 10
FEATURE [Part::FeaturePython] GDMLSphere  # WARN: FeaturePython — macro-defined, semantics opaque (R4)
  aunit = 1
  deltaphi = 360
  deltatheta = 180
  lunit = 2
  material = 285
  rmax = 3
  rmin = 0
  startphi = 0
  starttheta = 0
FEATURE [Part::FeaturePython] Array  # Draft array (typed FeaturePython)
  AlwaysSyncPlacement = false
  Angle = 360
  ArrayType = 0
  Axis = (0,0,1)
  Base = -> GDMLBox_Box
  Center = (0,0,0)
  Count = 4
  ExpandArray = false
  Fuse = false
  IntervalAxis = (0,0,0)
  IntervalX = (15,0,0)
  IntervalY = (0,15,0)
  IntervalZ = (0,0,100)
  NumberCircles = 3
  NumberPolar = 5
  NumberX = 2
  NumberY = 2
  NumberZ = 1
  PlacementList = 4 placements: [(0,0,0),(0,15,0),(15,0,0),(15,15,0)]
  RadialDistance = 50
  ScaleList = (4) [(1,1,1),(1,1,1),(1,1,1),(1,1,1)]
  Symmetry = 1
  TangentialDistance = 25
FEATURE [Part::FeaturePython] Array001  # Draft array (typed FeaturePython)
  AlwaysSyncPlacement = false
  Angle = 360
  ArrayType = 0
  Axis = (0,0,1)
  Base = -> GDMLSphere
  Center = (0,0,0)
  Count = 4
  ExpandArray = false
  Fuse = false
  IntervalAxis = (0,0,0)
  IntervalX = (15,0,0)
  IntervalY = (0,15,0)
  IntervalZ = (0,0,100)
  NumberCircles = 3
  NumberPolar = 5
  NumberX = 2
  NumberY = 2
  NumberZ = 1
  PlacementList = 4 placements: [(0,0,0),(0,15,0),(15,0,0),(15,15,0)]
  RadialDistance = 50
  ScaleList = (4) [(1,1,1),(1,1,1),(1,1,1),(1,1,1)]
  Symmetry = 1
  TangentialDistance = 25
FEATURE [App::Part] Part001
  Group = -> [GDMLSphere,Array001]
  Origin = -> Origin002
FEATURE [App::Part] Part
  Group = -> [GDMLBox_Box,Array,Part001]
  Origin = -> Origin001
FEATURE [App::Part] worldVOL
  Group = -> [GDMLBox_WorldBox,Part]
  Origin = -> Origin
